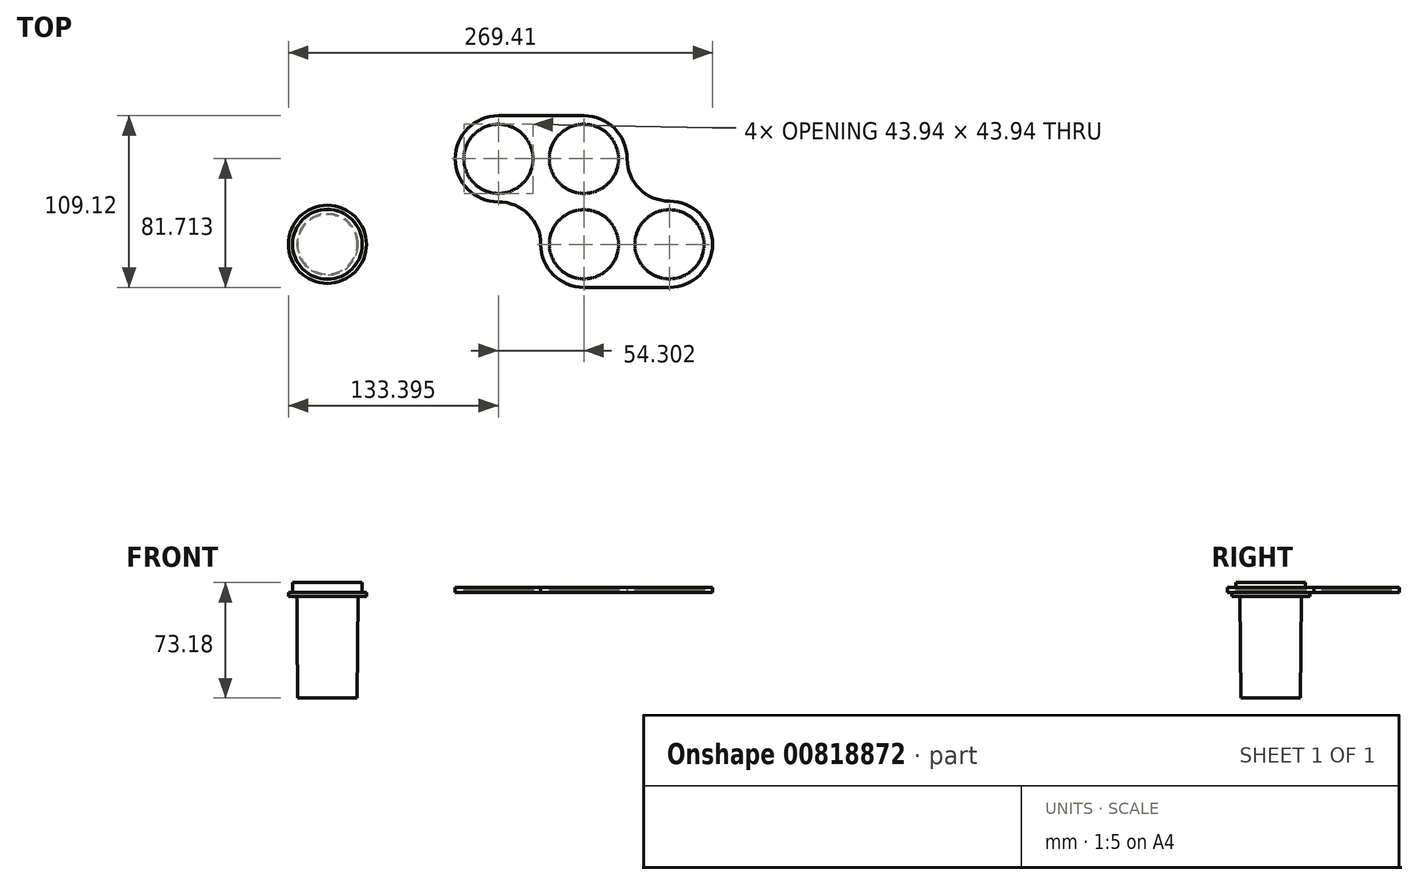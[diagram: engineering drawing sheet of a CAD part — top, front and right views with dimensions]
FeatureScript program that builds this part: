
annotation { "Feature Type Name" : "Feature", "Feature Type Description" : "" }
export const myFeature = defineFeature(function(context is Context, id is Id, definition is map)
    precondition{}
    {
        {
            assignVariable(context, id + "F0", {"name" : "hbottle", "anyValue" : 77 * mm});
        }
        {
            assignVariable(context, id + "F1", {"name" : "thick", "anyValue" : 3.17 * mm});
        }
        {
            var Q0;
            Q0=qCreatedBy(makeId("Top.planeOp"),FACE);
            var sketch = newSketch(context, id + "F2", { "sketchPlane" : qUnion([Q0])});
            skCircle(sketch, "E0", {"center": v(0, 0) * mm, "radius": 21.97 * mm, "construction": true});
            skCircle(sketch, "E1.0.1.0", {"center": v(0, 54.3) * mm, "radius": 21.97 * mm, "construction": true});
            skCircle(sketch, "E1.0.2.0", {"center": v(0, 108.6) * mm, "radius": 21.97 * mm, "construction": true});
            skCircle(sketch, "E1.0.3.0", {"center": v(0, 162.9) * mm, "radius": 21.97 * mm, "construction": true});
            skCircle(sketch, "E1.0.4.0", {"center": v(0, 217.2) * mm, "radius": 21.97 * mm, "construction": true});
            skCircle(sketch, "E1.0.5.0", {"center": v(0, 271.51) * mm, "radius": 21.97 * mm, "construction": true});
            skCircle(sketch, "E1.0.6.0", {"center": v(0, 325.81) * mm, "radius": 21.97 * mm, "construction": true});
            skCircle(sketch, "E1.0.7.0", {"center": v(0, 380.12) * mm, "radius": 21.97 * mm, "construction": true});
            skCircle(sketch, "E1.0.8.0", {"center": v(0, 434.42) * mm, "radius": 21.97 * mm, "construction": true});
            skCircle(sketch, "E1.0.9.0", {"center": v(0, 488.72) * mm, "radius": 21.97 * mm, "construction": true});
            skCircle(sketch, "E1.1.0.0", {"center": v(54.3, 0) * mm, "radius": 21.97 * mm, "construction": true});
            skCircle(sketch, "E1.1.1.0", {"center": v(54.3, 54.3) * mm, "radius": 21.97 * mm, "construction": true});
            skCircle(sketch, "E1.1.2.0", {"center": v(54.3, 108.6) * mm, "radius": 21.97 * mm, "construction": true});
            skCircle(sketch, "E1.1.3.0", {"center": v(54.3, 162.9) * mm, "radius": 21.97 * mm, "construction": true});
            skCircle(sketch, "E1.1.4.0", {"center": v(54.3, 217.2) * mm, "radius": 21.97 * mm, "construction": true});
            skCircle(sketch, "E1.1.5.0", {"center": v(54.3, 271.51) * mm, "radius": 21.97 * mm, "construction": true});
            skCircle(sketch, "E1.1.6.0", {"center": v(54.3, 325.81) * mm, "radius": 21.97 * mm, "construction": true});
            skCircle(sketch, "E1.1.7.0", {"center": v(54.3, 380.12) * mm, "radius": 21.97 * mm, "construction": true});
            skCircle(sketch, "E1.1.8.0", {"center": v(54.3, 434.42) * mm, "radius": 21.97 * mm, "construction": true});
            skCircle(sketch, "E1.1.9.0", {"center": v(54.3, 488.72) * mm, "radius": 21.97 * mm, "construction": true});
            skCircle(sketch, "E1.2.0.0", {"center": v(108.6, 0) * mm, "radius": 21.97 * mm, "construction": true});
            skCircle(sketch, "E1.2.1.0", {"center": v(108.6, 54.3) * mm, "radius": 21.97 * mm, "construction": true});
            skCircle(sketch, "E1.2.2.0", {"center": v(108.6, 108.6) * mm, "radius": 21.97 * mm, "construction": true});
            skCircle(sketch, "E1.2.3.0", {"center": v(108.6, 162.9) * mm, "radius": 21.97 * mm, "construction": true});
            skCircle(sketch, "E1.2.4.0", {"center": v(108.6, 217.2) * mm, "radius": 21.97 * mm, "construction": true});
            skCircle(sketch, "E1.2.5.0", {"center": v(108.6, 271.51) * mm, "radius": 21.97 * mm, "construction": true});
            skCircle(sketch, "E1.2.6.0", {"center": v(108.6, 325.81) * mm, "radius": 21.97 * mm, "construction": true});
            skCircle(sketch, "E1.2.7.0", {"center": v(108.6, 380.12) * mm, "radius": 21.97 * mm, "construction": true});
            skCircle(sketch, "E1.2.8.0", {"center": v(108.6, 434.42) * mm, "radius": 21.97 * mm, "construction": true});
            skCircle(sketch, "E1.2.9.0", {"center": v(108.6, 488.72) * mm, "radius": 21.97 * mm, "construction": true});
            skCircle(sketch, "E1.3.0.0", {"center": v(162.9, 0) * mm, "radius": 21.97 * mm, "construction": true});
            skCircle(sketch, "E1.3.1.0", {"center": v(162.9, 54.3) * mm, "radius": 21.97 * mm, "construction": true});
            skCircle(sketch, "E1.3.2.0", {"center": v(162.9, 108.6) * mm, "radius": 21.97 * mm, "construction": true});
            skCircle(sketch, "E1.3.3.0", {"center": v(162.9, 162.9) * mm, "radius": 21.97 * mm, "construction": true});
            skCircle(sketch, "E1.3.4.0", {"center": v(162.9, 217.2) * mm, "radius": 21.97 * mm, "construction": true});
            skCircle(sketch, "E1.3.5.0", {"center": v(162.9, 271.51) * mm, "radius": 21.97 * mm, "construction": true});
            skCircle(sketch, "E1.3.6.0", {"center": v(162.9, 325.81) * mm, "radius": 21.97 * mm, "construction": true});
            skCircle(sketch, "E1.3.7.0", {"center": v(162.9, 380.12) * mm, "radius": 21.97 * mm, "construction": true});
            skCircle(sketch, "E1.3.8.0", {"center": v(162.9, 434.42) * mm, "radius": 21.97 * mm, "construction": true});
            skCircle(sketch, "E1.3.9.0", {"center": v(162.9, 488.72) * mm, "radius": 21.97 * mm, "construction": true});
            skCircle(sketch, "E1.4.0.0", {"center": v(217.2, 0) * mm, "radius": 21.97 * mm, "construction": true});
            skCircle(sketch, "E1.4.1.0", {"center": v(217.2, 54.3) * mm, "radius": 21.97 * mm, "construction": true});
            skCircle(sketch, "E1.4.2.0", {"center": v(217.2, 108.6) * mm, "radius": 21.97 * mm, "construction": true});
            skCircle(sketch, "E1.4.3.0", {"center": v(217.2, 162.9) * mm, "radius": 21.97 * mm, "construction": true});
            skCircle(sketch, "E1.4.4.0", {"center": v(217.2, 217.2) * mm, "radius": 21.97 * mm, "construction": true});
            skCircle(sketch, "E1.4.5.0", {"center": v(217.2, 271.51) * mm, "radius": 21.97 * mm, "construction": true});
            skCircle(sketch, "E1.4.6.0", {"center": v(217.2, 325.81) * mm, "radius": 21.97 * mm, "construction": true});
            skCircle(sketch, "E1.4.7.0", {"center": v(217.2, 380.12) * mm, "radius": 21.97 * mm, "construction": true});
            skCircle(sketch, "E1.4.8.0", {"center": v(217.2, 434.42) * mm, "radius": 21.97 * mm, "construction": true});
            skCircle(sketch, "E1.4.9.0", {"center": v(217.2, 488.72) * mm, "radius": 21.97 * mm, "construction": true});
            skCircle(sketch, "E1.5.0.0", {"center": v(271.51, 0) * mm, "radius": 21.97 * mm, "construction": true});
            skCircle(sketch, "E1.5.1.0", {"center": v(271.51, 54.3) * mm, "radius": 21.97 * mm, "construction": true});
            skCircle(sketch, "E1.5.2.0", {"center": v(271.51, 108.6) * mm, "radius": 21.97 * mm, "construction": true});
            skCircle(sketch, "E1.5.3.0", {"center": v(271.51, 162.9) * mm, "radius": 21.97 * mm, "construction": true});
            skCircle(sketch, "E1.5.4.0", {"center": v(271.51, 217.2) * mm, "radius": 21.97 * mm, "construction": true});
            skCircle(sketch, "E1.5.5.0", {"center": v(271.51, 271.51) * mm, "radius": 21.97 * mm, "construction": true});
            skCircle(sketch, "E1.5.6.0", {"center": v(271.51, 325.81) * mm, "radius": 21.97 * mm, "construction": true});
            skCircle(sketch, "E1.5.7.0", {"center": v(271.51, 380.12) * mm, "radius": 21.97 * mm, "construction": true});
            skCircle(sketch, "E1.5.8.0", {"center": v(271.51, 434.42) * mm, "radius": 21.97 * mm, "construction": true});
            skCircle(sketch, "E1.5.9.0", {"center": v(271.51, 488.72) * mm, "radius": 21.97 * mm, "construction": true});
            skCircle(sketch, "E1.6.0.0", {"center": v(325.81, 0) * mm, "radius": 21.97 * mm, "construction": true});
            skCircle(sketch, "E1.6.1.0", {"center": v(325.81, 54.3) * mm, "radius": 21.97 * mm, "construction": true});
            skCircle(sketch, "E1.6.2.0", {"center": v(325.81, 108.6) * mm, "radius": 21.97 * mm, "construction": true});
            skCircle(sketch, "E1.6.3.0", {"center": v(325.81, 162.9) * mm, "radius": 21.97 * mm, "construction": true});
            skCircle(sketch, "E1.6.4.0", {"center": v(325.81, 217.2) * mm, "radius": 21.97 * mm, "construction": true});
            skCircle(sketch, "E1.6.5.0", {"center": v(325.81, 271.51) * mm, "radius": 21.97 * mm, "construction": true});
            skCircle(sketch, "E1.6.6.0", {"center": v(325.81, 325.81) * mm, "radius": 21.97 * mm, "construction": true});
            skCircle(sketch, "E1.6.7.0", {"center": v(325.81, 380.12) * mm, "radius": 21.97 * mm, "construction": true});
            skCircle(sketch, "E1.6.8.0", {"center": v(325.81, 434.42) * mm, "radius": 21.97 * mm, "construction": true});
            skCircle(sketch, "E1.6.9.0", {"center": v(325.81, 488.72) * mm, "radius": 21.97 * mm, "construction": true});
            skCircle(sketch, "E1.7.0.0", {"center": v(380.12, 0) * mm, "radius": 21.97 * mm, "construction": true});
            skCircle(sketch, "E1.7.1.0", {"center": v(380.12, 54.3) * mm, "radius": 21.97 * mm, "construction": true});
            skCircle(sketch, "E1.7.2.0", {"center": v(380.12, 108.6) * mm, "radius": 21.97 * mm, "construction": true});
            skCircle(sketch, "E1.7.3.0", {"center": v(380.12, 162.9) * mm, "radius": 21.97 * mm, "construction": true});
            skCircle(sketch, "E1.7.4.0", {"center": v(380.12, 217.2) * mm, "radius": 21.97 * mm, "construction": true});
            skCircle(sketch, "E1.7.5.0", {"center": v(380.12, 271.51) * mm, "radius": 21.97 * mm, "construction": true});
            skCircle(sketch, "E1.7.6.0", {"center": v(380.12, 325.81) * mm, "radius": 21.97 * mm, "construction": true});
            skCircle(sketch, "E1.7.7.0", {"center": v(380.12, 380.12) * mm, "radius": 21.97 * mm, "construction": true});
            skCircle(sketch, "E1.7.8.0", {"center": v(380.12, 434.42) * mm, "radius": 21.97 * mm, "construction": true});
            skCircle(sketch, "E1.7.9.0", {"center": v(380.12, 488.72) * mm, "radius": 21.97 * mm, "construction": true});
            skCircle(sketch, "E1.8.0.0", {"center": v(434.42, 0) * mm, "radius": 21.97 * mm, "construction": true});
            skCircle(sketch, "E1.8.1.0", {"center": v(434.42, 54.3) * mm, "radius": 21.97 * mm, "construction": true});
            skCircle(sketch, "E1.8.2.0", {"center": v(434.42, 108.6) * mm, "radius": 21.97 * mm, "construction": true});
            skCircle(sketch, "E1.8.3.0", {"center": v(434.42, 162.9) * mm, "radius": 21.97 * mm, "construction": true});
            skCircle(sketch, "E1.8.4.0", {"center": v(434.42, 217.2) * mm, "radius": 21.97 * mm, "construction": true});
            skCircle(sketch, "E1.8.5.0", {"center": v(434.42, 271.51) * mm, "radius": 21.97 * mm, "construction": true});
            skCircle(sketch, "E1.8.6.0", {"center": v(434.42, 325.81) * mm, "radius": 21.97 * mm, "construction": true});
            skCircle(sketch, "E1.8.7.0", {"center": v(434.42, 380.12) * mm, "radius": 21.97 * mm, "construction": true});
            skCircle(sketch, "E1.8.8.0", {"center": v(434.42, 434.42) * mm, "radius": 21.97 * mm, "construction": true});
            skCircle(sketch, "E1.8.9.0", {"center": v(434.42, 488.72) * mm, "radius": 21.97 * mm, "construction": true});
            skCircle(sketch, "E1.9.0.0", {"center": v(488.72, 0) * mm, "radius": 21.97 * mm, "construction": true});
            skCircle(sketch, "E1.9.1.0", {"center": v(488.72, 54.3) * mm, "radius": 21.97 * mm, "construction": true});
            skCircle(sketch, "E1.9.2.0", {"center": v(488.72, 108.6) * mm, "radius": 21.97 * mm, "construction": true});
            skCircle(sketch, "E1.9.3.0", {"center": v(488.72, 162.9) * mm, "radius": 21.97 * mm, "construction": true});
            skCircle(sketch, "E1.9.4.0", {"center": v(488.72, 217.2) * mm, "radius": 21.97 * mm, "construction": true});
            skCircle(sketch, "E1.9.5.0", {"center": v(488.72, 271.51) * mm, "radius": 21.97 * mm, "construction": true});
            skCircle(sketch, "E1.9.6.0", {"center": v(488.72, 325.81) * mm, "radius": 21.97 * mm, "construction": true});
            skCircle(sketch, "E1.9.7.0", {"center": v(488.72, 380.12) * mm, "radius": 21.97 * mm, "construction": true});
            skCircle(sketch, "E1.9.8.0", {"center": v(488.72, 434.42) * mm, "radius": 21.97 * mm, "construction": true});
            skCircle(sketch, "E1.9.9.0", {"center": v(488.72, 488.72) * mm, "radius": 21.97 * mm, "construction": true});
            skLineSegment(sketch, "E1.direction1", {"start": v(0, 0) * mm, "end": v(54.3, 0) * mm, "construction": true});
            skLineSegment(sketch, "E1.direction2", {"start": v(0, 0) * mm, "end": v(0, 54.3) * mm, "construction": true});
            skSolve(sketch);
        }
        {
            var Q0;
            Q0=qCreatedBy(makeId("Top.planeOp"),FACE);
            var sketch = newSketch(context, id + "F3", { "sketchPlane" : qUnion([Q0])});
            skCircle(sketch, "E2.0", {"center": v(0, 0) * mm, "radius": 21.97 * mm});
            skCircle(sketch, "E3.0", {"center": v(0, 54.3) * mm, "radius": 21.97 * mm});
            skCircle(sketch, "E4.0", {"center": v(54.3, 0) * mm, "radius": 21.97 * mm});
            skArc(sketch, "E5", {"start": v(0, -27.15) * mm, "mid": v(-19.2, -19.2) * mm, "end": v(-27.15, 0) * mm});
            skArc(sketch, "E6", {"start": v(-27.15, 54.3) * mm, "mid": v(0, 81.45) * mm, "end": v(27.15, 54.3) * mm});
            skArc(sketch, "E7", {"start": v(54.3, 27.15) * mm, "mid": v(81.45, 0) * mm, "end": v(54.3, -27.15) * mm});
            skLineSegment(sketch, "E8", {"start": v(-27.15, 0) * mm, "end": v(-27.15, 54.3) * mm});
            skLineSegment(sketch, "E9", {"start": v(0, -27.15) * mm, "end": v(54.3, -27.15) * mm});
            skArc(sketch, "E10", {"start": v(54.3, 27.15) * mm, "mid": v(35.1, 35.1) * mm, "end": v(27.15, 54.3) * mm});
            skCircle(sketch, "E11.0", {"center": v(108.6, 54.3) * mm, "radius": 21.97 * mm});
            skCircle(sketch, "E12.0", {"center": v(162.9, 0) * mm, "radius": 21.97 * mm});
            skCircle(sketch, "E13.0", {"center": v(54.3, 162.9) * mm, "radius": 21.97 * mm});
            skCircle(sketch, "E14.0", {"center": v(162.9, 54.3) * mm, "radius": 21.97 * mm});
            skCircle(sketch, "E15.0", {"center": v(217.2, 0) * mm, "radius": 21.97 * mm});
            skCircle(sketch, "E16.0", {"center": v(0, 162.9) * mm, "radius": 21.97 * mm});
            skCircle(sketch, "E17.0", {"center": v(108.6, 162.9) * mm, "radius": 21.97 * mm});
            skCircle(sketch, "E18.0", {"center": v(54.3, 217.2) * mm, "radius": 21.97 * mm});
            skCircle(sketch, "E19.0", {"center": v(217.2, 217.2) * mm, "radius": 21.97 * mm});
            skCircle(sketch, "E20.0", {"center": v(217.2, 162.9) * mm, "radius": 21.97 * mm});
            skCircle(sketch, "E21.0", {"center": v(217.2, 108.6) * mm, "radius": 21.97 * mm});
            skArc(sketch, "E22", {"start": v(0, 135.76) * mm, "mid": v(-27.15, 162.9) * mm, "end": v(0, 190.06) * mm});
            skArc(sketch, "E23", {"start": v(27.15, 217.2) * mm, "mid": v(54.3, 244.36) * mm, "end": v(81.45, 217.2) * mm});
            skArc(sketch, "E24", {"start": v(108.6, 190.06) * mm, "mid": v(135.76, 162.9) * mm, "end": v(108.6, 135.76) * mm});
            skArc(sketch, "E25", {"start": v(108.6, 27.15) * mm, "mid": v(81.45, 54.3) * mm, "end": v(108.6, 81.45) * mm});
            skArc(sketch, "E26", {"start": v(162.9, -27.15) * mm, "mid": v(143.7, -19.2) * mm, "end": v(135.76, 0) * mm});
            skArc(sketch, "E27", {"start": v(162.9, 81.45) * mm, "mid": v(182.1, 73.5) * mm, "end": v(190.06, 54.3) * mm});
            skArc(sketch, "E28", {"start": v(217.2, 27.15) * mm, "mid": v(244.36, 0) * mm, "end": v(217.2, -27.15) * mm});
            skArc(sketch, "E29", {"start": v(190.06, 108.6) * mm, "mid": v(217.2, 81.45) * mm, "end": v(244.36, 108.6) * mm});
            skArc(sketch, "E30", {"start": v(190.06, 217.2) * mm, "mid": v(217.2, 244.36) * mm, "end": v(244.36, 217.2) * mm});
            skArc(sketch, "E31", {"start": v(108.6, 190.06) * mm, "mid": v(89.4, 198.01) * mm, "end": v(81.45, 217.2) * mm});
            skArc(sketch, "E32", {"start": v(27.15, 217.2) * mm, "mid": v(19.2, 198.01) * mm, "end": v(0, 190.06) * mm});
            skArc(sketch, "E33", {"start": v(190.06, 54.3) * mm, "mid": v(198.01, 35.1) * mm, "end": v(217.2, 27.15) * mm});
            skArc(sketch, "E34", {"start": v(135.76, 0) * mm, "mid": v(127.8, 19.2) * mm, "end": v(108.6, 27.15) * mm});
            skLineSegment(sketch, "E35", {"start": v(0, 135.76) * mm, "end": v(108.6, 135.76) * mm});
            skLineSegment(sketch, "E36", {"start": v(108.6, 81.45) * mm, "end": v(162.9, 81.45) * mm});
            skLineSegment(sketch, "E37", {"start": v(162.9, -27.15) * mm, "end": v(217.2, -27.15) * mm});
            skLineSegment(sketch, "E38", {"start": v(244.36, 217.2) * mm, "end": v(244.36, 108.6) * mm});
            skLineSegment(sketch, "E39", {"start": v(190.06, 217.2) * mm, "end": v(190.06, 108.6) * mm});
            skCircle(sketch, "E40.0", {"center": v(162.9, 271.51) * mm, "radius": 21.97 * mm});
            skCircle(sketch, "E41.0", {"center": v(162.9, 325.81) * mm, "radius": 21.97 * mm});
            skCircle(sketch, "E42.0", {"center": v(108.6, 325.81) * mm, "radius": 21.97 * mm});
            skCircle(sketch, "E43.0", {"center": v(108.6, 380.12) * mm, "radius": 21.97 * mm});
            skCircle(sketch, "E44.0", {"center": v(54.3, 380.12) * mm, "radius": 21.97 * mm});
            skArc(sketch, "E45", {"start": v(54.3, 352.97) * mm, "mid": v(27.15, 380.12) * mm, "end": v(54.3, 407.27) * mm});
            skArc(sketch, "E46", {"start": v(81.45, 325.81) * mm, "mid": v(89.4, 306.62) * mm, "end": v(108.6, 298.66) * mm});
            skArc(sketch, "E47", {"start": v(108.6, 407.27) * mm, "mid": v(127.8, 399.32) * mm, "end": v(135.76, 380.12) * mm});
            skArc(sketch, "E48", {"start": v(162.9, 352.97) * mm, "mid": v(182.1, 345.01) * mm, "end": v(190.06, 325.81) * mm});
            skArc(sketch, "E49", {"start": v(135.76, 271.51) * mm, "mid": v(162.9, 244.36) * mm, "end": v(190.06, 271.51) * mm});
            skArc(sketch, "E50", {"start": v(81.45, 325.81) * mm, "mid": v(73.5, 345.01) * mm, "end": v(54.3, 352.97) * mm});
            skArc(sketch, "E51", {"start": v(135.76, 271.51) * mm, "mid": v(127.8, 290.71) * mm, "end": v(108.6, 298.66) * mm});
            skArc(sketch, "E52", {"start": v(162.9, 352.97) * mm, "mid": v(143.7, 360.92) * mm, "end": v(135.76, 380.12) * mm});
            skLineSegment(sketch, "E53", {"start": v(54.3, 407.27) * mm, "end": v(108.6, 407.27) * mm});
            skLineSegment(sketch, "E54", {"start": v(190.06, 271.51) * mm, "end": v(190.06, 325.81) * mm});
            skSolve(sketch);
        }
        {
            var Q0;
            Q0=qCreatedBy(makeId("Top.planeOp"),FACE);
            var sketch = newSketch(context, id + "F4", { "sketchPlane" : qUnion([Q0])});
            skArc(sketch, "E55.0", {"start": v(0, -27.4) * mm, "mid": v(-19.38, -19.38) * mm, "end": v(-27.4, 0) * mm});
            skArc(sketch, "E55.1", {"start": v(54.3, 27.4) * mm, "mid": v(81.7, 0) * mm, "end": v(54.3, -27.4) * mm});
            skArc(sketch, "E55.2", {"start": v(54.3, 27.4) * mm, "mid": v(35.28, 35.28) * mm, "end": v(27.4, 54.3) * mm});
            skLineSegment(sketch, "E55.3", {"start": v(0, -27.4) * mm, "end": v(54.3, -27.4) * mm});
            skArc(sketch, "E55.4", {"start": v(-27.4, 54.3) * mm, "mid": v(0, 81.7) * mm, "end": v(27.4, 54.3) * mm});
            skLineSegment(sketch, "E55.5", {"start": v(-27.4, 0) * mm, "end": v(-27.4, 54.3) * mm});
            skPoint(sketch, "E56.centerSnap0", {"position": v(81.7, 0) * mm});
            skArc(sketch, "E57.0", {"start": v(108.6, 190.31) * mm, "mid": v(136.01, 162.9) * mm, "end": v(108.6, 135.5) * mm});
            skArc(sketch, "E57.1", {"start": v(26.9, 217.2) * mm, "mid": v(54.3, 244.62) * mm, "end": v(81.7, 217.2) * mm});
            skArc(sketch, "E57.2", {"start": v(26.9, 217.2) * mm, "mid": v(19.02, 198.2) * mm, "end": v(0, 190.31) * mm});
            skArc(sketch, "E57.3", {"start": v(108.6, 190.31) * mm, "mid": v(89.59, 198.2) * mm, "end": v(81.7, 217.2) * mm});
            skArc(sketch, "E57.4", {"start": v(0, 135.5) * mm, "mid": v(-27.4, 162.9) * mm, "end": v(0, 190.31) * mm});
            skLineSegment(sketch, "E57.5", {"start": v(0, 135.5) * mm, "end": v(108.6, 135.5) * mm});
            skLineSegment(sketch, "E58.0", {"start": v(189.8, 217.2) * mm, "end": v(189.8, 108.6) * mm});
            skArc(sketch, "E58.1", {"start": v(189.8, 217.2) * mm, "mid": v(217.2, 244.62) * mm, "end": v(244.62, 217.2) * mm});
            skLineSegment(sketch, "E58.2", {"start": v(244.62, 217.2) * mm, "end": v(244.62, 108.6) * mm});
            skArc(sketch, "E58.3", {"start": v(189.8, 108.6) * mm, "mid": v(217.2, 81.2) * mm, "end": v(244.62, 108.6) * mm});
            skArc(sketch, "E59.0", {"start": v(108.6, 26.9) * mm, "mid": v(81.2, 54.3) * mm, "end": v(108.6, 81.7) * mm});
            skArc(sketch, "E59.1", {"start": v(135.5, 0) * mm, "mid": v(127.62, 19.02) * mm, "end": v(108.6, 26.9) * mm});
            skLineSegment(sketch, "E59.2", {"start": v(108.6, 81.7) * mm, "end": v(162.9, 81.7) * mm});
            skArc(sketch, "E59.3", {"start": v(162.9, -27.4) * mm, "mid": v(143.53, -19.38) * mm, "end": v(135.5, 0) * mm});
            skArc(sketch, "E59.4", {"start": v(162.9, 81.7) * mm, "mid": v(182.29, 73.68) * mm, "end": v(190.31, 54.3) * mm});
            skArc(sketch, "E59.5", {"start": v(190.31, 54.3) * mm, "mid": v(198.2, 35.28) * mm, "end": v(217.2, 27.4) * mm});
            skArc(sketch, "E59.6", {"start": v(217.2, 27.4) * mm, "mid": v(244.62, 0) * mm, "end": v(217.2, -27.4) * mm});
            skLineSegment(sketch, "E59.7", {"start": v(162.9, -27.4) * mm, "end": v(217.2, -27.4) * mm});
            skArc(sketch, "E60.0", {"start": v(54.3, 352.71) * mm, "mid": v(26.9, 380.12) * mm, "end": v(54.3, 407.52) * mm});
            skArc(sketch, "E60.1", {"start": v(81.2, 325.81) * mm, "mid": v(73.32, 344.83) * mm, "end": v(54.3, 352.71) * mm});
            skLineSegment(sketch, "E60.2", {"start": v(54.3, 407.52) * mm, "end": v(108.6, 407.52) * mm});
            skArc(sketch, "E60.3", {"start": v(81.2, 325.81) * mm, "mid": v(89.23, 306.44) * mm, "end": v(108.6, 298.4) * mm});
            skArc(sketch, "E60.4", {"start": v(135.5, 271.51) * mm, "mid": v(127.62, 290.53) * mm, "end": v(108.6, 298.4) * mm});
            skArc(sketch, "E60.5", {"start": v(135.5, 271.51) * mm, "mid": v(162.9, 244.1) * mm, "end": v(190.31, 271.51) * mm});
            skArc(sketch, "E60.6", {"start": v(108.6, 407.52) * mm, "mid": v(127.98, 399.5) * mm, "end": v(136.01, 380.12) * mm});
            skArc(sketch, "E60.7", {"start": v(162.9, 353.22) * mm, "mid": v(143.89, 361.1) * mm, "end": v(136.01, 380.12) * mm});
            skArc(sketch, "E60.8", {"start": v(162.9, 353.22) * mm, "mid": v(182.29, 345.2) * mm, "end": v(190.31, 325.81) * mm});
            skLineSegment(sketch, "E60.9", {"start": v(190.31, 271.51) * mm, "end": v(190.31, 325.81) * mm});
            skSolve(sketch);
        }
        {
            var Q0;
            Q0=qCreatedBy(makeId("Top.planeOp"),FACE);
            var sketch = newSketch(context, id + "F5", { "sketchPlane" : qUnion([Q0])});
            skCircle(sketch, "E61", {"center": v(0, 0) * mm, "radius": 22.1 * mm});
            skCircle(sketch, "E62", {"center": v(0, 0) * mm, "radius": 24.8 * mm});
            skSolve(sketch);
        }
        {
            var Q0;
            Q0=makeQuery(id+"F5.imprint","IMPRINT",FACE,{"disambiguationData":[TD([[makeQuery(id+"F5.imprint","IMPRINT",EDGE,{"derivedFrom":sQuery(id+"F5.wireOp",EDGE,"E61")}),1.0]])]});
            extrude(context, id + "F6", {"entities" : qUnion([Q0]), "depth" : 6.35 * mm, "offsetDistance" : 25.4 * mm, "hasSecondDirection" : true, "secondDirectionOppositeDirection" : true, "secondDirectionDepth" : 2.54 * mm});
        }
        {
            var Q0;
            Q0=makeQuery(id+"F5.imprint","IMPRINT",FACE,{"disambiguationData":[TD([[makeQuery(id+"F5.imprint","IMPRINT",EDGE,{"derivedFrom":sQuery(id+"F5.wireOp",EDGE,"E61")}),-1.0]])]});
            extrude(context, id + "F7", {"entities" : qUnion([Q0]), "operationType" : NewBodyOperationType.ADD, "oppositeDirection" : true, "depth" : 2.54 * mm, "offsetDistance" : 25.4 * mm});
        }
        {
            var Q0;
            {var subQ0=sQuery(id+"F5.wireOp",EDGE,"E61");Q0=makeQuery(id+"F7.boolean.opBoolean","MERGE",FACE,{"derivedFrom":[makeQuery(id+"F6.opExtrude","CAP_FACE",FACE,{"disambiguationData":[OSD([subQ0])],"isStart":true}),makeQuery(id+"F7.opExtrude","CAP_FACE",FACE,{"disambiguationData":[OSD([subQ0,sQuery(id+"F5.wireOp",EDGE,"E62")])],"isStart":false})]});}
            var sketch = newSketch(context, id + "F8", { "sketchPlane" : qUnion([Q0])});
            skCircle(sketch, "E63", {"center": v(0, 0) * mm, "radius": 22.62 * mm});
            skSolve(sketch);
        }
        {
            var Q0;
            Q0=makeQuery(id+"F8.imprint","IMPRINT",FACE,{"disambiguationData":[TD([[makeQuery(id+"F8.imprint","IMPRINT",EDGE,{"derivedFrom":sQuery(id+"F8.wireOp",EDGE,"E63")}),1.0]])]});
            extrude(context, id + "F9", {"entities" : qUnion([Q0]), "depth" : 1 / 406.4 * mm, "offsetDistance" : 25.4 * mm});
        }
        {
            var Q0;
            Q0=makeQuery(id+"F9.opExtrude","CAP_FACE",FACE,{"disambiguationData":[OSD([sQuery(id+"F8.wireOp",EDGE,"E63")])],"isStart":false});
            var sketch = newSketch(context, id + "F10", { "sketchPlane" : qUnion([Q0])});
            skCircle(sketch, "E64", {"center": v(0, 0) * mm, "radius": 19.45 * mm});
            skSolve(sketch);
        }
        {
            var Q0;
            {var subQ0=sQuery(id+"F5.wireOp",EDGE,"E61");Q0=makeQuery(id+"F7.boolean.opBoolean","MERGE",FACE,{"derivedFrom":[makeQuery(id+"F6.opExtrude","CAP_FACE",FACE,{"disambiguationData":[OSD([subQ0])],"isStart":true}),makeQuery(id+"F7.opExtrude","CAP_FACE",FACE,{"disambiguationData":[OSD([subQ0,sQuery(id+"F5.wireOp",EDGE,"E62")])],"isStart":false})]});}
            cPlane(context, id + "F11", {"entities" : qUnion([Q0]), "cplaneType" : CPlaneType.OFFSET, "offset" : getVariable(context, 'hbottle') - 12.7 * mm, "width" : 152.4 * mm, "height" : 152.4 * mm});
        }
        {
            var Q0;
            Q0=qCreatedBy(id+"F11.planeOp",FACE);
            var sketch = newSketch(context, id + "F12", { "sketchPlane" : qUnion([Q0])});
            skCircle(sketch, "E65", {"center": v(0, 0) * mm, "radius": 18.95 * mm});
            skSolve(sketch);
        }
        {
            var Q1;
            Q1 = qSketchRegion(id + "F10", true);
            var Q2;
            Q2 = qSketchRegion(id + "F12", true);
            loft(context, id + "F13", {"operationType" : NewBodyOperationType.ADD, "sheetProfilesArray" : [{ "sheetProfileEntities" : qUnion([Q1]) }, { "sheetProfileEntities" : qUnion([Q2]) }]});
        }
        {
            var Q0;
            Q0=qCreatedBy(makeId("Top.planeOp"),FACE);
            var sketch = newSketch(context, id + "F14", { "sketchPlane" : qUnion([Q0])});
            skLineSegment(sketch, "E66", {"start": v(3.5, 0) * mm, "end": v(54.3, 0) * mm, "construction": true});
            skLineSegment(sketch, "E67", {"start": v(54.3, 0) * mm, "end": v(69.84, -15.54) * mm, "construction": true});
            skLineSegment(sketch, "E68", {"start": v(54.3, 0) * mm, "end": v(70.16, -15.2) * mm, "construction": true});
            skLineSegment(sketch, "E69", {"start": v(54.3, 0) * mm, "end": v(70.48, -14.87) * mm, "construction": true});
            skLineSegment(sketch, "E70", {"start": v(54.3, 0) * mm, "end": v(70.78, -14.53) * mm, "construction": true});
            skLineSegment(sketch, "E71", {"start": v(69.84, -15.54) * mm, "end": v(70.16, -15.2) * mm});
            skLineSegment(sketch, "E72", {"start": v(70.16, -15.2) * mm, "end": v(70.03, -14.77) * mm});
            skLineSegment(sketch, "E73", {"start": v(70.03, -14.77) * mm, "end": v(70.48, -14.87) * mm});
            skLineSegment(sketch, "E74", {"start": v(70.48, -14.87) * mm, "end": v(70.78, -14.53) * mm});
            skLineSegment(sketch, "E75", {"start": v(54.3, 0) * mm, "end": v(54.3, -21.97) * mm, "construction": true});
            skLineSegment(sketch, "E76.1.0", {"start": v(70.78, -14.53) * mm, "end": v(71.08, -14.18) * mm});
            skLineSegment(sketch, "E76.1.1", {"start": v(70.92, -13.75) * mm, "end": v(71.38, -13.83) * mm});
            skLineSegment(sketch, "E76.1.2", {"start": v(71.38, -13.83) * mm, "end": v(71.66, -13.47) * mm});
            skLineSegment(sketch, "E76.1.3", {"start": v(71.08, -14.18) * mm, "end": v(70.92, -13.75) * mm});
            skLineSegment(sketch, "E76.2.0", {"start": v(71.66, -13.47) * mm, "end": v(71.94, -13.1) * mm});
            skLineSegment(sketch, "E76.2.1", {"start": v(71.75, -12.68) * mm, "end": v(72.21, -12.73) * mm});
            skLineSegment(sketch, "E76.2.2", {"start": v(72.21, -12.73) * mm, "end": v(72.47, -12.35) * mm});
            skLineSegment(sketch, "E76.2.3", {"start": v(71.94, -13.1) * mm, "end": v(71.75, -12.68) * mm});
            skLineSegment(sketch, "E76.3.0", {"start": v(72.47, -12.35) * mm, "end": v(72.73, -11.97) * mm});
            skLineSegment(sketch, "E76.3.1", {"start": v(72.52, -11.56) * mm, "end": v(72.98, -11.58) * mm});
            skLineSegment(sketch, "E76.3.2", {"start": v(72.98, -11.58) * mm, "end": v(73.21, -11.18) * mm});
            skLineSegment(sketch, "E76.3.3", {"start": v(72.73, -11.97) * mm, "end": v(72.52, -11.56) * mm});
            skLineSegment(sketch, "E76.4.0", {"start": v(73.21, -11.18) * mm, "end": v(73.44, -10.79) * mm});
            skLineSegment(sketch, "E76.4.1", {"start": v(73.2, -10.4) * mm, "end": v(73.67, -10.38) * mm});
            skLineSegment(sketch, "E76.4.2", {"start": v(73.67, -10.38) * mm, "end": v(73.88, -9.97) * mm});
            skLineSegment(sketch, "E76.4.3", {"start": v(73.44, -10.79) * mm, "end": v(73.2, -10.4) * mm});
            skLineSegment(sketch, "E76.5.0", {"start": v(73.88, -9.97) * mm, "end": v(74.08, -9.56) * mm});
            skLineSegment(sketch, "E76.5.1", {"start": v(73.82, -9.18) * mm, "end": v(74.28, -9.15) * mm});
            skLineSegment(sketch, "E76.5.2", {"start": v(74.28, -9.15) * mm, "end": v(74.47, -8.73) * mm});
            skLineSegment(sketch, "E76.5.3", {"start": v(74.08, -9.56) * mm, "end": v(73.82, -9.18) * mm});
            skLineSegment(sketch, "E76.6.0", {"start": v(74.47, -8.73) * mm, "end": v(74.64, -8.3) * mm});
            skLineSegment(sketch, "E76.6.1", {"start": v(74.36, -7.94) * mm, "end": v(74.81, -7.87) * mm});
            skLineSegment(sketch, "E76.6.2", {"start": v(74.81, -7.87) * mm, "end": v(74.97, -7.44) * mm});
            skLineSegment(sketch, "E76.6.3", {"start": v(74.64, -8.3) * mm, "end": v(74.36, -7.94) * mm});
            skLineSegment(sketch, "E76.7.0", {"start": v(74.97, -7.44) * mm, "end": v(75.13, -7) * mm});
            skLineSegment(sketch, "E76.7.1", {"start": v(74.82, -6.67) * mm, "end": v(75.27, -6.57) * mm});
            skLineSegment(sketch, "E76.7.2", {"start": v(75.27, -6.57) * mm, "end": v(75.4, -6.13) * mm});
            skLineSegment(sketch, "E76.7.3", {"start": v(75.13, -7) * mm, "end": v(74.82, -6.67) * mm});
            skLineSegment(sketch, "E76.8.0", {"start": v(75.4, -6.13) * mm, "end": v(75.52, -5.69) * mm});
            skLineSegment(sketch, "E76.8.1", {"start": v(75.2, -5.36) * mm, "end": v(75.64, -5.24) * mm});
            skLineSegment(sketch, "E76.8.2", {"start": v(75.64, -5.24) * mm, "end": v(75.74, -4.8) * mm});
            skLineSegment(sketch, "E76.8.3", {"start": v(75.52, -5.69) * mm, "end": v(75.2, -5.36) * mm});
            skLineSegment(sketch, "E76.9.0", {"start": v(75.74, -4.8) * mm, "end": v(75.84, -4.34) * mm});
            skLineSegment(sketch, "E76.9.1", {"start": v(75.5, -4.04) * mm, "end": v(75.93, -3.9) * mm});
            skLineSegment(sketch, "E76.9.2", {"start": v(75.93, -3.9) * mm, "end": v(76, -3.44) * mm});
            skLineSegment(sketch, "E76.9.3", {"start": v(75.84, -4.34) * mm, "end": v(75.5, -4.04) * mm});
            skLineSegment(sketch, "E76.10.0", {"start": v(76, -3.44) * mm, "end": v(76.07, -2.98) * mm});
            skLineSegment(sketch, "E76.10.1", {"start": v(75.7, -2.7) * mm, "end": v(76.13, -2.53) * mm});
            skLineSegment(sketch, "E76.10.2", {"start": v(76.13, -2.53) * mm, "end": v(76.18, -2.07) * mm});
            skLineSegment(sketch, "E76.10.3", {"start": v(76.07, -2.98) * mm, "end": v(75.7, -2.7) * mm});
            skLineSegment(sketch, "E76.11.0", {"start": v(76.18, -2.07) * mm, "end": v(76.21, -1.6) * mm});
            skLineSegment(sketch, "E76.11.1", {"start": v(75.83, -1.35) * mm, "end": v(76.24, -1.15) * mm});
            skLineSegment(sketch, "E76.11.2", {"start": v(76.24, -1.15) * mm, "end": v(76.26, -0.7) * mm});
            skLineSegment(sketch, "E76.11.3", {"start": v(76.21, -1.6) * mm, "end": v(75.83, -1.35) * mm});
            skLineSegment(sketch, "E76.12.0", {"start": v(76.26, -0.7) * mm, "end": v(76.27, -0.23) * mm});
            skLineSegment(sketch, "E76.12.1", {"start": v(75.87, 0) * mm, "end": v(76.27, 0.23) * mm});
            skLineSegment(sketch, "E76.12.2", {"start": v(76.27, 0.23) * mm, "end": v(76.26, 0.7) * mm});
            skLineSegment(sketch, "E76.12.3", {"start": v(76.27, -0.23) * mm, "end": v(75.87, 0) * mm});
            skLineSegment(sketch, "E76.13.0", {"start": v(76.26, 0.7) * mm, "end": v(76.24, 1.15) * mm});
            skLineSegment(sketch, "E76.13.1", {"start": v(75.83, 1.35) * mm, "end": v(76.21, 1.6) * mm});
            skLineSegment(sketch, "E76.13.2", {"start": v(76.21, 1.6) * mm, "end": v(76.18, 2.07) * mm});
            skLineSegment(sketch, "E76.13.3", {"start": v(76.24, 1.15) * mm, "end": v(75.83, 1.35) * mm});
            skLineSegment(sketch, "E76.14.0", {"start": v(76.18, 2.07) * mm, "end": v(76.13, 2.53) * mm});
            skLineSegment(sketch, "E76.14.1", {"start": v(75.7, 2.7) * mm, "end": v(76.07, 2.98) * mm});
            skLineSegment(sketch, "E76.14.2", {"start": v(76.07, 2.98) * mm, "end": v(76, 3.44) * mm});
            skLineSegment(sketch, "E76.14.3", {"start": v(76.13, 2.53) * mm, "end": v(75.7, 2.7) * mm});
            skLineSegment(sketch, "E76.15.0", {"start": v(76, 3.44) * mm, "end": v(75.93, 3.9) * mm});
            skLineSegment(sketch, "E76.15.1", {"start": v(75.5, 4.04) * mm, "end": v(75.84, 4.34) * mm});
            skLineSegment(sketch, "E76.15.2", {"start": v(75.84, 4.34) * mm, "end": v(75.74, 4.8) * mm});
            skLineSegment(sketch, "E76.15.3", {"start": v(75.93, 3.9) * mm, "end": v(75.5, 4.04) * mm});
            skLineSegment(sketch, "E76.16.0", {"start": v(75.74, 4.8) * mm, "end": v(75.64, 5.24) * mm});
            skLineSegment(sketch, "E76.16.1", {"start": v(75.2, 5.36) * mm, "end": v(75.52, 5.69) * mm});
            skLineSegment(sketch, "E76.16.2", {"start": v(75.52, 5.69) * mm, "end": v(75.4, 6.13) * mm});
            skLineSegment(sketch, "E76.16.3", {"start": v(75.64, 5.24) * mm, "end": v(75.2, 5.36) * mm});
            skLineSegment(sketch, "E76.24.0", {"start": v(70.78, 14.53) * mm, "end": v(70.48, 14.87) * mm});
            skLineSegment(sketch, "E76.24.1", {"start": v(70.03, 14.77) * mm, "end": v(70.16, 15.2) * mm});
            skLineSegment(sketch, "E76.24.2", {"start": v(70.16, 15.2) * mm, "end": v(69.84, 15.54) * mm});
            skLineSegment(sketch, "E76.24.3", {"start": v(70.48, 14.87) * mm, "end": v(70.03, 14.77) * mm});
            skLineSegment(sketch, "E76.25.0", {"start": v(69.84, 15.54) * mm, "end": v(69.5, 15.86) * mm});
            skLineSegment(sketch, "E76.25.1", {"start": v(69.07, 15.72) * mm, "end": v(69.17, 16.17) * mm});
            skLineSegment(sketch, "E76.25.2", {"start": v(69.17, 16.17) * mm, "end": v(68.83, 16.48) * mm});
            skLineSegment(sketch, "E76.25.3", {"start": v(69.5, 15.86) * mm, "end": v(69.07, 15.72) * mm});
            skLineSegment(sketch, "E76.26.0", {"start": v(68.83, 16.48) * mm, "end": v(68.48, 16.78) * mm});
            skLineSegment(sketch, "E76.26.1", {"start": v(68.05, 16.62) * mm, "end": v(68.13, 17.07) * mm});
            skLineSegment(sketch, "E76.26.2", {"start": v(68.13, 17.07) * mm, "end": v(67.77, 17.36) * mm});
            skLineSegment(sketch, "E76.26.3", {"start": v(68.48, 16.78) * mm, "end": v(68.05, 16.62) * mm});
            skLineSegment(sketch, "E76.27.0", {"start": v(67.77, 17.36) * mm, "end": v(67.4, 17.64) * mm});
            skLineSegment(sketch, "E76.27.1", {"start": v(66.98, 17.45) * mm, "end": v(67.03, 17.9) * mm});
            skLineSegment(sketch, "E76.27.2", {"start": v(67.03, 17.9) * mm, "end": v(66.65, 18.17) * mm});
            skLineSegment(sketch, "E76.27.3", {"start": v(67.4, 17.64) * mm, "end": v(66.98, 17.45) * mm});
            skLineSegment(sketch, "E76.28.0", {"start": v(66.65, 18.17) * mm, "end": v(66.27, 18.43) * mm});
            skLineSegment(sketch, "E76.28.1", {"start": v(65.86, 18.21) * mm, "end": v(65.88, 18.67) * mm});
            skLineSegment(sketch, "E76.28.2", {"start": v(65.88, 18.67) * mm, "end": v(65.49, 18.91) * mm});
            skLineSegment(sketch, "E76.28.3", {"start": v(66.27, 18.43) * mm, "end": v(65.86, 18.21) * mm});
            skLineSegment(sketch, "E76.29.0", {"start": v(65.49, 18.91) * mm, "end": v(65.09, 19.14) * mm});
            skLineSegment(sketch, "E76.29.1", {"start": v(64.7, 18.9) * mm, "end": v(64.68, 19.36) * mm});
            skLineSegment(sketch, "E76.29.2", {"start": v(64.68, 19.36) * mm, "end": v(64.28, 19.58) * mm});
            skLineSegment(sketch, "E76.29.3", {"start": v(65.09, 19.14) * mm, "end": v(64.7, 18.9) * mm});
            skLineSegment(sketch, "E76.30.0", {"start": v(64.28, 19.58) * mm, "end": v(63.86, 19.78) * mm});
            skLineSegment(sketch, "E76.30.1", {"start": v(63.49, 19.52) * mm, "end": v(63.45, 19.98) * mm});
            skLineSegment(sketch, "E76.30.2", {"start": v(63.45, 19.98) * mm, "end": v(63.03, 20.16) * mm});
            skLineSegment(sketch, "E76.30.3", {"start": v(63.86, 19.78) * mm, "end": v(63.49, 19.52) * mm});
            skLineSegment(sketch, "E76.31.0", {"start": v(63.03, 20.16) * mm, "end": v(62.6, 20.34) * mm});
            skLineSegment(sketch, "E76.31.1", {"start": v(62.24, 20.06) * mm, "end": v(62.18, 20.51) * mm});
            skLineSegment(sketch, "E76.31.2", {"start": v(62.18, 20.51) * mm, "end": v(61.74, 20.67) * mm});
            skLineSegment(sketch, "E76.31.3", {"start": v(62.6, 20.34) * mm, "end": v(62.24, 20.06) * mm});
            skLineSegment(sketch, "E76.32.0", {"start": v(61.74, 20.67) * mm, "end": v(61.31, 20.82) * mm});
            skLineSegment(sketch, "E76.32.1", {"start": v(60.97, 20.52) * mm, "end": v(60.87, 20.97) * mm});
            skLineSegment(sketch, "E76.32.2", {"start": v(60.87, 20.97) * mm, "end": v(60.43, 21.1) * mm});
            skLineSegment(sketch, "E76.32.3", {"start": v(61.31, 20.82) * mm, "end": v(60.97, 20.52) * mm});
            skLineSegment(sketch, "E76.33.0", {"start": v(60.43, 21.1) * mm, "end": v(59.99, 21.22) * mm});
            skLineSegment(sketch, "E76.33.1", {"start": v(59.67, 20.9) * mm, "end": v(59.54, 21.34) * mm});
            skLineSegment(sketch, "E76.33.2", {"start": v(59.54, 21.34) * mm, "end": v(59.1, 21.44) * mm});
            skLineSegment(sketch, "E76.33.3", {"start": v(59.99, 21.22) * mm, "end": v(59.67, 20.9) * mm});
            skLineSegment(sketch, "E76.34.0", {"start": v(59.1, 21.44) * mm, "end": v(58.65, 21.54) * mm});
            skLineSegment(sketch, "E76.34.1", {"start": v(58.34, 21.19) * mm, "end": v(58.2, 21.62) * mm});
            skLineSegment(sketch, "E76.34.2", {"start": v(58.2, 21.62) * mm, "end": v(57.74, 21.7) * mm});
            skLineSegment(sketch, "E76.34.3", {"start": v(58.65, 21.54) * mm, "end": v(58.34, 21.19) * mm});
            skLineSegment(sketch, "E76.35.0", {"start": v(57.74, 21.7) * mm, "end": v(57.28, 21.77) * mm});
            skLineSegment(sketch, "E76.35.1", {"start": v(57, 21.4) * mm, "end": v(56.83, 21.83) * mm});
            skLineSegment(sketch, "E76.35.2", {"start": v(56.83, 21.83) * mm, "end": v(56.37, 21.87) * mm});
            skLineSegment(sketch, "E76.35.3", {"start": v(57.28, 21.77) * mm, "end": v(57, 21.4) * mm});
            skLineSegment(sketch, "E76.36.0", {"start": v(56.37, 21.87) * mm, "end": v(55.91, 21.91) * mm});
            skLineSegment(sketch, "E76.36.1", {"start": v(55.66, 21.53) * mm, "end": v(55.45, 21.94) * mm});
            skLineSegment(sketch, "E76.36.2", {"start": v(55.45, 21.94) * mm, "end": v(55, 21.96) * mm});
            skLineSegment(sketch, "E76.36.3", {"start": v(55.91, 21.91) * mm, "end": v(55.66, 21.53) * mm});
            skLineSegment(sketch, "E76.37.0", {"start": v(55, 21.96) * mm, "end": v(54.53, 21.97) * mm});
            skLineSegment(sketch, "E76.37.1", {"start": v(54.3, 21.57) * mm, "end": v(54.07, 21.97) * mm});
            skLineSegment(sketch, "E76.37.2", {"start": v(54.07, 21.97) * mm, "end": v(53.61, 21.96) * mm});
            skLineSegment(sketch, "E76.37.3", {"start": v(54.53, 21.97) * mm, "end": v(54.3, 21.57) * mm});
            skLineSegment(sketch, "E76.38.0", {"start": v(53.61, 21.96) * mm, "end": v(53.15, 21.94) * mm});
            skLineSegment(sketch, "E76.38.1", {"start": v(52.95, 21.53) * mm, "end": v(52.7, 21.91) * mm});
            skLineSegment(sketch, "E76.38.2", {"start": v(52.7, 21.91) * mm, "end": v(52.23, 21.87) * mm});
            skLineSegment(sketch, "E76.38.3", {"start": v(53.15, 21.94) * mm, "end": v(52.95, 21.53) * mm});
            skLineSegment(sketch, "E76.39.0", {"start": v(52.23, 21.87) * mm, "end": v(51.78, 21.83) * mm});
            skLineSegment(sketch, "E76.39.1", {"start": v(51.6, 21.4) * mm, "end": v(51.32, 21.77) * mm});
            skLineSegment(sketch, "E76.39.2", {"start": v(51.32, 21.77) * mm, "end": v(50.87, 21.7) * mm});
            skLineSegment(sketch, "E76.39.3", {"start": v(51.78, 21.83) * mm, "end": v(51.6, 21.4) * mm});
            skLineSegment(sketch, "E76.40.0", {"start": v(50.87, 21.7) * mm, "end": v(50.41, 21.62) * mm});
            skLineSegment(sketch, "E76.40.1", {"start": v(50.26, 21.19) * mm, "end": v(49.96, 21.54) * mm});
            skLineSegment(sketch, "E76.40.2", {"start": v(49.96, 21.54) * mm, "end": v(49.5, 21.44) * mm});
            skLineSegment(sketch, "E76.40.3", {"start": v(50.41, 21.62) * mm, "end": v(50.26, 21.19) * mm});
            skLineSegment(sketch, "E76.50.0", {"start": v(38.77, 15.54) * mm, "end": v(38.44, 15.2) * mm});
            skLineSegment(sketch, "E76.50.1", {"start": v(38.58, 14.77) * mm, "end": v(38.13, 14.87) * mm});
            skLineSegment(sketch, "E76.50.2", {"start": v(38.13, 14.87) * mm, "end": v(37.82, 14.53) * mm});
            skLineSegment(sketch, "E76.50.3", {"start": v(38.44, 15.2) * mm, "end": v(38.58, 14.77) * mm});
            skLineSegment(sketch, "E76.51.0", {"start": v(37.82, 14.53) * mm, "end": v(37.52, 14.18) * mm});
            skLineSegment(sketch, "E76.51.1", {"start": v(37.68, 13.75) * mm, "end": v(37.23, 13.83) * mm});
            skLineSegment(sketch, "E76.51.2", {"start": v(37.23, 13.83) * mm, "end": v(36.94, 13.47) * mm});
            skLineSegment(sketch, "E76.51.3", {"start": v(37.52, 14.18) * mm, "end": v(37.68, 13.75) * mm});
            skLineSegment(sketch, "E76.52.0", {"start": v(36.94, 13.47) * mm, "end": v(36.66, 13.1) * mm});
            skLineSegment(sketch, "E76.52.1", {"start": v(36.85, 12.68) * mm, "end": v(36.4, 12.73) * mm});
            skLineSegment(sketch, "E76.52.2", {"start": v(36.4, 12.73) * mm, "end": v(36.13, 12.35) * mm});
            skLineSegment(sketch, "E76.52.3", {"start": v(36.66, 13.1) * mm, "end": v(36.85, 12.68) * mm});
            skLineSegment(sketch, "E76.53.0", {"start": v(36.13, 12.35) * mm, "end": v(35.88, 11.97) * mm});
            skLineSegment(sketch, "E76.53.1", {"start": v(36.09, 11.56) * mm, "end": v(35.63, 11.58) * mm});
            skLineSegment(sketch, "E76.53.2", {"start": v(35.63, 11.58) * mm, "end": v(35.4, 11.18) * mm});
            skLineSegment(sketch, "E76.53.3", {"start": v(35.88, 11.97) * mm, "end": v(36.09, 11.56) * mm});
            skLineSegment(sketch, "E76.54.0", {"start": v(35.4, 11.18) * mm, "end": v(35.16, 10.79) * mm});
            skLineSegment(sketch, "E76.54.1", {"start": v(35.4, 10.4) * mm, "end": v(34.94, 10.38) * mm});
            skLineSegment(sketch, "E76.54.2", {"start": v(34.94, 10.38) * mm, "end": v(34.73, 9.97) * mm});
            skLineSegment(sketch, "E76.54.3", {"start": v(35.16, 10.79) * mm, "end": v(35.4, 10.4) * mm});
            skLineSegment(sketch, "E76.55.0", {"start": v(34.73, 9.97) * mm, "end": v(34.52, 9.56) * mm});
            skLineSegment(sketch, "E76.55.1", {"start": v(34.78, 9.18) * mm, "end": v(34.33, 9.15) * mm});
            skLineSegment(sketch, "E76.55.2", {"start": v(34.33, 9.15) * mm, "end": v(34.14, 8.73) * mm});
            skLineSegment(sketch, "E76.55.3", {"start": v(34.52, 9.56) * mm, "end": v(34.78, 9.18) * mm});
            skLineSegment(sketch, "E76.56.0", {"start": v(34.14, 8.73) * mm, "end": v(33.96, 8.3) * mm});
            skLineSegment(sketch, "E76.56.1", {"start": v(34.25, 7.94) * mm, "end": v(33.8, 7.87) * mm});
            skLineSegment(sketch, "E76.56.2", {"start": v(33.8, 7.87) * mm, "end": v(33.63, 7.44) * mm});
            skLineSegment(sketch, "E76.56.3", {"start": v(33.96, 8.3) * mm, "end": v(34.25, 7.94) * mm});
            skLineSegment(sketch, "E76.57.0", {"start": v(33.63, 7.44) * mm, "end": v(33.48, 7) * mm});
            skLineSegment(sketch, "E76.57.1", {"start": v(33.79, 6.67) * mm, "end": v(33.34, 6.57) * mm});
            skLineSegment(sketch, "E76.57.2", {"start": v(33.34, 6.57) * mm, "end": v(33.2, 6.13) * mm});
            skLineSegment(sketch, "E76.57.3", {"start": v(33.48, 7) * mm, "end": v(33.79, 6.67) * mm});
            skLineSegment(sketch, "E76.58.0", {"start": v(33.2, 6.13) * mm, "end": v(33.08, 5.69) * mm});
            skLineSegment(sketch, "E76.58.1", {"start": v(33.4, 5.36) * mm, "end": v(32.97, 5.24) * mm});
            skLineSegment(sketch, "E76.58.2", {"start": v(32.97, 5.24) * mm, "end": v(32.86, 4.8) * mm});
            skLineSegment(sketch, "E76.58.3", {"start": v(33.08, 5.69) * mm, "end": v(33.4, 5.36) * mm});
            skLineSegment(sketch, "E76.59.0", {"start": v(32.86, 4.8) * mm, "end": v(32.76, 4.34) * mm});
            skLineSegment(sketch, "E76.59.1", {"start": v(33.11, 4.04) * mm, "end": v(32.68, 3.9) * mm});
            skLineSegment(sketch, "E76.59.2", {"start": v(32.68, 3.9) * mm, "end": v(32.6, 3.44) * mm});
            skLineSegment(sketch, "E76.59.3", {"start": v(32.76, 4.34) * mm, "end": v(33.11, 4.04) * mm});
            skLineSegment(sketch, "E76.60.0", {"start": v(32.6, 3.44) * mm, "end": v(32.53, 2.98) * mm});
            skLineSegment(sketch, "E76.60.1", {"start": v(32.9, 2.7) * mm, "end": v(32.48, 2.53) * mm});
            skLineSegment(sketch, "E76.60.2", {"start": v(32.48, 2.53) * mm, "end": v(32.43, 2.07) * mm});
            skLineSegment(sketch, "E76.60.3", {"start": v(32.53, 2.98) * mm, "end": v(32.9, 2.7) * mm});
            skLineSegment(sketch, "E76.61.0", {"start": v(32.43, 2.07) * mm, "end": v(32.4, 1.6) * mm});
            skLineSegment(sketch, "E76.61.1", {"start": v(32.77, 1.35) * mm, "end": v(32.36, 1.15) * mm});
            skLineSegment(sketch, "E76.61.2", {"start": v(32.36, 1.15) * mm, "end": v(32.34, 0.7) * mm});
            skLineSegment(sketch, "E76.61.3", {"start": v(32.4, 1.6) * mm, "end": v(32.77, 1.35) * mm});
            skLineSegment(sketch, "E76.62.0", {"start": v(32.34, 0.7) * mm, "end": v(32.33, 0.23) * mm});
            skLineSegment(sketch, "E76.62.1", {"start": v(32.73, 0) * mm, "end": v(32.33, -0.23) * mm});
            skLineSegment(sketch, "E76.62.2", {"start": v(32.33, -0.23) * mm, "end": v(32.34, -0.7) * mm});
            skLineSegment(sketch, "E76.62.3", {"start": v(32.33, 0.23) * mm, "end": v(32.73, 0) * mm});
            skLineSegment(sketch, "E76.63.0", {"start": v(32.34, -0.7) * mm, "end": v(32.36, -1.15) * mm});
            skLineSegment(sketch, "E76.63.1", {"start": v(32.77, -1.35) * mm, "end": v(32.4, -1.6) * mm});
            skLineSegment(sketch, "E76.63.2", {"start": v(32.4, -1.6) * mm, "end": v(32.43, -2.07) * mm});
            skLineSegment(sketch, "E76.63.3", {"start": v(32.36, -1.15) * mm, "end": v(32.77, -1.35) * mm});
            skLineSegment(sketch, "E76.64.0", {"start": v(32.43, -2.07) * mm, "end": v(32.48, -2.53) * mm});
            skLineSegment(sketch, "E76.64.1", {"start": v(32.9, -2.7) * mm, "end": v(32.53, -2.98) * mm});
            skLineSegment(sketch, "E76.64.2", {"start": v(32.53, -2.98) * mm, "end": v(32.6, -3.44) * mm});
            skLineSegment(sketch, "E76.64.3", {"start": v(32.48, -2.53) * mm, "end": v(32.9, -2.7) * mm});
            skLineSegment(sketch, "E76.65.0", {"start": v(32.6, -3.44) * mm, "end": v(32.68, -3.9) * mm});
            skLineSegment(sketch, "E76.65.1", {"start": v(33.11, -4.04) * mm, "end": v(32.76, -4.34) * mm});
            skLineSegment(sketch, "E76.65.2", {"start": v(32.76, -4.34) * mm, "end": v(32.86, -4.8) * mm});
            skLineSegment(sketch, "E76.65.3", {"start": v(32.68, -3.9) * mm, "end": v(33.11, -4.04) * mm});
            skLineSegment(sketch, "E76.66.0", {"start": v(32.86, -4.8) * mm, "end": v(32.97, -5.24) * mm});
            skLineSegment(sketch, "E76.66.1", {"start": v(33.4, -5.36) * mm, "end": v(33.08, -5.69) * mm});
            skLineSegment(sketch, "E76.66.2", {"start": v(33.08, -5.69) * mm, "end": v(33.2, -6.13) * mm});
            skLineSegment(sketch, "E76.66.3", {"start": v(32.97, -5.24) * mm, "end": v(33.4, -5.36) * mm});
            skLineSegment(sketch, "E76.74.0", {"start": v(37.82, -14.53) * mm, "end": v(38.13, -14.87) * mm});
            skLineSegment(sketch, "E76.74.1", {"start": v(38.58, -14.77) * mm, "end": v(38.44, -15.2) * mm});
            skLineSegment(sketch, "E76.74.2", {"start": v(38.44, -15.2) * mm, "end": v(38.77, -15.54) * mm});
            skLineSegment(sketch, "E76.74.3", {"start": v(38.13, -14.87) * mm, "end": v(38.58, -14.77) * mm});
            skLineSegment(sketch, "E76.75.0", {"start": v(38.77, -15.54) * mm, "end": v(39.1, -15.86) * mm});
            skLineSegment(sketch, "E76.75.1", {"start": v(39.54, -15.72) * mm, "end": v(39.43, -16.17) * mm});
            skLineSegment(sketch, "E76.75.2", {"start": v(39.43, -16.17) * mm, "end": v(39.77, -16.48) * mm});
            skLineSegment(sketch, "E76.75.3", {"start": v(39.1, -15.86) * mm, "end": v(39.54, -15.72) * mm});
            skLineSegment(sketch, "E76.76.0", {"start": v(39.77, -16.48) * mm, "end": v(40.12, -16.78) * mm});
            skLineSegment(sketch, "E76.76.1", {"start": v(40.55, -16.62) * mm, "end": v(40.48, -17.07) * mm});
            skLineSegment(sketch, "E76.76.2", {"start": v(40.48, -17.07) * mm, "end": v(40.84, -17.36) * mm});
            skLineSegment(sketch, "E76.76.3", {"start": v(40.12, -16.78) * mm, "end": v(40.55, -16.62) * mm});
            skLineSegment(sketch, "E76.77.0", {"start": v(40.84, -17.36) * mm, "end": v(41.2, -17.64) * mm});
            skLineSegment(sketch, "E76.77.1", {"start": v(41.62, -17.45) * mm, "end": v(41.58, -17.9) * mm});
            skLineSegment(sketch, "E76.77.2", {"start": v(41.58, -17.9) * mm, "end": v(41.95, -18.17) * mm});
            skLineSegment(sketch, "E76.77.3", {"start": v(41.2, -17.64) * mm, "end": v(41.62, -17.45) * mm});
            skLineSegment(sketch, "E76.78.0", {"start": v(41.95, -18.17) * mm, "end": v(42.34, -18.43) * mm});
            skLineSegment(sketch, "E76.78.1", {"start": v(42.74, -18.21) * mm, "end": v(42.72, -18.67) * mm});
            skLineSegment(sketch, "E76.78.2", {"start": v(42.72, -18.67) * mm, "end": v(43.12, -18.91) * mm});
            skLineSegment(sketch, "E76.78.3", {"start": v(42.34, -18.43) * mm, "end": v(42.74, -18.21) * mm});
            skLineSegment(sketch, "E76.79.0", {"start": v(43.12, -18.91) * mm, "end": v(43.52, -19.14) * mm});
            skLineSegment(sketch, "E76.79.1", {"start": v(43.91, -18.9) * mm, "end": v(43.92, -19.36) * mm});
            skLineSegment(sketch, "E76.79.2", {"start": v(43.92, -19.36) * mm, "end": v(44.33, -19.58) * mm});
            skLineSegment(sketch, "E76.79.3", {"start": v(43.52, -19.14) * mm, "end": v(43.91, -18.9) * mm});
            skLineSegment(sketch, "E76.80.0", {"start": v(44.33, -19.58) * mm, "end": v(44.74, -19.78) * mm});
            skLineSegment(sketch, "E76.80.1", {"start": v(45.12, -19.52) * mm, "end": v(45.16, -19.98) * mm});
            skLineSegment(sketch, "E76.80.2", {"start": v(45.16, -19.98) * mm, "end": v(45.58, -20.16) * mm});
            skLineSegment(sketch, "E76.80.3", {"start": v(44.74, -19.78) * mm, "end": v(45.12, -19.52) * mm});
            skLineSegment(sketch, "E76.81.0", {"start": v(45.58, -20.16) * mm, "end": v(46, -20.34) * mm});
            skLineSegment(sketch, "E76.81.1", {"start": v(46.36, -20.06) * mm, "end": v(46.43, -20.51) * mm});
            skLineSegment(sketch, "E76.81.2", {"start": v(46.43, -20.51) * mm, "end": v(46.86, -20.67) * mm});
            skLineSegment(sketch, "E76.81.3", {"start": v(46, -20.34) * mm, "end": v(46.36, -20.06) * mm});
            skLineSegment(sketch, "E76.82.0", {"start": v(46.86, -20.67) * mm, "end": v(47.3, -20.82) * mm});
            skLineSegment(sketch, "E76.82.1", {"start": v(47.64, -20.52) * mm, "end": v(47.73, -20.97) * mm});
            skLineSegment(sketch, "E76.82.2", {"start": v(47.73, -20.97) * mm, "end": v(48.17, -21.1) * mm});
            skLineSegment(sketch, "E76.82.3", {"start": v(47.3, -20.82) * mm, "end": v(47.64, -20.52) * mm});
            skLineSegment(sketch, "E76.83.0", {"start": v(48.17, -21.1) * mm, "end": v(48.62, -21.22) * mm});
            skLineSegment(sketch, "E76.83.1", {"start": v(48.94, -20.9) * mm, "end": v(49.06, -21.34) * mm});
            skLineSegment(sketch, "E76.83.2", {"start": v(49.06, -21.34) * mm, "end": v(49.5, -21.44) * mm});
            skLineSegment(sketch, "E76.83.3", {"start": v(48.62, -21.22) * mm, "end": v(48.94, -20.9) * mm});
            skLineSegment(sketch, "E76.84.0", {"start": v(49.5, -21.44) * mm, "end": v(49.96, -21.54) * mm});
            skLineSegment(sketch, "E76.84.1", {"start": v(50.26, -21.19) * mm, "end": v(50.41, -21.62) * mm});
            skLineSegment(sketch, "E76.84.2", {"start": v(50.41, -21.62) * mm, "end": v(50.87, -21.7) * mm});
            skLineSegment(sketch, "E76.84.3", {"start": v(49.96, -21.54) * mm, "end": v(50.26, -21.19) * mm});
            skLineSegment(sketch, "E76.85.0", {"start": v(50.87, -21.7) * mm, "end": v(51.32, -21.77) * mm});
            skLineSegment(sketch, "E76.85.1", {"start": v(51.6, -21.4) * mm, "end": v(51.78, -21.83) * mm});
            skLineSegment(sketch, "E76.85.2", {"start": v(51.78, -21.83) * mm, "end": v(52.23, -21.87) * mm});
            skLineSegment(sketch, "E76.85.3", {"start": v(51.32, -21.77) * mm, "end": v(51.6, -21.4) * mm});
            skLineSegment(sketch, "E76.86.0", {"start": v(52.23, -21.87) * mm, "end": v(52.7, -21.91) * mm});
            skLineSegment(sketch, "E76.86.1", {"start": v(52.95, -21.53) * mm, "end": v(53.15, -21.94) * mm});
            skLineSegment(sketch, "E76.86.2", {"start": v(53.15, -21.94) * mm, "end": v(53.61, -21.96) * mm});
            skLineSegment(sketch, "E76.86.3", {"start": v(52.7, -21.91) * mm, "end": v(52.95, -21.53) * mm});
            skLineSegment(sketch, "E76.87.0", {"start": v(53.61, -21.96) * mm, "end": v(54.07, -21.97) * mm});
            skLineSegment(sketch, "E76.87.1", {"start": v(54.3, -21.57) * mm, "end": v(54.53, -21.97) * mm});
            skLineSegment(sketch, "E76.87.2", {"start": v(54.53, -21.97) * mm, "end": v(55, -21.96) * mm});
            skLineSegment(sketch, "E76.87.3", {"start": v(54.07, -21.97) * mm, "end": v(54.3, -21.57) * mm});
            skLineSegment(sketch, "E76.88.0", {"start": v(55, -21.96) * mm, "end": v(55.45, -21.94) * mm});
            skLineSegment(sketch, "E76.88.1", {"start": v(55.66, -21.53) * mm, "end": v(55.91, -21.91) * mm});
            skLineSegment(sketch, "E76.88.2", {"start": v(55.91, -21.91) * mm, "end": v(56.37, -21.87) * mm});
            skLineSegment(sketch, "E76.88.3", {"start": v(55.45, -21.94) * mm, "end": v(55.66, -21.53) * mm});
            skLineSegment(sketch, "E76.89.0", {"start": v(56.37, -21.87) * mm, "end": v(56.83, -21.83) * mm});
            skLineSegment(sketch, "E76.89.1", {"start": v(57, -21.4) * mm, "end": v(57.28, -21.77) * mm});
            skLineSegment(sketch, "E76.89.2", {"start": v(57.28, -21.77) * mm, "end": v(57.74, -21.7) * mm});
            skLineSegment(sketch, "E76.89.3", {"start": v(56.83, -21.83) * mm, "end": v(57, -21.4) * mm});
            skLineSegment(sketch, "E76.90.0", {"start": v(57.74, -21.7) * mm, "end": v(58.2, -21.62) * mm});
            skLineSegment(sketch, "E76.90.1", {"start": v(58.34, -21.19) * mm, "end": v(58.65, -21.54) * mm});
            skLineSegment(sketch, "E76.90.2", {"start": v(58.65, -21.54) * mm, "end": v(59.1, -21.44) * mm});
            skLineSegment(sketch, "E76.90.3", {"start": v(58.2, -21.62) * mm, "end": v(58.34, -21.19) * mm});
            skPoint(sketch, "E76.center", {"position": v(54.3, 0) * mm});
            skLineSegment(sketch, "E76.anchor2", {"start": v(54.3, 0) * mm, "end": v(57.74, -21.7) * mm, "construction": true});
            skArc(sketch, "E77", {"start": v(38.77, 15.54) * mm, "mid": v(33.02, 5.46) * mm, "end": v(33.2, -6.13) * mm, "construction": true});
            skArc(sketch, "E78", {"start": v(49.5, 21.44) * mm, "mid": v(43.72, 19.25) * mm, "end": v(38.77, 15.54) * mm});
            skArc(sketch, "E79", {"start": v(75.4, 6.13) * mm, "mid": v(73.56, 10.58) * mm, "end": v(70.78, 14.53) * mm});
            skArc(sketch, "E80", {"start": v(59.1, -21.44) * mm, "mid": v(64.89, -19.25) * mm, "end": v(69.84, -15.54) * mm});
            skArc(sketch, "E81", {"start": v(33.2, -6.13) * mm, "mid": v(35.05, -10.58) * mm, "end": v(37.82, -14.53) * mm});
            skLineSegment(sketch, "E82", {"start": v(-50.8, 54.3) * mm, "end": v(0, 54.3) * mm, "construction": true});
            skLineSegment(sketch, "E83", {"start": v(0, 54.3) * mm, "end": v(15.54, 38.77) * mm, "construction": true});
            skLineSegment(sketch, "E84", {"start": v(0, 54.3) * mm, "end": v(15.86, 39.1) * mm, "construction": true});
            skLineSegment(sketch, "E85", {"start": v(0, 54.3) * mm, "end": v(16.17, 39.43) * mm, "construction": true});
            skLineSegment(sketch, "E86", {"start": v(0, 54.3) * mm, "end": v(16.48, 39.77) * mm, "construction": true});
            skLineSegment(sketch, "E87", {"start": v(15.54, 38.77) * mm, "end": v(15.86, 39.1) * mm});
            skLineSegment(sketch, "E88", {"start": v(15.86, 39.1) * mm, "end": v(15.72, 39.54) * mm});
            skLineSegment(sketch, "E89", {"start": v(15.72, 39.54) * mm, "end": v(16.17, 39.43) * mm});
            skLineSegment(sketch, "E90", {"start": v(16.17, 39.43) * mm, "end": v(16.48, 39.77) * mm});
            skLineSegment(sketch, "E91", {"start": v(0, 54.3) * mm, "end": v(0, 32.33) * mm, "construction": true});
            skLineSegment(sketch, "E92.1.0", {"start": v(16.48, 39.77) * mm, "end": v(16.78, 40.12) * mm});
            skLineSegment(sketch, "E92.1.1", {"start": v(16.62, 40.55) * mm, "end": v(17.07, 40.48) * mm});
            skLineSegment(sketch, "E92.1.2", {"start": v(17.07, 40.48) * mm, "end": v(17.36, 40.84) * mm});
            skLineSegment(sketch, "E92.1.3", {"start": v(16.78, 40.12) * mm, "end": v(16.62, 40.55) * mm});
            skLineSegment(sketch, "E92.2.0", {"start": v(17.36, 40.84) * mm, "end": v(17.64, 41.2) * mm});
            skLineSegment(sketch, "E92.2.1", {"start": v(17.45, 41.62) * mm, "end": v(17.9, 41.58) * mm});
            skLineSegment(sketch, "E92.2.2", {"start": v(17.9, 41.58) * mm, "end": v(18.17, 41.95) * mm});
            skLineSegment(sketch, "E92.2.3", {"start": v(17.64, 41.2) * mm, "end": v(17.45, 41.62) * mm});
            skLineSegment(sketch, "E92.3.0", {"start": v(18.17, 41.95) * mm, "end": v(18.43, 42.34) * mm});
            skLineSegment(sketch, "E92.3.1", {"start": v(18.21, 42.74) * mm, "end": v(18.67, 42.72) * mm});
            skLineSegment(sketch, "E92.3.2", {"start": v(18.67, 42.72) * mm, "end": v(18.91, 43.12) * mm});
            skLineSegment(sketch, "E92.3.3", {"start": v(18.43, 42.34) * mm, "end": v(18.21, 42.74) * mm});
            skLineSegment(sketch, "E92.4.0", {"start": v(18.91, 43.12) * mm, "end": v(19.14, 43.52) * mm});
            skLineSegment(sketch, "E92.4.1", {"start": v(18.9, 43.91) * mm, "end": v(19.36, 43.92) * mm});
            skLineSegment(sketch, "E92.4.2", {"start": v(19.36, 43.92) * mm, "end": v(19.58, 44.33) * mm});
            skLineSegment(sketch, "E92.4.3", {"start": v(19.14, 43.52) * mm, "end": v(18.9, 43.91) * mm});
            skLineSegment(sketch, "E92.5.0", {"start": v(19.58, 44.33) * mm, "end": v(19.78, 44.74) * mm});
            skLineSegment(sketch, "E92.5.1", {"start": v(19.52, 45.12) * mm, "end": v(19.98, 45.16) * mm});
            skLineSegment(sketch, "E92.5.2", {"start": v(19.98, 45.16) * mm, "end": v(20.16, 45.58) * mm});
            skLineSegment(sketch, "E92.5.3", {"start": v(19.78, 44.74) * mm, "end": v(19.52, 45.12) * mm});
            skLineSegment(sketch, "E92.6.0", {"start": v(20.16, 45.58) * mm, "end": v(20.34, 46) * mm});
            skLineSegment(sketch, "E92.6.1", {"start": v(20.06, 46.36) * mm, "end": v(20.51, 46.43) * mm});
            skLineSegment(sketch, "E92.6.2", {"start": v(20.51, 46.43) * mm, "end": v(20.67, 46.86) * mm});
            skLineSegment(sketch, "E92.6.3", {"start": v(20.34, 46) * mm, "end": v(20.06, 46.36) * mm});
            skLineSegment(sketch, "E92.7.0", {"start": v(20.67, 46.86) * mm, "end": v(20.82, 47.3) * mm});
            skLineSegment(sketch, "E92.7.1", {"start": v(20.52, 47.64) * mm, "end": v(20.97, 47.73) * mm});
            skLineSegment(sketch, "E92.7.2", {"start": v(20.97, 47.73) * mm, "end": v(21.1, 48.17) * mm});
            skLineSegment(sketch, "E92.7.3", {"start": v(20.82, 47.3) * mm, "end": v(20.52, 47.64) * mm});
            skLineSegment(sketch, "E92.8.0", {"start": v(21.1, 48.17) * mm, "end": v(21.22, 48.62) * mm});
            skLineSegment(sketch, "E92.8.1", {"start": v(20.9, 48.94) * mm, "end": v(21.34, 49.06) * mm});
            skLineSegment(sketch, "E92.8.2", {"start": v(21.34, 49.06) * mm, "end": v(21.44, 49.5) * mm});
            skLineSegment(sketch, "E92.8.3", {"start": v(21.22, 48.62) * mm, "end": v(20.9, 48.94) * mm});
            skLineSegment(sketch, "E92.9.0", {"start": v(21.44, 49.5) * mm, "end": v(21.54, 49.96) * mm});
            skLineSegment(sketch, "E92.9.1", {"start": v(21.19, 50.26) * mm, "end": v(21.62, 50.41) * mm});
            skLineSegment(sketch, "E92.9.2", {"start": v(21.62, 50.41) * mm, "end": v(21.7, 50.87) * mm});
            skLineSegment(sketch, "E92.9.3", {"start": v(21.54, 49.96) * mm, "end": v(21.19, 50.26) * mm});
            skLineSegment(sketch, "E92.10.0", {"start": v(21.7, 50.87) * mm, "end": v(21.77, 51.32) * mm});
            skLineSegment(sketch, "E92.10.1", {"start": v(21.4, 51.6) * mm, "end": v(21.83, 51.78) * mm});
            skLineSegment(sketch, "E92.10.2", {"start": v(21.83, 51.78) * mm, "end": v(21.87, 52.23) * mm});
            skLineSegment(sketch, "E92.10.3", {"start": v(21.77, 51.32) * mm, "end": v(21.4, 51.6) * mm});
            skLineSegment(sketch, "E92.11.0", {"start": v(21.87, 52.23) * mm, "end": v(21.91, 52.7) * mm});
            skLineSegment(sketch, "E92.11.1", {"start": v(21.53, 52.95) * mm, "end": v(21.94, 53.15) * mm});
            skLineSegment(sketch, "E92.11.2", {"start": v(21.94, 53.15) * mm, "end": v(21.96, 53.61) * mm});
            skLineSegment(sketch, "E92.11.3", {"start": v(21.91, 52.7) * mm, "end": v(21.53, 52.95) * mm});
            skLineSegment(sketch, "E92.12.0", {"start": v(21.96, 53.61) * mm, "end": v(21.97, 54.07) * mm});
            skLineSegment(sketch, "E92.12.1", {"start": v(21.57, 54.3) * mm, "end": v(21.97, 54.53) * mm});
            skLineSegment(sketch, "E92.12.2", {"start": v(21.97, 54.53) * mm, "end": v(21.96, 55) * mm});
            skLineSegment(sketch, "E92.12.3", {"start": v(21.97, 54.07) * mm, "end": v(21.57, 54.3) * mm});
            skLineSegment(sketch, "E92.13.0", {"start": v(21.96, 55) * mm, "end": v(21.94, 55.45) * mm});
            skLineSegment(sketch, "E92.13.1", {"start": v(21.53, 55.66) * mm, "end": v(21.91, 55.91) * mm});
            skLineSegment(sketch, "E92.13.2", {"start": v(21.91, 55.91) * mm, "end": v(21.87, 56.37) * mm});
            skLineSegment(sketch, "E92.13.3", {"start": v(21.94, 55.45) * mm, "end": v(21.53, 55.66) * mm});
            skLineSegment(sketch, "E92.14.0", {"start": v(21.87, 56.37) * mm, "end": v(21.83, 56.83) * mm});
            skLineSegment(sketch, "E92.14.1", {"start": v(21.4, 57) * mm, "end": v(21.77, 57.28) * mm});
            skLineSegment(sketch, "E92.14.2", {"start": v(21.77, 57.28) * mm, "end": v(21.7, 57.74) * mm});
            skLineSegment(sketch, "E92.14.3", {"start": v(21.83, 56.83) * mm, "end": v(21.4, 57) * mm});
            skLineSegment(sketch, "E92.15.0", {"start": v(21.7, 57.74) * mm, "end": v(21.62, 58.2) * mm});
            skLineSegment(sketch, "E92.15.1", {"start": v(21.19, 58.34) * mm, "end": v(21.54, 58.65) * mm});
            skLineSegment(sketch, "E92.15.2", {"start": v(21.54, 58.65) * mm, "end": v(21.44, 59.1) * mm});
            skLineSegment(sketch, "E92.15.3", {"start": v(21.62, 58.2) * mm, "end": v(21.19, 58.34) * mm});
            skLineSegment(sketch, "E92.16.0", {"start": v(21.44, 59.1) * mm, "end": v(21.34, 59.54) * mm});
            skLineSegment(sketch, "E92.16.1", {"start": v(20.9, 59.67) * mm, "end": v(21.22, 59.99) * mm});
            skLineSegment(sketch, "E92.16.2", {"start": v(21.22, 59.99) * mm, "end": v(21.1, 60.43) * mm});
            skLineSegment(sketch, "E92.16.3", {"start": v(21.34, 59.54) * mm, "end": v(20.9, 59.67) * mm});
            skLineSegment(sketch, "E92.24.0", {"start": v(16.48, 68.83) * mm, "end": v(16.17, 69.17) * mm});
            skLineSegment(sketch, "E92.24.1", {"start": v(15.72, 69.07) * mm, "end": v(15.86, 69.5) * mm});
            skLineSegment(sketch, "E92.24.2", {"start": v(15.86, 69.5) * mm, "end": v(15.54, 69.84) * mm});
            skLineSegment(sketch, "E92.24.3", {"start": v(16.17, 69.17) * mm, "end": v(15.72, 69.07) * mm});
            skLineSegment(sketch, "E92.25.0", {"start": v(15.54, 69.84) * mm, "end": v(15.2, 70.16) * mm});
            skLineSegment(sketch, "E92.25.1", {"start": v(14.77, 70.03) * mm, "end": v(14.87, 70.48) * mm});
            skLineSegment(sketch, "E92.25.2", {"start": v(14.87, 70.48) * mm, "end": v(14.53, 70.78) * mm});
            skLineSegment(sketch, "E92.25.3", {"start": v(15.2, 70.16) * mm, "end": v(14.77, 70.03) * mm});
            skLineSegment(sketch, "E92.26.0", {"start": v(14.53, 70.78) * mm, "end": v(14.18, 71.08) * mm});
            skLineSegment(sketch, "E92.26.1", {"start": v(13.75, 70.92) * mm, "end": v(13.83, 71.38) * mm});
            skLineSegment(sketch, "E92.26.2", {"start": v(13.83, 71.38) * mm, "end": v(13.47, 71.66) * mm});
            skLineSegment(sketch, "E92.26.3", {"start": v(14.18, 71.08) * mm, "end": v(13.75, 70.92) * mm});
            skLineSegment(sketch, "E92.27.0", {"start": v(13.47, 71.66) * mm, "end": v(13.1, 71.94) * mm});
            skLineSegment(sketch, "E92.27.1", {"start": v(12.68, 71.75) * mm, "end": v(12.73, 72.21) * mm});
            skLineSegment(sketch, "E92.27.2", {"start": v(12.73, 72.21) * mm, "end": v(12.35, 72.47) * mm});
            skLineSegment(sketch, "E92.27.3", {"start": v(13.1, 71.94) * mm, "end": v(12.68, 71.75) * mm});
            skLineSegment(sketch, "E92.28.0", {"start": v(12.35, 72.47) * mm, "end": v(11.97, 72.73) * mm});
            skLineSegment(sketch, "E92.28.1", {"start": v(11.56, 72.52) * mm, "end": v(11.58, 72.98) * mm});
            skLineSegment(sketch, "E92.28.2", {"start": v(11.58, 72.98) * mm, "end": v(11.18, 73.21) * mm});
            skLineSegment(sketch, "E92.28.3", {"start": v(11.97, 72.73) * mm, "end": v(11.56, 72.52) * mm});
            skLineSegment(sketch, "E92.29.0", {"start": v(11.18, 73.21) * mm, "end": v(10.79, 73.44) * mm});
            skLineSegment(sketch, "E92.29.1", {"start": v(10.4, 73.2) * mm, "end": v(10.38, 73.67) * mm});
            skLineSegment(sketch, "E92.29.2", {"start": v(10.38, 73.67) * mm, "end": v(9.97, 73.88) * mm});
            skLineSegment(sketch, "E92.29.3", {"start": v(10.79, 73.44) * mm, "end": v(10.4, 73.2) * mm});
            skLineSegment(sketch, "E92.30.0", {"start": v(9.97, 73.88) * mm, "end": v(9.56, 74.08) * mm});
            skLineSegment(sketch, "E92.30.1", {"start": v(9.18, 73.82) * mm, "end": v(9.15, 74.28) * mm});
            skLineSegment(sketch, "E92.30.2", {"start": v(9.15, 74.28) * mm, "end": v(8.73, 74.47) * mm});
            skLineSegment(sketch, "E92.30.3", {"start": v(9.56, 74.08) * mm, "end": v(9.18, 73.82) * mm});
            skLineSegment(sketch, "E92.31.0", {"start": v(8.73, 74.47) * mm, "end": v(8.3, 74.64) * mm});
            skLineSegment(sketch, "E92.31.1", {"start": v(7.94, 74.36) * mm, "end": v(7.87, 74.81) * mm});
            skLineSegment(sketch, "E92.31.2", {"start": v(7.87, 74.81) * mm, "end": v(7.44, 74.97) * mm});
            skLineSegment(sketch, "E92.31.3", {"start": v(8.3, 74.64) * mm, "end": v(7.94, 74.36) * mm});
            skLineSegment(sketch, "E92.32.0", {"start": v(7.44, 74.97) * mm, "end": v(7, 75.13) * mm});
            skLineSegment(sketch, "E92.32.1", {"start": v(6.67, 74.82) * mm, "end": v(6.57, 75.27) * mm});
            skLineSegment(sketch, "E92.32.2", {"start": v(6.57, 75.27) * mm, "end": v(6.13, 75.4) * mm});
            skLineSegment(sketch, "E92.32.3", {"start": v(7, 75.13) * mm, "end": v(6.67, 74.82) * mm});
            skLineSegment(sketch, "E92.33.0", {"start": v(6.13, 75.4) * mm, "end": v(5.69, 75.52) * mm});
            skLineSegment(sketch, "E92.33.1", {"start": v(5.36, 75.2) * mm, "end": v(5.24, 75.64) * mm});
            skLineSegment(sketch, "E92.33.2", {"start": v(5.24, 75.64) * mm, "end": v(4.8, 75.74) * mm});
            skLineSegment(sketch, "E92.33.3", {"start": v(5.69, 75.52) * mm, "end": v(5.36, 75.2) * mm});
            skLineSegment(sketch, "E92.34.0", {"start": v(4.8, 75.74) * mm, "end": v(4.34, 75.84) * mm});
            skLineSegment(sketch, "E92.34.1", {"start": v(4.04, 75.5) * mm, "end": v(3.9, 75.93) * mm});
            skLineSegment(sketch, "E92.34.2", {"start": v(3.9, 75.93) * mm, "end": v(3.44, 76) * mm});
            skLineSegment(sketch, "E92.34.3", {"start": v(4.34, 75.84) * mm, "end": v(4.04, 75.5) * mm});
            skLineSegment(sketch, "E92.35.0", {"start": v(3.44, 76) * mm, "end": v(2.98, 76.07) * mm});
            skLineSegment(sketch, "E92.35.1", {"start": v(2.7, 75.7) * mm, "end": v(2.53, 76.13) * mm});
            skLineSegment(sketch, "E92.35.2", {"start": v(2.53, 76.13) * mm, "end": v(2.07, 76.18) * mm});
            skLineSegment(sketch, "E92.35.3", {"start": v(2.98, 76.07) * mm, "end": v(2.7, 75.7) * mm});
            skLineSegment(sketch, "E92.36.0", {"start": v(2.07, 76.18) * mm, "end": v(1.6, 76.21) * mm});
            skLineSegment(sketch, "E92.36.1", {"start": v(1.35, 75.83) * mm, "end": v(1.15, 76.24) * mm});
            skLineSegment(sketch, "E92.36.2", {"start": v(1.15, 76.24) * mm, "end": v(0.7, 76.26) * mm});
            skLineSegment(sketch, "E92.36.3", {"start": v(1.6, 76.21) * mm, "end": v(1.35, 75.83) * mm});
            skLineSegment(sketch, "E92.37.0", {"start": v(0.7, 76.26) * mm, "end": v(0.23, 76.27) * mm});
            skLineSegment(sketch, "E92.37.1", {"start": v(0, 75.87) * mm, "end": v(-0.23, 76.27) * mm});
            skLineSegment(sketch, "E92.37.2", {"start": v(-0.23, 76.27) * mm, "end": v(-0.7, 76.26) * mm});
            skLineSegment(sketch, "E92.37.3", {"start": v(0.23, 76.27) * mm, "end": v(0, 75.87) * mm});
            skLineSegment(sketch, "E92.38.0", {"start": v(-0.7, 76.26) * mm, "end": v(-1.15, 76.24) * mm});
            skLineSegment(sketch, "E92.38.1", {"start": v(-1.35, 75.83) * mm, "end": v(-1.6, 76.21) * mm});
            skLineSegment(sketch, "E92.38.2", {"start": v(-1.6, 76.21) * mm, "end": v(-2.07, 76.18) * mm});
            skLineSegment(sketch, "E92.38.3", {"start": v(-1.15, 76.24) * mm, "end": v(-1.35, 75.83) * mm});
            skLineSegment(sketch, "E92.39.0", {"start": v(-2.07, 76.18) * mm, "end": v(-2.53, 76.13) * mm});
            skLineSegment(sketch, "E92.39.1", {"start": v(-2.7, 75.7) * mm, "end": v(-2.98, 76.07) * mm});
            skLineSegment(sketch, "E92.39.2", {"start": v(-2.98, 76.07) * mm, "end": v(-3.44, 76) * mm});
            skLineSegment(sketch, "E92.39.3", {"start": v(-2.53, 76.13) * mm, "end": v(-2.7, 75.7) * mm});
            skLineSegment(sketch, "E92.40.0", {"start": v(-3.44, 76) * mm, "end": v(-3.9, 75.93) * mm});
            skLineSegment(sketch, "E92.40.1", {"start": v(-4.04, 75.5) * mm, "end": v(-4.34, 75.84) * mm});
            skLineSegment(sketch, "E92.40.2", {"start": v(-4.34, 75.84) * mm, "end": v(-4.8, 75.74) * mm});
            skLineSegment(sketch, "E92.40.3", {"start": v(-3.9, 75.93) * mm, "end": v(-4.04, 75.5) * mm});
            skLineSegment(sketch, "E92.50.0", {"start": v(-15.54, 69.84) * mm, "end": v(-15.86, 69.5) * mm});
            skLineSegment(sketch, "E92.50.1", {"start": v(-15.72, 69.07) * mm, "end": v(-16.17, 69.17) * mm});
            skLineSegment(sketch, "E92.50.2", {"start": v(-16.17, 69.17) * mm, "end": v(-16.48, 68.83) * mm});
            skLineSegment(sketch, "E92.50.3", {"start": v(-15.86, 69.5) * mm, "end": v(-15.72, 69.07) * mm});
            skLineSegment(sketch, "E92.51.0", {"start": v(-16.48, 68.83) * mm, "end": v(-16.78, 68.48) * mm});
            skLineSegment(sketch, "E92.51.1", {"start": v(-16.62, 68.05) * mm, "end": v(-17.07, 68.13) * mm});
            skLineSegment(sketch, "E92.51.2", {"start": v(-17.07, 68.13) * mm, "end": v(-17.36, 67.77) * mm});
            skLineSegment(sketch, "E92.51.3", {"start": v(-16.78, 68.48) * mm, "end": v(-16.62, 68.05) * mm});
            skLineSegment(sketch, "E92.52.0", {"start": v(-17.36, 67.77) * mm, "end": v(-17.64, 67.4) * mm});
            skLineSegment(sketch, "E92.52.1", {"start": v(-17.45, 66.98) * mm, "end": v(-17.9, 67.03) * mm});
            skLineSegment(sketch, "E92.52.2", {"start": v(-17.9, 67.03) * mm, "end": v(-18.17, 66.65) * mm});
            skLineSegment(sketch, "E92.52.3", {"start": v(-17.64, 67.4) * mm, "end": v(-17.45, 66.98) * mm});
            skLineSegment(sketch, "E92.53.0", {"start": v(-18.17, 66.65) * mm, "end": v(-18.43, 66.27) * mm});
            skLineSegment(sketch, "E92.53.1", {"start": v(-18.21, 65.86) * mm, "end": v(-18.67, 65.88) * mm});
            skLineSegment(sketch, "E92.53.2", {"start": v(-18.67, 65.88) * mm, "end": v(-18.91, 65.49) * mm});
            skLineSegment(sketch, "E92.53.3", {"start": v(-18.43, 66.27) * mm, "end": v(-18.21, 65.86) * mm});
            skLineSegment(sketch, "E92.54.0", {"start": v(-18.91, 65.49) * mm, "end": v(-19.14, 65.09) * mm});
            skLineSegment(sketch, "E92.54.1", {"start": v(-18.9, 64.7) * mm, "end": v(-19.36, 64.68) * mm});
            skLineSegment(sketch, "E92.54.2", {"start": v(-19.36, 64.68) * mm, "end": v(-19.58, 64.28) * mm});
            skLineSegment(sketch, "E92.54.3", {"start": v(-19.14, 65.09) * mm, "end": v(-18.9, 64.7) * mm});
            skLineSegment(sketch, "E92.55.0", {"start": v(-19.58, 64.28) * mm, "end": v(-19.78, 63.86) * mm});
            skLineSegment(sketch, "E92.55.1", {"start": v(-19.52, 63.49) * mm, "end": v(-19.98, 63.45) * mm});
            skLineSegment(sketch, "E92.55.2", {"start": v(-19.98, 63.45) * mm, "end": v(-20.16, 63.03) * mm});
            skLineSegment(sketch, "E92.55.3", {"start": v(-19.78, 63.86) * mm, "end": v(-19.52, 63.49) * mm});
            skLineSegment(sketch, "E92.56.0", {"start": v(-20.16, 63.03) * mm, "end": v(-20.34, 62.6) * mm});
            skLineSegment(sketch, "E92.56.1", {"start": v(-20.06, 62.24) * mm, "end": v(-20.51, 62.18) * mm});
            skLineSegment(sketch, "E92.56.2", {"start": v(-20.51, 62.18) * mm, "end": v(-20.67, 61.74) * mm});
            skLineSegment(sketch, "E92.56.3", {"start": v(-20.34, 62.6) * mm, "end": v(-20.06, 62.24) * mm});
            skLineSegment(sketch, "E92.57.0", {"start": v(-20.67, 61.74) * mm, "end": v(-20.82, 61.31) * mm});
            skLineSegment(sketch, "E92.57.1", {"start": v(-20.52, 60.97) * mm, "end": v(-20.97, 60.87) * mm});
            skLineSegment(sketch, "E92.57.2", {"start": v(-20.97, 60.87) * mm, "end": v(-21.1, 60.43) * mm});
            skLineSegment(sketch, "E92.57.3", {"start": v(-20.82, 61.31) * mm, "end": v(-20.52, 60.97) * mm});
            skLineSegment(sketch, "E92.58.0", {"start": v(-21.1, 60.43) * mm, "end": v(-21.22, 59.99) * mm});
            skLineSegment(sketch, "E92.58.1", {"start": v(-20.9, 59.67) * mm, "end": v(-21.34, 59.54) * mm});
            skLineSegment(sketch, "E92.58.2", {"start": v(-21.34, 59.54) * mm, "end": v(-21.44, 59.1) * mm});
            skLineSegment(sketch, "E92.58.3", {"start": v(-21.22, 59.99) * mm, "end": v(-20.9, 59.67) * mm});
            skLineSegment(sketch, "E92.59.0", {"start": v(-21.44, 59.1) * mm, "end": v(-21.54, 58.65) * mm});
            skLineSegment(sketch, "E92.59.1", {"start": v(-21.19, 58.34) * mm, "end": v(-21.62, 58.2) * mm});
            skLineSegment(sketch, "E92.59.2", {"start": v(-21.62, 58.2) * mm, "end": v(-21.7, 57.74) * mm});
            skLineSegment(sketch, "E92.59.3", {"start": v(-21.54, 58.65) * mm, "end": v(-21.19, 58.34) * mm});
            skLineSegment(sketch, "E92.60.0", {"start": v(-21.7, 57.74) * mm, "end": v(-21.77, 57.28) * mm});
            skLineSegment(sketch, "E92.60.1", {"start": v(-21.4, 57) * mm, "end": v(-21.83, 56.83) * mm});
            skLineSegment(sketch, "E92.60.2", {"start": v(-21.83, 56.83) * mm, "end": v(-21.87, 56.37) * mm});
            skLineSegment(sketch, "E92.60.3", {"start": v(-21.77, 57.28) * mm, "end": v(-21.4, 57) * mm});
            skLineSegment(sketch, "E92.61.0", {"start": v(-21.87, 56.37) * mm, "end": v(-21.91, 55.91) * mm});
            skLineSegment(sketch, "E92.61.1", {"start": v(-21.53, 55.66) * mm, "end": v(-21.94, 55.45) * mm});
            skLineSegment(sketch, "E92.61.2", {"start": v(-21.94, 55.45) * mm, "end": v(-21.96, 55) * mm});
            skLineSegment(sketch, "E92.61.3", {"start": v(-21.91, 55.91) * mm, "end": v(-21.53, 55.66) * mm});
            skLineSegment(sketch, "E92.62.0", {"start": v(-21.96, 55) * mm, "end": v(-21.97, 54.53) * mm});
            skLineSegment(sketch, "E92.62.1", {"start": v(-21.57, 54.3) * mm, "end": v(-21.97, 54.07) * mm});
            skLineSegment(sketch, "E92.62.2", {"start": v(-21.97, 54.07) * mm, "end": v(-21.96, 53.61) * mm});
            skLineSegment(sketch, "E92.62.3", {"start": v(-21.97, 54.53) * mm, "end": v(-21.57, 54.3) * mm});
            skLineSegment(sketch, "E92.63.0", {"start": v(-21.96, 53.61) * mm, "end": v(-21.94, 53.15) * mm});
            skLineSegment(sketch, "E92.63.1", {"start": v(-21.53, 52.95) * mm, "end": v(-21.91, 52.7) * mm});
            skLineSegment(sketch, "E92.63.2", {"start": v(-21.91, 52.7) * mm, "end": v(-21.87, 52.23) * mm});
            skLineSegment(sketch, "E92.63.3", {"start": v(-21.94, 53.15) * mm, "end": v(-21.53, 52.95) * mm});
            skLineSegment(sketch, "E92.64.0", {"start": v(-21.87, 52.23) * mm, "end": v(-21.83, 51.78) * mm});
            skLineSegment(sketch, "E92.64.1", {"start": v(-21.4, 51.6) * mm, "end": v(-21.77, 51.32) * mm});
            skLineSegment(sketch, "E92.64.2", {"start": v(-21.77, 51.32) * mm, "end": v(-21.7, 50.87) * mm});
            skLineSegment(sketch, "E92.64.3", {"start": v(-21.83, 51.78) * mm, "end": v(-21.4, 51.6) * mm});
            skLineSegment(sketch, "E92.65.0", {"start": v(-21.7, 50.87) * mm, "end": v(-21.62, 50.41) * mm});
            skLineSegment(sketch, "E92.65.1", {"start": v(-21.19, 50.26) * mm, "end": v(-21.54, 49.96) * mm});
            skLineSegment(sketch, "E92.65.2", {"start": v(-21.54, 49.96) * mm, "end": v(-21.44, 49.5) * mm});
            skLineSegment(sketch, "E92.65.3", {"start": v(-21.62, 50.41) * mm, "end": v(-21.19, 50.26) * mm});
            skLineSegment(sketch, "E92.66.0", {"start": v(-21.44, 49.5) * mm, "end": v(-21.34, 49.06) * mm});
            skLineSegment(sketch, "E92.66.1", {"start": v(-20.9, 48.94) * mm, "end": v(-21.22, 48.62) * mm});
            skLineSegment(sketch, "E92.66.2", {"start": v(-21.22, 48.62) * mm, "end": v(-21.1, 48.17) * mm});
            skLineSegment(sketch, "E92.66.3", {"start": v(-21.34, 49.06) * mm, "end": v(-20.9, 48.94) * mm});
            skLineSegment(sketch, "E92.74.0", {"start": v(-16.48, 39.77) * mm, "end": v(-16.17, 39.43) * mm});
            skLineSegment(sketch, "E92.74.1", {"start": v(-15.72, 39.54) * mm, "end": v(-15.86, 39.1) * mm});
            skLineSegment(sketch, "E92.74.2", {"start": v(-15.86, 39.1) * mm, "end": v(-15.54, 38.77) * mm});
            skLineSegment(sketch, "E92.74.3", {"start": v(-16.17, 39.43) * mm, "end": v(-15.72, 39.54) * mm});
            skLineSegment(sketch, "E92.75.0", {"start": v(-15.54, 38.77) * mm, "end": v(-15.2, 38.44) * mm});
            skLineSegment(sketch, "E92.75.1", {"start": v(-14.77, 38.58) * mm, "end": v(-14.87, 38.13) * mm});
            skLineSegment(sketch, "E92.75.2", {"start": v(-14.87, 38.13) * mm, "end": v(-14.53, 37.82) * mm});
            skLineSegment(sketch, "E92.75.3", {"start": v(-15.2, 38.44) * mm, "end": v(-14.77, 38.58) * mm});
            skLineSegment(sketch, "E92.76.0", {"start": v(-14.53, 37.82) * mm, "end": v(-14.18, 37.52) * mm});
            skLineSegment(sketch, "E92.76.1", {"start": v(-13.75, 37.68) * mm, "end": v(-13.83, 37.23) * mm});
            skLineSegment(sketch, "E92.76.2", {"start": v(-13.83, 37.23) * mm, "end": v(-13.47, 36.94) * mm});
            skLineSegment(sketch, "E92.76.3", {"start": v(-14.18, 37.52) * mm, "end": v(-13.75, 37.68) * mm});
            skLineSegment(sketch, "E92.77.0", {"start": v(-13.47, 36.94) * mm, "end": v(-13.1, 36.66) * mm});
            skLineSegment(sketch, "E92.77.1", {"start": v(-12.68, 36.85) * mm, "end": v(-12.73, 36.4) * mm});
            skLineSegment(sketch, "E92.77.2", {"start": v(-12.73, 36.4) * mm, "end": v(-12.35, 36.13) * mm});
            skLineSegment(sketch, "E92.77.3", {"start": v(-13.1, 36.66) * mm, "end": v(-12.68, 36.85) * mm});
            skLineSegment(sketch, "E92.78.0", {"start": v(-12.35, 36.13) * mm, "end": v(-11.97, 35.88) * mm});
            skLineSegment(sketch, "E92.78.1", {"start": v(-11.56, 36.09) * mm, "end": v(-11.58, 35.63) * mm});
            skLineSegment(sketch, "E92.78.2", {"start": v(-11.58, 35.63) * mm, "end": v(-11.18, 35.4) * mm});
            skLineSegment(sketch, "E92.78.3", {"start": v(-11.97, 35.88) * mm, "end": v(-11.56, 36.09) * mm});
            skLineSegment(sketch, "E92.79.0", {"start": v(-11.18, 35.4) * mm, "end": v(-10.79, 35.16) * mm});
            skLineSegment(sketch, "E92.79.1", {"start": v(-10.4, 35.4) * mm, "end": v(-10.38, 34.94) * mm});
            skLineSegment(sketch, "E92.79.2", {"start": v(-10.38, 34.94) * mm, "end": v(-9.97, 34.73) * mm});
            skLineSegment(sketch, "E92.79.3", {"start": v(-10.79, 35.16) * mm, "end": v(-10.4, 35.4) * mm});
            skLineSegment(sketch, "E92.80.0", {"start": v(-9.97, 34.73) * mm, "end": v(-9.56, 34.52) * mm});
            skLineSegment(sketch, "E92.80.1", {"start": v(-9.18, 34.78) * mm, "end": v(-9.15, 34.33) * mm});
            skLineSegment(sketch, "E92.80.2", {"start": v(-9.15, 34.33) * mm, "end": v(-8.73, 34.14) * mm});
            skLineSegment(sketch, "E92.80.3", {"start": v(-9.56, 34.52) * mm, "end": v(-9.18, 34.78) * mm});
            skLineSegment(sketch, "E92.81.0", {"start": v(-8.73, 34.14) * mm, "end": v(-8.3, 33.96) * mm});
            skLineSegment(sketch, "E92.81.1", {"start": v(-7.94, 34.25) * mm, "end": v(-7.87, 33.8) * mm});
            skLineSegment(sketch, "E92.81.2", {"start": v(-7.87, 33.8) * mm, "end": v(-7.44, 33.63) * mm});
            skLineSegment(sketch, "E92.81.3", {"start": v(-8.3, 33.96) * mm, "end": v(-7.94, 34.25) * mm});
            skLineSegment(sketch, "E92.82.0", {"start": v(-7.44, 33.63) * mm, "end": v(-7, 33.48) * mm});
            skLineSegment(sketch, "E92.82.1", {"start": v(-6.67, 33.79) * mm, "end": v(-6.57, 33.34) * mm});
            skLineSegment(sketch, "E92.82.2", {"start": v(-6.57, 33.34) * mm, "end": v(-6.13, 33.2) * mm});
            skLineSegment(sketch, "E92.82.3", {"start": v(-7, 33.48) * mm, "end": v(-6.67, 33.79) * mm});
            skLineSegment(sketch, "E92.83.0", {"start": v(-6.13, 33.2) * mm, "end": v(-5.69, 33.08) * mm});
            skLineSegment(sketch, "E92.83.1", {"start": v(-5.36, 33.4) * mm, "end": v(-5.24, 32.97) * mm});
            skLineSegment(sketch, "E92.83.2", {"start": v(-5.24, 32.97) * mm, "end": v(-4.8, 32.86) * mm});
            skLineSegment(sketch, "E92.83.3", {"start": v(-5.69, 33.08) * mm, "end": v(-5.36, 33.4) * mm});
            skLineSegment(sketch, "E92.84.0", {"start": v(-4.8, 32.86) * mm, "end": v(-4.34, 32.76) * mm});
            skLineSegment(sketch, "E92.84.1", {"start": v(-4.04, 33.11) * mm, "end": v(-3.9, 32.68) * mm});
            skLineSegment(sketch, "E92.84.2", {"start": v(-3.9, 32.68) * mm, "end": v(-3.44, 32.6) * mm});
            skLineSegment(sketch, "E92.84.3", {"start": v(-4.34, 32.76) * mm, "end": v(-4.04, 33.11) * mm});
            skLineSegment(sketch, "E92.85.0", {"start": v(-3.44, 32.6) * mm, "end": v(-2.98, 32.53) * mm});
            skLineSegment(sketch, "E92.85.1", {"start": v(-2.7, 32.9) * mm, "end": v(-2.53, 32.48) * mm});
            skLineSegment(sketch, "E92.85.2", {"start": v(-2.53, 32.48) * mm, "end": v(-2.07, 32.43) * mm});
            skLineSegment(sketch, "E92.85.3", {"start": v(-2.98, 32.53) * mm, "end": v(-2.7, 32.9) * mm});
            skLineSegment(sketch, "E92.86.0", {"start": v(-2.07, 32.43) * mm, "end": v(-1.6, 32.4) * mm});
            skLineSegment(sketch, "E92.86.1", {"start": v(-1.35, 32.77) * mm, "end": v(-1.15, 32.36) * mm});
            skLineSegment(sketch, "E92.86.2", {"start": v(-1.15, 32.36) * mm, "end": v(-0.7, 32.34) * mm});
            skLineSegment(sketch, "E92.86.3", {"start": v(-1.6, 32.4) * mm, "end": v(-1.35, 32.77) * mm});
            skLineSegment(sketch, "E92.87.0", {"start": v(-0.7, 32.34) * mm, "end": v(-0.23, 32.33) * mm});
            skLineSegment(sketch, "E92.87.1", {"start": v(0, 32.73) * mm, "end": v(0.23, 32.33) * mm});
            skLineSegment(sketch, "E92.87.2", {"start": v(0.23, 32.33) * mm, "end": v(0.7, 32.34) * mm});
            skLineSegment(sketch, "E92.87.3", {"start": v(-0.23, 32.33) * mm, "end": v(0, 32.73) * mm});
            skLineSegment(sketch, "E92.88.0", {"start": v(0.7, 32.34) * mm, "end": v(1.15, 32.36) * mm});
            skLineSegment(sketch, "E92.88.1", {"start": v(1.35, 32.77) * mm, "end": v(1.6, 32.4) * mm});
            skLineSegment(sketch, "E92.88.2", {"start": v(1.6, 32.4) * mm, "end": v(2.07, 32.43) * mm});
            skLineSegment(sketch, "E92.88.3", {"start": v(1.15, 32.36) * mm, "end": v(1.35, 32.77) * mm});
            skLineSegment(sketch, "E92.89.0", {"start": v(2.07, 32.43) * mm, "end": v(2.53, 32.48) * mm});
            skLineSegment(sketch, "E92.89.1", {"start": v(2.7, 32.9) * mm, "end": v(2.98, 32.53) * mm});
            skLineSegment(sketch, "E92.89.2", {"start": v(2.98, 32.53) * mm, "end": v(3.44, 32.6) * mm});
            skLineSegment(sketch, "E92.89.3", {"start": v(2.53, 32.48) * mm, "end": v(2.7, 32.9) * mm});
            skLineSegment(sketch, "E92.90.0", {"start": v(3.44, 32.6) * mm, "end": v(3.9, 32.68) * mm});
            skLineSegment(sketch, "E92.90.1", {"start": v(4.04, 33.11) * mm, "end": v(4.34, 32.76) * mm});
            skLineSegment(sketch, "E92.90.2", {"start": v(4.34, 32.76) * mm, "end": v(4.8, 32.86) * mm});
            skLineSegment(sketch, "E92.90.3", {"start": v(3.9, 32.68) * mm, "end": v(4.04, 33.11) * mm});
            skPoint(sketch, "E92.center", {"position": v(0, 54.3) * mm});
            skLineSegment(sketch, "E92.anchor2", {"start": v(0, 54.3) * mm, "end": v(3.44, 32.6) * mm, "construction": true});
            skArc(sketch, "E93", {"start": v(-15.54, 69.84) * mm, "mid": v(-21.28, 59.77) * mm, "end": v(-21.1, 48.17) * mm, "construction": true});
            skArc(sketch, "E94", {"start": v(-4.8, 75.74) * mm, "mid": v(-10.58, 73.56) * mm, "end": v(-15.54, 69.84) * mm});
            skArc(sketch, "E95", {"start": v(21.1, 60.43) * mm, "mid": v(19.25, 64.89) * mm, "end": v(16.48, 68.83) * mm});
            skArc(sketch, "E96", {"start": v(4.8, 32.86) * mm, "mid": v(10.58, 35.05) * mm, "end": v(15.54, 38.77) * mm});
            skArc(sketch, "E97", {"start": v(-21.1, 48.17) * mm, "mid": v(-19.25, 43.72) * mm, "end": v(-16.48, 39.77) * mm});
            skLineSegment(sketch, "E98", {"start": v(57.8, 54.3) * mm, "end": v(108.6, 54.3) * mm, "construction": true});
            skLineSegment(sketch, "E99", {"start": v(108.6, 54.3) * mm, "end": v(130.05, 49.5) * mm, "construction": true});
            skLineSegment(sketch, "E100", {"start": v(108.6, 54.3) * mm, "end": v(130.14, 49.96) * mm, "construction": true});
            skLineSegment(sketch, "E101", {"start": v(108.6, 54.3) * mm, "end": v(130.23, 50.41) * mm, "construction": true});
            skLineSegment(sketch, "E102", {"start": v(108.6, 54.3) * mm, "end": v(130.3, 50.87) * mm, "construction": true});
            skLineSegment(sketch, "E103", {"start": v(130.05, 49.5) * mm, "end": v(130.14, 49.96) * mm});
            skLineSegment(sketch, "E104", {"start": v(130.14, 49.96) * mm, "end": v(129.8, 50.26) * mm});
            skLineSegment(sketch, "E105", {"start": v(129.8, 50.26) * mm, "end": v(130.23, 50.41) * mm});
            skLineSegment(sketch, "E106", {"start": v(130.23, 50.41) * mm, "end": v(130.3, 50.87) * mm});
            skLineSegment(sketch, "E107", {"start": v(108.6, 54.3) * mm, "end": v(108.6, 32.33) * mm, "construction": true});
            skLineSegment(sketch, "E108.1.0", {"start": v(130.3, 50.87) * mm, "end": v(130.37, 51.32) * mm});
            skLineSegment(sketch, "E108.1.1", {"start": v(130, 51.6) * mm, "end": v(130.43, 51.78) * mm});
            skLineSegment(sketch, "E108.1.2", {"start": v(130.43, 51.78) * mm, "end": v(130.48, 52.23) * mm});
            skLineSegment(sketch, "E108.1.3", {"start": v(130.37, 51.32) * mm, "end": v(130, 51.6) * mm});
            skLineSegment(sketch, "E108.2.0", {"start": v(130.48, 52.23) * mm, "end": v(130.52, 52.7) * mm});
            skLineSegment(sketch, "E108.2.1", {"start": v(130.13, 52.95) * mm, "end": v(130.55, 53.15) * mm});
            skLineSegment(sketch, "E108.2.2", {"start": v(130.55, 53.15) * mm, "end": v(130.57, 53.61) * mm});
            skLineSegment(sketch, "E108.2.3", {"start": v(130.52, 52.7) * mm, "end": v(130.13, 52.95) * mm});
            skLineSegment(sketch, "E108.3.0", {"start": v(130.57, 53.61) * mm, "end": v(130.57, 54.07) * mm});
            skLineSegment(sketch, "E108.3.1", {"start": v(130.18, 54.3) * mm, "end": v(130.57, 54.53) * mm});
            skLineSegment(sketch, "E108.3.2", {"start": v(130.57, 54.53) * mm, "end": v(130.57, 55) * mm});
            skLineSegment(sketch, "E108.3.3", {"start": v(130.57, 54.07) * mm, "end": v(130.18, 54.3) * mm});
            skLineSegment(sketch, "E108.4.0", {"start": v(130.57, 55) * mm, "end": v(130.55, 55.45) * mm});
            skLineSegment(sketch, "E108.4.1", {"start": v(130.13, 55.66) * mm, "end": v(130.52, 55.91) * mm});
            skLineSegment(sketch, "E108.4.2", {"start": v(130.52, 55.91) * mm, "end": v(130.48, 56.37) * mm});
            skLineSegment(sketch, "E108.4.3", {"start": v(130.55, 55.45) * mm, "end": v(130.13, 55.66) * mm});
            skLineSegment(sketch, "E108.5.0", {"start": v(130.48, 56.37) * mm, "end": v(130.43, 56.83) * mm});
            skLineSegment(sketch, "E108.5.1", {"start": v(130, 57) * mm, "end": v(130.37, 57.28) * mm});
            skLineSegment(sketch, "E108.5.2", {"start": v(130.37, 57.28) * mm, "end": v(130.3, 57.74) * mm});
            skLineSegment(sketch, "E108.5.3", {"start": v(130.43, 56.83) * mm, "end": v(130, 57) * mm});
            skLineSegment(sketch, "E108.6.0", {"start": v(130.3, 57.74) * mm, "end": v(130.23, 58.2) * mm});
            skLineSegment(sketch, "E108.6.1", {"start": v(129.8, 58.34) * mm, "end": v(130.14, 58.65) * mm});
            skLineSegment(sketch, "E108.6.2", {"start": v(130.14, 58.65) * mm, "end": v(130.05, 59.1) * mm});
            skLineSegment(sketch, "E108.6.3", {"start": v(130.23, 58.2) * mm, "end": v(129.8, 58.34) * mm});
            skLineSegment(sketch, "E108.7.0", {"start": v(130.05, 59.1) * mm, "end": v(129.94, 59.54) * mm});
            skLineSegment(sketch, "E108.7.1", {"start": v(129.5, 59.67) * mm, "end": v(129.83, 59.99) * mm});
            skLineSegment(sketch, "E108.7.2", {"start": v(129.83, 59.99) * mm, "end": v(129.7, 60.43) * mm});
            skLineSegment(sketch, "E108.7.3", {"start": v(129.94, 59.54) * mm, "end": v(129.5, 59.67) * mm});
            skLineSegment(sketch, "E108.8.0", {"start": v(129.7, 60.43) * mm, "end": v(129.57, 60.87) * mm});
            skLineSegment(sketch, "E108.8.1", {"start": v(129.12, 60.97) * mm, "end": v(129.43, 61.31) * mm});
            skLineSegment(sketch, "E108.8.2", {"start": v(129.43, 61.31) * mm, "end": v(129.28, 61.74) * mm});
            skLineSegment(sketch, "E108.8.3", {"start": v(129.57, 60.87) * mm, "end": v(129.12, 60.97) * mm});
            skLineSegment(sketch, "E108.9.0", {"start": v(129.28, 61.74) * mm, "end": v(129.12, 62.18) * mm});
            skLineSegment(sketch, "E108.9.1", {"start": v(128.66, 62.24) * mm, "end": v(128.95, 62.6) * mm});
            skLineSegment(sketch, "E108.9.2", {"start": v(128.95, 62.6) * mm, "end": v(128.77, 63.03) * mm});
            skLineSegment(sketch, "E108.9.3", {"start": v(129.12, 62.18) * mm, "end": v(128.66, 62.24) * mm});
            skLineSegment(sketch, "E108.10.0", {"start": v(128.77, 63.03) * mm, "end": v(128.58, 63.45) * mm});
            skLineSegment(sketch, "E108.10.1", {"start": v(128.12, 63.49) * mm, "end": v(128.39, 63.86) * mm});
            skLineSegment(sketch, "E108.10.2", {"start": v(128.39, 63.86) * mm, "end": v(128.18, 64.28) * mm});
            skLineSegment(sketch, "E108.10.3", {"start": v(128.58, 63.45) * mm, "end": v(128.12, 63.49) * mm});
            skLineSegment(sketch, "E108.11.0", {"start": v(128.18, 64.28) * mm, "end": v(127.97, 64.68) * mm});
            skLineSegment(sketch, "E108.11.1", {"start": v(127.5, 64.7) * mm, "end": v(127.75, 65.09) * mm});
            skLineSegment(sketch, "E108.11.2", {"start": v(127.75, 65.09) * mm, "end": v(127.52, 65.49) * mm});
            skLineSegment(sketch, "E108.11.3", {"start": v(127.97, 64.68) * mm, "end": v(127.5, 64.7) * mm});
            skLineSegment(sketch, "E108.12.0", {"start": v(127.52, 65.49) * mm, "end": v(127.28, 65.88) * mm});
            skLineSegment(sketch, "E108.12.1", {"start": v(126.82, 65.86) * mm, "end": v(127.03, 66.27) * mm});
            skLineSegment(sketch, "E108.12.2", {"start": v(127.03, 66.27) * mm, "end": v(126.78, 66.65) * mm});
            skLineSegment(sketch, "E108.12.3", {"start": v(127.28, 65.88) * mm, "end": v(126.82, 65.86) * mm});
            skLineSegment(sketch, "E108.13.0", {"start": v(126.78, 66.65) * mm, "end": v(126.51, 67.03) * mm});
            skLineSegment(sketch, "E108.13.1", {"start": v(126.06, 66.98) * mm, "end": v(126.24, 67.4) * mm});
            skLineSegment(sketch, "E108.13.2", {"start": v(126.24, 67.4) * mm, "end": v(125.97, 67.77) * mm});
            skLineSegment(sketch, "E108.13.3", {"start": v(126.51, 67.03) * mm, "end": v(126.06, 66.98) * mm});
            skLineSegment(sketch, "E108.14.0", {"start": v(125.97, 67.77) * mm, "end": v(125.68, 68.13) * mm});
            skLineSegment(sketch, "E108.14.1", {"start": v(125.23, 68.05) * mm, "end": v(125.39, 68.48) * mm});
            skLineSegment(sketch, "E108.14.2", {"start": v(125.39, 68.48) * mm, "end": v(125.09, 68.83) * mm});
            skLineSegment(sketch, "E108.14.3", {"start": v(125.68, 68.13) * mm, "end": v(125.23, 68.05) * mm});
            skLineSegment(sketch, "E108.15.0", {"start": v(125.09, 68.83) * mm, "end": v(124.78, 69.17) * mm});
            skLineSegment(sketch, "E108.15.1", {"start": v(124.33, 69.07) * mm, "end": v(124.46, 69.5) * mm});
            skLineSegment(sketch, "E108.15.2", {"start": v(124.46, 69.5) * mm, "end": v(124.14, 69.84) * mm});
            skLineSegment(sketch, "E108.15.3", {"start": v(124.78, 69.17) * mm, "end": v(124.33, 69.07) * mm});
            skLineSegment(sketch, "E108.16.0", {"start": v(124.14, 69.84) * mm, "end": v(123.81, 70.16) * mm});
            skLineSegment(sketch, "E108.16.1", {"start": v(123.37, 70.03) * mm, "end": v(123.48, 70.48) * mm});
            skLineSegment(sketch, "E108.16.2", {"start": v(123.48, 70.48) * mm, "end": v(123.13, 70.78) * mm});
            skLineSegment(sketch, "E108.16.3", {"start": v(123.81, 70.16) * mm, "end": v(123.37, 70.03) * mm});
            skLineSegment(sketch, "E108.24.0", {"start": v(114.73, 75.4) * mm, "end": v(114.3, 75.52) * mm});
            skLineSegment(sketch, "E108.24.1", {"start": v(113.97, 75.2) * mm, "end": v(113.85, 75.64) * mm});
            skLineSegment(sketch, "E108.24.2", {"start": v(113.85, 75.64) * mm, "end": v(113.4, 75.74) * mm});
            skLineSegment(sketch, "E108.24.3", {"start": v(114.3, 75.52) * mm, "end": v(113.97, 75.2) * mm});
            skLineSegment(sketch, "E108.25.0", {"start": v(113.4, 75.74) * mm, "end": v(112.95, 75.84) * mm});
            skLineSegment(sketch, "E108.25.1", {"start": v(112.65, 75.5) * mm, "end": v(112.5, 75.93) * mm});
            skLineSegment(sketch, "E108.25.2", {"start": v(112.5, 75.93) * mm, "end": v(112.04, 76) * mm});
            skLineSegment(sketch, "E108.25.3", {"start": v(112.95, 75.84) * mm, "end": v(112.65, 75.5) * mm});
            skLineSegment(sketch, "E108.26.0", {"start": v(112.04, 76) * mm, "end": v(111.59, 76.07) * mm});
            skLineSegment(sketch, "E108.26.1", {"start": v(111.3, 75.7) * mm, "end": v(111.13, 76.13) * mm});
            skLineSegment(sketch, "E108.26.2", {"start": v(111.13, 76.13) * mm, "end": v(110.67, 76.18) * mm});
            skLineSegment(sketch, "E108.26.3", {"start": v(111.59, 76.07) * mm, "end": v(111.3, 75.7) * mm});
            skLineSegment(sketch, "E108.27.0", {"start": v(110.67, 76.18) * mm, "end": v(110.21, 76.21) * mm});
            skLineSegment(sketch, "E108.27.1", {"start": v(109.96, 75.83) * mm, "end": v(109.75, 76.24) * mm});
            skLineSegment(sketch, "E108.27.2", {"start": v(109.75, 76.24) * mm, "end": v(109.3, 76.26) * mm});
            skLineSegment(sketch, "E108.27.3", {"start": v(110.21, 76.21) * mm, "end": v(109.96, 75.83) * mm});
            skLineSegment(sketch, "E108.28.0", {"start": v(109.3, 76.26) * mm, "end": v(108.84, 76.27) * mm});
            skLineSegment(sketch, "E108.28.1", {"start": v(108.6, 75.87) * mm, "end": v(108.37, 76.27) * mm});
            skLineSegment(sketch, "E108.28.2", {"start": v(108.37, 76.27) * mm, "end": v(107.91, 76.26) * mm});
            skLineSegment(sketch, "E108.28.3", {"start": v(108.84, 76.27) * mm, "end": v(108.6, 75.87) * mm});
            skLineSegment(sketch, "E108.29.0", {"start": v(107.91, 76.26) * mm, "end": v(107.46, 76.24) * mm});
            skLineSegment(sketch, "E108.29.1", {"start": v(107.25, 75.83) * mm, "end": v(107, 76.21) * mm});
            skLineSegment(sketch, "E108.29.2", {"start": v(107, 76.21) * mm, "end": v(106.54, 76.18) * mm});
            skLineSegment(sketch, "E108.29.3", {"start": v(107.46, 76.24) * mm, "end": v(107.25, 75.83) * mm});
            skLineSegment(sketch, "E108.30.0", {"start": v(106.54, 76.18) * mm, "end": v(106.08, 76.13) * mm});
            skLineSegment(sketch, "E108.30.1", {"start": v(105.9, 75.7) * mm, "end": v(105.62, 76.07) * mm});
            skLineSegment(sketch, "E108.30.2", {"start": v(105.62, 76.07) * mm, "end": v(105.17, 76) * mm});
            skLineSegment(sketch, "E108.30.3", {"start": v(106.08, 76.13) * mm, "end": v(105.9, 75.7) * mm});
            skLineSegment(sketch, "E108.31.0", {"start": v(105.17, 76) * mm, "end": v(104.71, 75.93) * mm});
            skLineSegment(sketch, "E108.31.1", {"start": v(104.56, 75.5) * mm, "end": v(104.26, 75.84) * mm});
            skLineSegment(sketch, "E108.31.2", {"start": v(104.26, 75.84) * mm, "end": v(103.81, 75.74) * mm});
            skLineSegment(sketch, "E108.31.3", {"start": v(104.71, 75.93) * mm, "end": v(104.56, 75.5) * mm});
            skLineSegment(sketch, "E108.32.0", {"start": v(103.81, 75.74) * mm, "end": v(103.36, 75.64) * mm});
            skLineSegment(sketch, "E108.32.1", {"start": v(103.24, 75.2) * mm, "end": v(102.92, 75.52) * mm});
            skLineSegment(sketch, "E108.32.2", {"start": v(102.92, 75.52) * mm, "end": v(102.48, 75.4) * mm});
            skLineSegment(sketch, "E108.32.3", {"start": v(103.36, 75.64) * mm, "end": v(103.24, 75.2) * mm});
            skLineSegment(sketch, "E108.33.0", {"start": v(102.48, 75.4) * mm, "end": v(102.03, 75.27) * mm});
            skLineSegment(sketch, "E108.33.1", {"start": v(101.94, 74.82) * mm, "end": v(101.6, 75.13) * mm});
            skLineSegment(sketch, "E108.33.2", {"start": v(101.6, 75.13) * mm, "end": v(101.16, 74.97) * mm});
            skLineSegment(sketch, "E108.33.3", {"start": v(102.03, 75.27) * mm, "end": v(101.94, 74.82) * mm});
            skLineSegment(sketch, "E108.34.0", {"start": v(101.16, 74.97) * mm, "end": v(100.73, 74.81) * mm});
            skLineSegment(sketch, "E108.34.1", {"start": v(100.66, 74.36) * mm, "end": v(100.3, 74.64) * mm});
            skLineSegment(sketch, "E108.34.2", {"start": v(100.3, 74.64) * mm, "end": v(99.88, 74.47) * mm});
            skLineSegment(sketch, "E108.34.3", {"start": v(100.73, 74.81) * mm, "end": v(100.66, 74.36) * mm});
            skLineSegment(sketch, "E108.35.0", {"start": v(99.88, 74.47) * mm, "end": v(99.46, 74.28) * mm});
            skLineSegment(sketch, "E108.35.1", {"start": v(99.42, 73.82) * mm, "end": v(99.04, 74.08) * mm});
            skLineSegment(sketch, "E108.35.2", {"start": v(99.04, 74.08) * mm, "end": v(98.63, 73.88) * mm});
            skLineSegment(sketch, "E108.35.3", {"start": v(99.46, 74.28) * mm, "end": v(99.42, 73.82) * mm});
            skLineSegment(sketch, "E108.36.0", {"start": v(98.63, 73.88) * mm, "end": v(98.22, 73.67) * mm});
            skLineSegment(sketch, "E108.36.1", {"start": v(98.21, 73.2) * mm, "end": v(97.82, 73.44) * mm});
            skLineSegment(sketch, "E108.36.2", {"start": v(97.82, 73.44) * mm, "end": v(97.42, 73.21) * mm});
            skLineSegment(sketch, "E108.36.3", {"start": v(98.22, 73.67) * mm, "end": v(98.21, 73.2) * mm});
            skLineSegment(sketch, "E108.37.0", {"start": v(97.42, 73.21) * mm, "end": v(97.03, 72.98) * mm});
            skLineSegment(sketch, "E108.37.1", {"start": v(97.05, 72.52) * mm, "end": v(96.64, 72.73) * mm});
            skLineSegment(sketch, "E108.37.2", {"start": v(96.64, 72.73) * mm, "end": v(96.26, 72.47) * mm});
            skLineSegment(sketch, "E108.37.3", {"start": v(97.03, 72.98) * mm, "end": v(97.05, 72.52) * mm});
            skLineSegment(sketch, "E108.38.0", {"start": v(96.26, 72.47) * mm, "end": v(95.88, 72.21) * mm});
            skLineSegment(sketch, "E108.38.1", {"start": v(95.93, 71.75) * mm, "end": v(95.5, 71.94) * mm});
            skLineSegment(sketch, "E108.38.2", {"start": v(95.5, 71.94) * mm, "end": v(95.14, 71.66) * mm});
            skLineSegment(sketch, "E108.38.3", {"start": v(95.88, 72.21) * mm, "end": v(95.93, 71.75) * mm});
            skLineSegment(sketch, "E108.39.0", {"start": v(95.14, 71.66) * mm, "end": v(94.78, 71.38) * mm});
            skLineSegment(sketch, "E108.39.1", {"start": v(94.85, 70.92) * mm, "end": v(94.42, 71.08) * mm});
            skLineSegment(sketch, "E108.39.2", {"start": v(94.42, 71.08) * mm, "end": v(94.08, 70.78) * mm});
            skLineSegment(sketch, "E108.39.3", {"start": v(94.78, 71.38) * mm, "end": v(94.85, 70.92) * mm});
            skLineSegment(sketch, "E108.40.0", {"start": v(94.08, 70.78) * mm, "end": v(93.73, 70.48) * mm});
            skLineSegment(sketch, "E108.40.1", {"start": v(93.84, 70.03) * mm, "end": v(93.4, 70.16) * mm});
            skLineSegment(sketch, "E108.40.2", {"start": v(93.4, 70.16) * mm, "end": v(93.07, 69.84) * mm});
            skLineSegment(sketch, "E108.40.3", {"start": v(93.73, 70.48) * mm, "end": v(93.84, 70.03) * mm});
            skLineSegment(sketch, "E108.50.0", {"start": v(87.16, 59.1) * mm, "end": v(87.07, 58.65) * mm});
            skLineSegment(sketch, "E108.50.1", {"start": v(87.42, 58.34) * mm, "end": v(86.98, 58.2) * mm});
            skLineSegment(sketch, "E108.50.2", {"start": v(86.98, 58.2) * mm, "end": v(86.9, 57.74) * mm});
            skLineSegment(sketch, "E108.50.3", {"start": v(87.07, 58.65) * mm, "end": v(87.42, 58.34) * mm});
            skLineSegment(sketch, "E108.51.0", {"start": v(86.9, 57.74) * mm, "end": v(86.84, 57.28) * mm});
            skLineSegment(sketch, "E108.51.1", {"start": v(87.2, 57) * mm, "end": v(86.78, 56.83) * mm});
            skLineSegment(sketch, "E108.51.2", {"start": v(86.78, 56.83) * mm, "end": v(86.73, 56.37) * mm});
            skLineSegment(sketch, "E108.51.3", {"start": v(86.84, 57.28) * mm, "end": v(87.2, 57) * mm});
            skLineSegment(sketch, "E108.52.0", {"start": v(86.73, 56.37) * mm, "end": v(86.7, 55.91) * mm});
            skLineSegment(sketch, "E108.52.1", {"start": v(87.08, 55.66) * mm, "end": v(86.66, 55.45) * mm});
            skLineSegment(sketch, "E108.52.2", {"start": v(86.66, 55.45) * mm, "end": v(86.64, 55) * mm});
            skLineSegment(sketch, "E108.52.3", {"start": v(86.7, 55.91) * mm, "end": v(87.08, 55.66) * mm});
            skLineSegment(sketch, "E108.53.0", {"start": v(86.64, 55) * mm, "end": v(86.64, 54.53) * mm});
            skLineSegment(sketch, "E108.53.1", {"start": v(87.03, 54.3) * mm, "end": v(86.64, 54.07) * mm});
            skLineSegment(sketch, "E108.53.2", {"start": v(86.64, 54.07) * mm, "end": v(86.64, 53.61) * mm});
            skLineSegment(sketch, "E108.53.3", {"start": v(86.64, 54.53) * mm, "end": v(87.03, 54.3) * mm});
            skLineSegment(sketch, "E108.54.0", {"start": v(86.64, 53.61) * mm, "end": v(86.66, 53.15) * mm});
            skLineSegment(sketch, "E108.54.1", {"start": v(87.08, 52.95) * mm, "end": v(86.7, 52.7) * mm});
            skLineSegment(sketch, "E108.54.2", {"start": v(86.7, 52.7) * mm, "end": v(86.73, 52.23) * mm});
            skLineSegment(sketch, "E108.54.3", {"start": v(86.66, 53.15) * mm, "end": v(87.08, 52.95) * mm});
            skLineSegment(sketch, "E108.55.0", {"start": v(86.73, 52.23) * mm, "end": v(86.78, 51.78) * mm});
            skLineSegment(sketch, "E108.55.1", {"start": v(87.2, 51.6) * mm, "end": v(86.84, 51.32) * mm});
            skLineSegment(sketch, "E108.55.2", {"start": v(86.84, 51.32) * mm, "end": v(86.9, 50.87) * mm});
            skLineSegment(sketch, "E108.55.3", {"start": v(86.78, 51.78) * mm, "end": v(87.2, 51.6) * mm});
            skLineSegment(sketch, "E108.56.0", {"start": v(86.9, 50.87) * mm, "end": v(86.98, 50.41) * mm});
            skLineSegment(sketch, "E108.56.1", {"start": v(87.42, 50.26) * mm, "end": v(87.07, 49.96) * mm});
            skLineSegment(sketch, "E108.56.2", {"start": v(87.07, 49.96) * mm, "end": v(87.16, 49.5) * mm});
            skLineSegment(sketch, "E108.56.3", {"start": v(86.98, 50.41) * mm, "end": v(87.42, 50.26) * mm});
            skLineSegment(sketch, "E108.57.0", {"start": v(87.16, 49.5) * mm, "end": v(87.27, 49.06) * mm});
            skLineSegment(sketch, "E108.57.1", {"start": v(87.71, 48.94) * mm, "end": v(87.38, 48.62) * mm});
            skLineSegment(sketch, "E108.57.2", {"start": v(87.38, 48.62) * mm, "end": v(87.5, 48.17) * mm});
            skLineSegment(sketch, "E108.57.3", {"start": v(87.27, 49.06) * mm, "end": v(87.71, 48.94) * mm});
            skLineSegment(sketch, "E108.58.0", {"start": v(87.5, 48.17) * mm, "end": v(87.64, 47.73) * mm});
            skLineSegment(sketch, "E108.58.1", {"start": v(88.09, 47.64) * mm, "end": v(87.78, 47.3) * mm});
            skLineSegment(sketch, "E108.58.2", {"start": v(87.78, 47.3) * mm, "end": v(87.93, 46.86) * mm});
            skLineSegment(sketch, "E108.58.3", {"start": v(87.64, 47.73) * mm, "end": v(88.09, 47.64) * mm});
            skLineSegment(sketch, "E108.59.0", {"start": v(87.93, 46.86) * mm, "end": v(88.1, 46.43) * mm});
            skLineSegment(sketch, "E108.59.1", {"start": v(88.55, 46.36) * mm, "end": v(88.26, 46) * mm});
            skLineSegment(sketch, "E108.59.2", {"start": v(88.26, 46) * mm, "end": v(88.44, 45.58) * mm});
            skLineSegment(sketch, "E108.59.3", {"start": v(88.1, 46.43) * mm, "end": v(88.55, 46.36) * mm});
            skLineSegment(sketch, "E108.60.0", {"start": v(88.44, 45.58) * mm, "end": v(88.63, 45.16) * mm});
            skLineSegment(sketch, "E108.60.1", {"start": v(89.09, 45.12) * mm, "end": v(88.82, 44.74) * mm});
            skLineSegment(sketch, "E108.60.2", {"start": v(88.82, 44.74) * mm, "end": v(89.03, 44.33) * mm});
            skLineSegment(sketch, "E108.60.3", {"start": v(88.63, 45.16) * mm, "end": v(89.09, 45.12) * mm});
            skLineSegment(sketch, "E108.61.0", {"start": v(89.03, 44.33) * mm, "end": v(89.24, 43.92) * mm});
            skLineSegment(sketch, "E108.61.1", {"start": v(89.7, 43.91) * mm, "end": v(89.46, 43.52) * mm});
            skLineSegment(sketch, "E108.61.2", {"start": v(89.46, 43.52) * mm, "end": v(89.7, 43.12) * mm});
            skLineSegment(sketch, "E108.61.3", {"start": v(89.24, 43.92) * mm, "end": v(89.7, 43.91) * mm});
            skLineSegment(sketch, "E108.62.0", {"start": v(89.7, 43.12) * mm, "end": v(89.93, 42.72) * mm});
            skLineSegment(sketch, "E108.62.1", {"start": v(90.4, 42.74) * mm, "end": v(90.18, 42.34) * mm});
            skLineSegment(sketch, "E108.62.2", {"start": v(90.18, 42.34) * mm, "end": v(90.43, 41.95) * mm});
            skLineSegment(sketch, "E108.62.3", {"start": v(89.93, 42.72) * mm, "end": v(90.4, 42.74) * mm});
            skLineSegment(sketch, "E108.63.0", {"start": v(90.43, 41.95) * mm, "end": v(90.7, 41.58) * mm});
            skLineSegment(sketch, "E108.63.1", {"start": v(91.15, 41.62) * mm, "end": v(90.97, 41.2) * mm});
            skLineSegment(sketch, "E108.63.2", {"start": v(90.97, 41.2) * mm, "end": v(91.24, 40.84) * mm});
            skLineSegment(sketch, "E108.63.3", {"start": v(90.7, 41.58) * mm, "end": v(91.15, 41.62) * mm});
            skLineSegment(sketch, "E108.64.0", {"start": v(91.24, 40.84) * mm, "end": v(91.53, 40.48) * mm});
            skLineSegment(sketch, "E108.64.1", {"start": v(91.98, 40.55) * mm, "end": v(91.82, 40.12) * mm});
            skLineSegment(sketch, "E108.64.2", {"start": v(91.82, 40.12) * mm, "end": v(92.12, 39.77) * mm});
            skLineSegment(sketch, "E108.64.3", {"start": v(91.53, 40.48) * mm, "end": v(91.98, 40.55) * mm});
            skLineSegment(sketch, "E108.65.0", {"start": v(92.12, 39.77) * mm, "end": v(92.43, 39.43) * mm});
            skLineSegment(sketch, "E108.65.1", {"start": v(92.88, 39.54) * mm, "end": v(92.75, 39.1) * mm});
            skLineSegment(sketch, "E108.65.2", {"start": v(92.75, 39.1) * mm, "end": v(93.07, 38.77) * mm});
            skLineSegment(sketch, "E108.65.3", {"start": v(92.43, 39.43) * mm, "end": v(92.88, 39.54) * mm});
            skLineSegment(sketch, "E108.66.0", {"start": v(93.07, 38.77) * mm, "end": v(93.4, 38.44) * mm});
            skLineSegment(sketch, "E108.66.1", {"start": v(93.84, 38.58) * mm, "end": v(93.73, 38.13) * mm});
            skLineSegment(sketch, "E108.66.2", {"start": v(93.73, 38.13) * mm, "end": v(94.08, 37.82) * mm});
            skLineSegment(sketch, "E108.66.3", {"start": v(93.4, 38.44) * mm, "end": v(93.84, 38.58) * mm});
            skLineSegment(sketch, "E108.74.0", {"start": v(102.48, 33.2) * mm, "end": v(102.92, 33.08) * mm});
            skLineSegment(sketch, "E108.74.1", {"start": v(103.24, 33.4) * mm, "end": v(103.36, 32.97) * mm});
            skLineSegment(sketch, "E108.74.2", {"start": v(103.36, 32.97) * mm, "end": v(103.81, 32.86) * mm});
            skLineSegment(sketch, "E108.74.3", {"start": v(102.92, 33.08) * mm, "end": v(103.24, 33.4) * mm});
            skLineSegment(sketch, "E108.75.0", {"start": v(103.81, 32.86) * mm, "end": v(104.26, 32.76) * mm});
            skLineSegment(sketch, "E108.75.1", {"start": v(104.56, 33.11) * mm, "end": v(104.71, 32.68) * mm});
            skLineSegment(sketch, "E108.75.2", {"start": v(104.71, 32.68) * mm, "end": v(105.17, 32.6) * mm});
            skLineSegment(sketch, "E108.75.3", {"start": v(104.26, 32.76) * mm, "end": v(104.56, 33.11) * mm});
            skLineSegment(sketch, "E108.76.0", {"start": v(105.17, 32.6) * mm, "end": v(105.62, 32.53) * mm});
            skLineSegment(sketch, "E108.76.1", {"start": v(105.9, 32.9) * mm, "end": v(106.08, 32.48) * mm});
            skLineSegment(sketch, "E108.76.2", {"start": v(106.08, 32.48) * mm, "end": v(106.54, 32.43) * mm});
            skLineSegment(sketch, "E108.76.3", {"start": v(105.62, 32.53) * mm, "end": v(105.9, 32.9) * mm});
            skLineSegment(sketch, "E108.77.0", {"start": v(106.54, 32.43) * mm, "end": v(107, 32.4) * mm});
            skLineSegment(sketch, "E108.77.1", {"start": v(107.25, 32.77) * mm, "end": v(107.46, 32.36) * mm});
            skLineSegment(sketch, "E108.77.2", {"start": v(107.46, 32.36) * mm, "end": v(107.91, 32.34) * mm});
            skLineSegment(sketch, "E108.77.3", {"start": v(107, 32.4) * mm, "end": v(107.25, 32.77) * mm});
            skLineSegment(sketch, "E108.78.0", {"start": v(107.91, 32.34) * mm, "end": v(108.37, 32.33) * mm});
            skLineSegment(sketch, "E108.78.1", {"start": v(108.6, 32.73) * mm, "end": v(108.84, 32.33) * mm});
            skLineSegment(sketch, "E108.78.2", {"start": v(108.84, 32.33) * mm, "end": v(109.3, 32.34) * mm});
            skLineSegment(sketch, "E108.78.3", {"start": v(108.37, 32.33) * mm, "end": v(108.6, 32.73) * mm});
            skLineSegment(sketch, "E108.79.0", {"start": v(109.3, 32.34) * mm, "end": v(109.75, 32.36) * mm});
            skLineSegment(sketch, "E108.79.1", {"start": v(109.96, 32.77) * mm, "end": v(110.21, 32.4) * mm});
            skLineSegment(sketch, "E108.79.2", {"start": v(110.21, 32.4) * mm, "end": v(110.67, 32.43) * mm});
            skLineSegment(sketch, "E108.79.3", {"start": v(109.75, 32.36) * mm, "end": v(109.96, 32.77) * mm});
            skLineSegment(sketch, "E108.80.0", {"start": v(110.67, 32.43) * mm, "end": v(111.13, 32.48) * mm});
            skLineSegment(sketch, "E108.80.1", {"start": v(111.3, 32.9) * mm, "end": v(111.59, 32.53) * mm});
            skLineSegment(sketch, "E108.80.2", {"start": v(111.59, 32.53) * mm, "end": v(112.04, 32.6) * mm});
            skLineSegment(sketch, "E108.80.3", {"start": v(111.13, 32.48) * mm, "end": v(111.3, 32.9) * mm});
            skLineSegment(sketch, "E108.81.0", {"start": v(112.04, 32.6) * mm, "end": v(112.5, 32.68) * mm});
            skLineSegment(sketch, "E108.81.1", {"start": v(112.65, 33.11) * mm, "end": v(112.95, 32.76) * mm});
            skLineSegment(sketch, "E108.81.2", {"start": v(112.95, 32.76) * mm, "end": v(113.4, 32.86) * mm});
            skLineSegment(sketch, "E108.81.3", {"start": v(112.5, 32.68) * mm, "end": v(112.65, 33.11) * mm});
            skLineSegment(sketch, "E108.82.0", {"start": v(113.4, 32.86) * mm, "end": v(113.85, 32.97) * mm});
            skLineSegment(sketch, "E108.82.1", {"start": v(113.97, 33.4) * mm, "end": v(114.3, 33.08) * mm});
            skLineSegment(sketch, "E108.82.2", {"start": v(114.3, 33.08) * mm, "end": v(114.73, 33.2) * mm});
            skLineSegment(sketch, "E108.82.3", {"start": v(113.85, 32.97) * mm, "end": v(113.97, 33.4) * mm});
            skLineSegment(sketch, "E108.83.0", {"start": v(114.73, 33.2) * mm, "end": v(115.18, 33.34) * mm});
            skLineSegment(sketch, "E108.83.1", {"start": v(115.27, 33.79) * mm, "end": v(115.61, 33.48) * mm});
            skLineSegment(sketch, "E108.83.2", {"start": v(115.61, 33.48) * mm, "end": v(116.05, 33.63) * mm});
            skLineSegment(sketch, "E108.83.3", {"start": v(115.18, 33.34) * mm, "end": v(115.27, 33.79) * mm});
            skLineSegment(sketch, "E108.84.0", {"start": v(116.05, 33.63) * mm, "end": v(116.48, 33.8) * mm});
            skLineSegment(sketch, "E108.84.1", {"start": v(116.55, 34.25) * mm, "end": v(116.9, 33.96) * mm});
            skLineSegment(sketch, "E108.84.2", {"start": v(116.9, 33.96) * mm, "end": v(117.33, 34.14) * mm});
            skLineSegment(sketch, "E108.84.3", {"start": v(116.48, 33.8) * mm, "end": v(116.55, 34.25) * mm});
            skLineSegment(sketch, "E108.85.0", {"start": v(117.33, 34.14) * mm, "end": v(117.75, 34.33) * mm});
            skLineSegment(sketch, "E108.85.1", {"start": v(117.79, 34.78) * mm, "end": v(118.17, 34.52) * mm});
            skLineSegment(sketch, "E108.85.2", {"start": v(118.17, 34.52) * mm, "end": v(118.58, 34.73) * mm});
            skLineSegment(sketch, "E108.85.3", {"start": v(117.75, 34.33) * mm, "end": v(117.79, 34.78) * mm});
            skLineSegment(sketch, "E108.86.0", {"start": v(118.58, 34.73) * mm, "end": v(118.99, 34.94) * mm});
            skLineSegment(sketch, "E108.86.1", {"start": v(119, 35.4) * mm, "end": v(119.4, 35.16) * mm});
            skLineSegment(sketch, "E108.86.2", {"start": v(119.4, 35.16) * mm, "end": v(119.79, 35.4) * mm});
            skLineSegment(sketch, "E108.86.3", {"start": v(118.99, 34.94) * mm, "end": v(119, 35.4) * mm});
            skLineSegment(sketch, "E108.87.0", {"start": v(119.79, 35.4) * mm, "end": v(120.18, 35.63) * mm});
            skLineSegment(sketch, "E108.87.1", {"start": v(120.16, 36.09) * mm, "end": v(120.57, 35.88) * mm});
            skLineSegment(sketch, "E108.87.2", {"start": v(120.57, 35.88) * mm, "end": v(120.95, 36.13) * mm});
            skLineSegment(sketch, "E108.87.3", {"start": v(120.18, 35.63) * mm, "end": v(120.16, 36.09) * mm});
            skLineSegment(sketch, "E108.88.0", {"start": v(120.95, 36.13) * mm, "end": v(121.33, 36.4) * mm});
            skLineSegment(sketch, "E108.88.1", {"start": v(121.28, 36.85) * mm, "end": v(121.7, 36.66) * mm});
            skLineSegment(sketch, "E108.88.2", {"start": v(121.7, 36.66) * mm, "end": v(122.07, 36.94) * mm});
            skLineSegment(sketch, "E108.88.3", {"start": v(121.33, 36.4) * mm, "end": v(121.28, 36.85) * mm});
            skLineSegment(sketch, "E108.89.0", {"start": v(122.07, 36.94) * mm, "end": v(122.43, 37.23) * mm});
            skLineSegment(sketch, "E108.89.1", {"start": v(122.36, 37.68) * mm, "end": v(122.79, 37.52) * mm});
            skLineSegment(sketch, "E108.89.2", {"start": v(122.79, 37.52) * mm, "end": v(123.13, 37.82) * mm});
            skLineSegment(sketch, "E108.89.3", {"start": v(122.43, 37.23) * mm, "end": v(122.36, 37.68) * mm});
            skLineSegment(sketch, "E108.90.0", {"start": v(123.13, 37.82) * mm, "end": v(123.48, 38.13) * mm});
            skLineSegment(sketch, "E108.90.1", {"start": v(123.37, 38.58) * mm, "end": v(123.81, 38.44) * mm});
            skLineSegment(sketch, "E108.90.2", {"start": v(123.81, 38.44) * mm, "end": v(124.14, 38.77) * mm});
            skLineSegment(sketch, "E108.90.3", {"start": v(123.48, 38.13) * mm, "end": v(123.37, 38.58) * mm});
            skPoint(sketch, "E108.center", {"position": v(108.6, 54.3) * mm});
            skLineSegment(sketch, "E108.anchor2", {"start": v(108.6, 54.3) * mm, "end": v(123.13, 37.82) * mm, "construction": true});
            skArc(sketch, "E109", {"start": v(87.16, 59.1) * mm, "mid": v(87.7, 47.51) * mm, "end": v(94.08, 37.82) * mm, "construction": true});
            skArc(sketch, "E110", {"start": v(93.07, 69.84) * mm, "mid": v(89.35, 64.89) * mm, "end": v(87.16, 59.1) * mm});
            skArc(sketch, "E111", {"start": v(123.13, 70.78) * mm, "mid": v(119.19, 73.56) * mm, "end": v(114.73, 75.4) * mm});
            skArc(sketch, "E112", {"start": v(124.14, 38.77) * mm, "mid": v(127.86, 43.72) * mm, "end": v(130.05, 49.5) * mm});
            skArc(sketch, "E113", {"start": v(94.08, 37.82) * mm, "mid": v(98.02, 35.05) * mm, "end": v(102.48, 33.2) * mm});
            skLineSegment(sketch, "E114", {"start": v(112.1, 0) * mm, "end": v(162.9, 0) * mm, "construction": true});
            skLineSegment(sketch, "E115", {"start": v(162.9, 0) * mm, "end": v(184.35, -4.8) * mm, "construction": true});
            skLineSegment(sketch, "E116", {"start": v(162.9, 0) * mm, "end": v(184.44, -4.34) * mm, "construction": true});
            skLineSegment(sketch, "E117", {"start": v(162.9, 0) * mm, "end": v(184.53, -3.9) * mm, "construction": true});
            skLineSegment(sketch, "E118", {"start": v(162.9, 0) * mm, "end": v(184.6, -3.44) * mm, "construction": true});
            skLineSegment(sketch, "E119", {"start": v(184.35, -4.8) * mm, "end": v(184.44, -4.34) * mm});
            skLineSegment(sketch, "E120", {"start": v(184.44, -4.34) * mm, "end": v(184.1, -4.04) * mm});
            skLineSegment(sketch, "E121", {"start": v(184.1, -4.04) * mm, "end": v(184.53, -3.9) * mm});
            skLineSegment(sketch, "E122", {"start": v(184.53, -3.9) * mm, "end": v(184.6, -3.44) * mm});
            skLineSegment(sketch, "E123", {"start": v(162.9, 0) * mm, "end": v(162.9, -21.97) * mm, "construction": true});
            skLineSegment(sketch, "E124.1.0", {"start": v(184.6, -3.44) * mm, "end": v(184.68, -2.98) * mm});
            skLineSegment(sketch, "E124.1.1", {"start": v(184.3, -2.7) * mm, "end": v(184.73, -2.53) * mm});
            skLineSegment(sketch, "E124.1.2", {"start": v(184.73, -2.53) * mm, "end": v(184.78, -2.07) * mm});
            skLineSegment(sketch, "E124.1.3", {"start": v(184.68, -2.98) * mm, "end": v(184.3, -2.7) * mm});
            skLineSegment(sketch, "E124.2.0", {"start": v(184.78, -2.07) * mm, "end": v(184.82, -1.6) * mm});
            skLineSegment(sketch, "E124.2.1", {"start": v(184.44, -1.35) * mm, "end": v(184.85, -1.15) * mm});
            skLineSegment(sketch, "E124.2.2", {"start": v(184.85, -1.15) * mm, "end": v(184.87, -0.7) * mm});
            skLineSegment(sketch, "E124.2.3", {"start": v(184.82, -1.6) * mm, "end": v(184.44, -1.35) * mm});
            skLineSegment(sketch, "E124.3.0", {"start": v(184.87, -0.7) * mm, "end": v(184.88, -0.23) * mm});
            skLineSegment(sketch, "E124.3.1", {"start": v(184.48, 0) * mm, "end": v(184.88, 0.23) * mm});
            skLineSegment(sketch, "E124.3.2", {"start": v(184.88, 0.23) * mm, "end": v(184.87, 0.7) * mm});
            skLineSegment(sketch, "E124.3.3", {"start": v(184.88, -0.23) * mm, "end": v(184.48, 0) * mm});
            skLineSegment(sketch, "E124.4.0", {"start": v(184.87, 0.7) * mm, "end": v(184.85, 1.15) * mm});
            skLineSegment(sketch, "E124.4.1", {"start": v(184.44, 1.35) * mm, "end": v(184.82, 1.6) * mm});
            skLineSegment(sketch, "E124.4.2", {"start": v(184.82, 1.6) * mm, "end": v(184.78, 2.07) * mm});
            skLineSegment(sketch, "E124.4.3", {"start": v(184.85, 1.15) * mm, "end": v(184.44, 1.35) * mm});
            skLineSegment(sketch, "E124.5.0", {"start": v(184.78, 2.07) * mm, "end": v(184.73, 2.53) * mm});
            skLineSegment(sketch, "E124.5.1", {"start": v(184.3, 2.7) * mm, "end": v(184.68, 2.98) * mm});
            skLineSegment(sketch, "E124.5.2", {"start": v(184.68, 2.98) * mm, "end": v(184.6, 3.44) * mm});
            skLineSegment(sketch, "E124.5.3", {"start": v(184.73, 2.53) * mm, "end": v(184.3, 2.7) * mm});
            skLineSegment(sketch, "E124.6.0", {"start": v(184.6, 3.44) * mm, "end": v(184.53, 3.9) * mm});
            skLineSegment(sketch, "E124.6.1", {"start": v(184.1, 4.04) * mm, "end": v(184.44, 4.34) * mm});
            skLineSegment(sketch, "E124.6.2", {"start": v(184.44, 4.34) * mm, "end": v(184.35, 4.8) * mm});
            skLineSegment(sketch, "E124.6.3", {"start": v(184.53, 3.9) * mm, "end": v(184.1, 4.04) * mm});
            skLineSegment(sketch, "E124.7.0", {"start": v(184.35, 4.8) * mm, "end": v(184.24, 5.24) * mm});
            skLineSegment(sketch, "E124.7.1", {"start": v(183.8, 5.36) * mm, "end": v(184.13, 5.69) * mm});
            skLineSegment(sketch, "E124.7.2", {"start": v(184.13, 5.69) * mm, "end": v(184, 6.13) * mm});
            skLineSegment(sketch, "E124.7.3", {"start": v(184.24, 5.24) * mm, "end": v(183.8, 5.36) * mm});
            skLineSegment(sketch, "E124.8.0", {"start": v(184, 6.13) * mm, "end": v(183.87, 6.57) * mm});
            skLineSegment(sketch, "E124.8.1", {"start": v(183.42, 6.67) * mm, "end": v(183.73, 7) * mm});
            skLineSegment(sketch, "E124.8.2", {"start": v(183.73, 7) * mm, "end": v(183.58, 7.44) * mm});
            skLineSegment(sketch, "E124.8.3", {"start": v(183.87, 6.57) * mm, "end": v(183.42, 6.67) * mm});
            skLineSegment(sketch, "E124.9.0", {"start": v(183.58, 7.44) * mm, "end": v(183.42, 7.87) * mm});
            skLineSegment(sketch, "E124.9.1", {"start": v(182.96, 7.94) * mm, "end": v(183.25, 8.3) * mm});
            skLineSegment(sketch, "E124.9.2", {"start": v(183.25, 8.3) * mm, "end": v(183.07, 8.73) * mm});
            skLineSegment(sketch, "E124.9.3", {"start": v(183.42, 7.87) * mm, "end": v(182.96, 7.94) * mm});
            skLineSegment(sketch, "E124.10.0", {"start": v(183.07, 8.73) * mm, "end": v(182.88, 9.15) * mm});
            skLineSegment(sketch, "E124.10.1", {"start": v(182.43, 9.18) * mm, "end": v(182.69, 9.56) * mm});
            skLineSegment(sketch, "E124.10.2", {"start": v(182.69, 9.56) * mm, "end": v(182.48, 9.97) * mm});
            skLineSegment(sketch, "E124.10.3", {"start": v(182.88, 9.15) * mm, "end": v(182.43, 9.18) * mm});
            skLineSegment(sketch, "E124.11.0", {"start": v(182.48, 9.97) * mm, "end": v(182.27, 10.38) * mm});
            skLineSegment(sketch, "E124.11.1", {"start": v(181.81, 10.4) * mm, "end": v(182.05, 10.79) * mm});
            skLineSegment(sketch, "E124.11.2", {"start": v(182.05, 10.79) * mm, "end": v(181.82, 11.18) * mm});
            skLineSegment(sketch, "E124.11.3", {"start": v(182.27, 10.38) * mm, "end": v(181.81, 10.4) * mm});
            skLineSegment(sketch, "E124.12.0", {"start": v(181.82, 11.18) * mm, "end": v(181.58, 11.58) * mm});
            skLineSegment(sketch, "E124.12.1", {"start": v(181.12, 11.56) * mm, "end": v(181.33, 11.97) * mm});
            skLineSegment(sketch, "E124.12.2", {"start": v(181.33, 11.97) * mm, "end": v(181.08, 12.35) * mm});
            skLineSegment(sketch, "E124.12.3", {"start": v(181.58, 11.58) * mm, "end": v(181.12, 11.56) * mm});
            skLineSegment(sketch, "E124.13.0", {"start": v(181.08, 12.35) * mm, "end": v(180.82, 12.73) * mm});
            skLineSegment(sketch, "E124.13.1", {"start": v(180.36, 12.68) * mm, "end": v(180.55, 13.1) * mm});
            skLineSegment(sketch, "E124.13.2", {"start": v(180.55, 13.1) * mm, "end": v(180.27, 13.47) * mm});
            skLineSegment(sketch, "E124.13.3", {"start": v(180.82, 12.73) * mm, "end": v(180.36, 12.68) * mm});
            skLineSegment(sketch, "E124.14.0", {"start": v(180.27, 13.47) * mm, "end": v(179.98, 13.83) * mm});
            skLineSegment(sketch, "E124.14.1", {"start": v(179.53, 13.75) * mm, "end": v(179.69, 14.18) * mm});
            skLineSegment(sketch, "E124.14.2", {"start": v(179.69, 14.18) * mm, "end": v(179.39, 14.53) * mm});
            skLineSegment(sketch, "E124.14.3", {"start": v(179.98, 13.83) * mm, "end": v(179.53, 13.75) * mm});
            skLineSegment(sketch, "E124.15.0", {"start": v(179.39, 14.53) * mm, "end": v(179.08, 14.87) * mm});
            skLineSegment(sketch, "E124.15.1", {"start": v(178.63, 14.77) * mm, "end": v(178.77, 15.2) * mm});
            skLineSegment(sketch, "E124.15.2", {"start": v(178.77, 15.2) * mm, "end": v(178.44, 15.54) * mm});
            skLineSegment(sketch, "E124.15.3", {"start": v(179.08, 14.87) * mm, "end": v(178.63, 14.77) * mm});
            skLineSegment(sketch, "E124.16.0", {"start": v(178.44, 15.54) * mm, "end": v(178.11, 15.86) * mm});
            skLineSegment(sketch, "E124.16.1", {"start": v(177.67, 15.72) * mm, "end": v(177.78, 16.17) * mm});
            skLineSegment(sketch, "E124.16.2", {"start": v(177.78, 16.17) * mm, "end": v(177.44, 16.48) * mm});
            skLineSegment(sketch, "E124.16.3", {"start": v(178.11, 15.86) * mm, "end": v(177.67, 15.72) * mm});
            skLineSegment(sketch, "E124.24.0", {"start": v(169.04, 21.1) * mm, "end": v(168.6, 21.22) * mm});
            skLineSegment(sketch, "E124.24.1", {"start": v(168.27, 20.9) * mm, "end": v(168.15, 21.34) * mm});
            skLineSegment(sketch, "E124.24.2", {"start": v(168.15, 21.34) * mm, "end": v(167.7, 21.44) * mm});
            skLineSegment(sketch, "E124.24.3", {"start": v(168.6, 21.22) * mm, "end": v(168.27, 20.9) * mm});
            skLineSegment(sketch, "E124.25.0", {"start": v(167.7, 21.44) * mm, "end": v(167.25, 21.54) * mm});
            skLineSegment(sketch, "E124.25.1", {"start": v(166.95, 21.19) * mm, "end": v(166.8, 21.62) * mm});
            skLineSegment(sketch, "E124.25.2", {"start": v(166.8, 21.62) * mm, "end": v(166.34, 21.7) * mm});
            skLineSegment(sketch, "E124.25.3", {"start": v(167.25, 21.54) * mm, "end": v(166.95, 21.19) * mm});
            skLineSegment(sketch, "E124.26.0", {"start": v(166.34, 21.7) * mm, "end": v(165.89, 21.77) * mm});
            skLineSegment(sketch, "E124.26.1", {"start": v(165.61, 21.4) * mm, "end": v(165.43, 21.83) * mm});
            skLineSegment(sketch, "E124.26.2", {"start": v(165.43, 21.83) * mm, "end": v(164.98, 21.87) * mm});
            skLineSegment(sketch, "E124.26.3", {"start": v(165.89, 21.77) * mm, "end": v(165.61, 21.4) * mm});
            skLineSegment(sketch, "E124.27.0", {"start": v(164.98, 21.87) * mm, "end": v(164.52, 21.91) * mm});
            skLineSegment(sketch, "E124.27.1", {"start": v(164.26, 21.53) * mm, "end": v(164.06, 21.94) * mm});
            skLineSegment(sketch, "E124.27.2", {"start": v(164.06, 21.94) * mm, "end": v(163.6, 21.96) * mm});
            skLineSegment(sketch, "E124.27.3", {"start": v(164.52, 21.91) * mm, "end": v(164.26, 21.53) * mm});
            skLineSegment(sketch, "E124.28.0", {"start": v(163.6, 21.96) * mm, "end": v(163.14, 21.97) * mm});
            skLineSegment(sketch, "E124.28.1", {"start": v(162.9, 21.57) * mm, "end": v(162.68, 21.97) * mm});
            skLineSegment(sketch, "E124.28.2", {"start": v(162.68, 21.97) * mm, "end": v(162.22, 21.96) * mm});
            skLineSegment(sketch, "E124.28.3", {"start": v(163.14, 21.97) * mm, "end": v(162.9, 21.57) * mm});
            skLineSegment(sketch, "E124.29.0", {"start": v(162.22, 21.96) * mm, "end": v(161.76, 21.94) * mm});
            skLineSegment(sketch, "E124.29.1", {"start": v(161.55, 21.53) * mm, "end": v(161.3, 21.91) * mm});
            skLineSegment(sketch, "E124.29.2", {"start": v(161.3, 21.91) * mm, "end": v(160.84, 21.87) * mm});
            skLineSegment(sketch, "E124.29.3", {"start": v(161.76, 21.94) * mm, "end": v(161.55, 21.53) * mm});
            skLineSegment(sketch, "E124.30.0", {"start": v(160.84, 21.87) * mm, "end": v(160.38, 21.83) * mm});
            skLineSegment(sketch, "E124.30.1", {"start": v(160.2, 21.4) * mm, "end": v(159.93, 21.77) * mm});
            skLineSegment(sketch, "E124.30.2", {"start": v(159.93, 21.77) * mm, "end": v(159.47, 21.7) * mm});
            skLineSegment(sketch, "E124.30.3", {"start": v(160.38, 21.83) * mm, "end": v(160.2, 21.4) * mm});
            skLineSegment(sketch, "E124.31.0", {"start": v(159.47, 21.7) * mm, "end": v(159.02, 21.62) * mm});
            skLineSegment(sketch, "E124.31.1", {"start": v(158.87, 21.19) * mm, "end": v(158.56, 21.54) * mm});
            skLineSegment(sketch, "E124.31.2", {"start": v(158.56, 21.54) * mm, "end": v(158.11, 21.44) * mm});
            skLineSegment(sketch, "E124.31.3", {"start": v(159.02, 21.62) * mm, "end": v(158.87, 21.19) * mm});
            skLineSegment(sketch, "E124.32.0", {"start": v(158.11, 21.44) * mm, "end": v(157.67, 21.34) * mm});
            skLineSegment(sketch, "E124.32.1", {"start": v(157.54, 20.9) * mm, "end": v(157.22, 21.22) * mm});
            skLineSegment(sketch, "E124.32.2", {"start": v(157.22, 21.22) * mm, "end": v(156.78, 21.1) * mm});
            skLineSegment(sketch, "E124.32.3", {"start": v(157.67, 21.34) * mm, "end": v(157.54, 20.9) * mm});
            skLineSegment(sketch, "E124.33.0", {"start": v(156.78, 21.1) * mm, "end": v(156.34, 20.97) * mm});
            skLineSegment(sketch, "E124.33.1", {"start": v(156.24, 20.52) * mm, "end": v(155.9, 20.82) * mm});
            skLineSegment(sketch, "E124.33.2", {"start": v(155.9, 20.82) * mm, "end": v(155.47, 20.67) * mm});
            skLineSegment(sketch, "E124.33.3", {"start": v(156.34, 20.97) * mm, "end": v(156.24, 20.52) * mm});
            skLineSegment(sketch, "E124.34.0", {"start": v(155.47, 20.67) * mm, "end": v(155.03, 20.51) * mm});
            skLineSegment(sketch, "E124.34.1", {"start": v(154.97, 20.06) * mm, "end": v(154.6, 20.34) * mm});
            skLineSegment(sketch, "E124.34.2", {"start": v(154.6, 20.34) * mm, "end": v(154.18, 20.16) * mm});
            skLineSegment(sketch, "E124.34.3", {"start": v(155.03, 20.51) * mm, "end": v(154.97, 20.06) * mm});
            skLineSegment(sketch, "E124.35.0", {"start": v(154.18, 20.16) * mm, "end": v(153.76, 19.98) * mm});
            skLineSegment(sketch, "E124.35.1", {"start": v(153.72, 19.52) * mm, "end": v(153.34, 19.78) * mm});
            skLineSegment(sketch, "E124.35.2", {"start": v(153.34, 19.78) * mm, "end": v(152.93, 19.58) * mm});
            skLineSegment(sketch, "E124.35.3", {"start": v(153.76, 19.98) * mm, "end": v(153.72, 19.52) * mm});
            skLineSegment(sketch, "E124.36.0", {"start": v(152.93, 19.58) * mm, "end": v(152.53, 19.36) * mm});
            skLineSegment(sketch, "E124.36.1", {"start": v(152.52, 18.9) * mm, "end": v(152.12, 19.14) * mm});
            skLineSegment(sketch, "E124.36.2", {"start": v(152.12, 19.14) * mm, "end": v(151.72, 18.91) * mm});
            skLineSegment(sketch, "E124.36.3", {"start": v(152.53, 19.36) * mm, "end": v(152.52, 18.9) * mm});
            skLineSegment(sketch, "E124.37.0", {"start": v(151.72, 18.91) * mm, "end": v(151.33, 18.67) * mm});
            skLineSegment(sketch, "E124.37.1", {"start": v(151.35, 18.21) * mm, "end": v(150.94, 18.43) * mm});
            skLineSegment(sketch, "E124.37.2", {"start": v(150.94, 18.43) * mm, "end": v(150.56, 18.17) * mm});
            skLineSegment(sketch, "E124.37.3", {"start": v(151.33, 18.67) * mm, "end": v(151.35, 18.21) * mm});
            skLineSegment(sketch, "E124.38.0", {"start": v(150.56, 18.17) * mm, "end": v(150.18, 17.9) * mm});
            skLineSegment(sketch, "E124.38.1", {"start": v(150.23, 17.45) * mm, "end": v(149.8, 17.64) * mm});
            skLineSegment(sketch, "E124.38.2", {"start": v(149.8, 17.64) * mm, "end": v(149.44, 17.36) * mm});
            skLineSegment(sketch, "E124.38.3", {"start": v(150.18, 17.9) * mm, "end": v(150.23, 17.45) * mm});
            skLineSegment(sketch, "E124.39.0", {"start": v(149.44, 17.36) * mm, "end": v(149.08, 17.07) * mm});
            skLineSegment(sketch, "E124.39.1", {"start": v(149.16, 16.62) * mm, "end": v(148.73, 16.78) * mm});
            skLineSegment(sketch, "E124.39.2", {"start": v(148.73, 16.78) * mm, "end": v(148.38, 16.48) * mm});
            skLineSegment(sketch, "E124.39.3", {"start": v(149.08, 17.07) * mm, "end": v(149.16, 16.62) * mm});
            skLineSegment(sketch, "E124.40.0", {"start": v(148.38, 16.48) * mm, "end": v(148.04, 16.17) * mm});
            skLineSegment(sketch, "E124.40.1", {"start": v(148.14, 15.72) * mm, "end": v(147.7, 15.86) * mm});
            skLineSegment(sketch, "E124.40.2", {"start": v(147.7, 15.86) * mm, "end": v(147.37, 15.54) * mm});
            skLineSegment(sketch, "E124.40.3", {"start": v(148.04, 16.17) * mm, "end": v(148.14, 15.72) * mm});
            skLineSegment(sketch, "E124.50.0", {"start": v(141.47, 4.8) * mm, "end": v(141.37, 4.34) * mm});
            skLineSegment(sketch, "E124.50.1", {"start": v(141.72, 4.04) * mm, "end": v(141.28, 3.9) * mm});
            skLineSegment(sketch, "E124.50.2", {"start": v(141.28, 3.9) * mm, "end": v(141.2, 3.44) * mm});
            skLineSegment(sketch, "E124.50.3", {"start": v(141.37, 4.34) * mm, "end": v(141.72, 4.04) * mm});
            skLineSegment(sketch, "E124.51.0", {"start": v(141.2, 3.44) * mm, "end": v(141.14, 2.98) * mm});
            skLineSegment(sketch, "E124.51.1", {"start": v(141.5, 2.7) * mm, "end": v(141.08, 2.53) * mm});
            skLineSegment(sketch, "E124.51.2", {"start": v(141.08, 2.53) * mm, "end": v(141.03, 2.07) * mm});
            skLineSegment(sketch, "E124.51.3", {"start": v(141.14, 2.98) * mm, "end": v(141.5, 2.7) * mm});
            skLineSegment(sketch, "E124.52.0", {"start": v(141.03, 2.07) * mm, "end": v(141, 1.6) * mm});
            skLineSegment(sketch, "E124.52.1", {"start": v(141.38, 1.35) * mm, "end": v(140.97, 1.15) * mm});
            skLineSegment(sketch, "E124.52.2", {"start": v(140.97, 1.15) * mm, "end": v(140.95, 0.7) * mm});
            skLineSegment(sketch, "E124.52.3", {"start": v(141, 1.6) * mm, "end": v(141.38, 1.35) * mm});
            skLineSegment(sketch, "E124.53.0", {"start": v(140.95, 0.7) * mm, "end": v(140.94, 0.23) * mm});
            skLineSegment(sketch, "E124.53.1", {"start": v(141.34, 0) * mm, "end": v(140.94, -0.23) * mm});
            skLineSegment(sketch, "E124.53.2", {"start": v(140.94, -0.23) * mm, "end": v(140.95, -0.7) * mm});
            skLineSegment(sketch, "E124.53.3", {"start": v(140.94, 0.23) * mm, "end": v(141.34, 0) * mm});
            skLineSegment(sketch, "E124.54.0", {"start": v(140.95, -0.7) * mm, "end": v(140.97, -1.15) * mm});
            skLineSegment(sketch, "E124.54.1", {"start": v(141.38, -1.35) * mm, "end": v(141, -1.6) * mm});
            skLineSegment(sketch, "E124.54.2", {"start": v(141, -1.6) * mm, "end": v(141.03, -2.07) * mm});
            skLineSegment(sketch, "E124.54.3", {"start": v(140.97, -1.15) * mm, "end": v(141.38, -1.35) * mm});
            skLineSegment(sketch, "E124.55.0", {"start": v(141.03, -2.07) * mm, "end": v(141.08, -2.53) * mm});
            skLineSegment(sketch, "E124.55.1", {"start": v(141.5, -2.7) * mm, "end": v(141.14, -2.98) * mm});
            skLineSegment(sketch, "E124.55.2", {"start": v(141.14, -2.98) * mm, "end": v(141.2, -3.44) * mm});
            skLineSegment(sketch, "E124.55.3", {"start": v(141.08, -2.53) * mm, "end": v(141.5, -2.7) * mm});
            skLineSegment(sketch, "E124.56.0", {"start": v(141.2, -3.44) * mm, "end": v(141.28, -3.9) * mm});
            skLineSegment(sketch, "E124.56.1", {"start": v(141.72, -4.04) * mm, "end": v(141.37, -4.34) * mm});
            skLineSegment(sketch, "E124.56.2", {"start": v(141.37, -4.34) * mm, "end": v(141.47, -4.8) * mm});
            skLineSegment(sketch, "E124.56.3", {"start": v(141.28, -3.9) * mm, "end": v(141.72, -4.04) * mm});
            skLineSegment(sketch, "E124.57.0", {"start": v(141.47, -4.8) * mm, "end": v(141.57, -5.24) * mm});
            skLineSegment(sketch, "E124.57.1", {"start": v(142.01, -5.36) * mm, "end": v(141.69, -5.69) * mm});
            skLineSegment(sketch, "E124.57.2", {"start": v(141.69, -5.69) * mm, "end": v(141.8, -6.13) * mm});
            skLineSegment(sketch, "E124.57.3", {"start": v(141.57, -5.24) * mm, "end": v(142.01, -5.36) * mm});
            skLineSegment(sketch, "E124.58.0", {"start": v(141.8, -6.13) * mm, "end": v(141.94, -6.57) * mm});
            skLineSegment(sketch, "E124.58.1", {"start": v(142.4, -6.67) * mm, "end": v(142.08, -7) * mm});
            skLineSegment(sketch, "E124.58.2", {"start": v(142.08, -7) * mm, "end": v(142.24, -7.44) * mm});
            skLineSegment(sketch, "E124.58.3", {"start": v(141.94, -6.57) * mm, "end": v(142.4, -6.67) * mm});
            skLineSegment(sketch, "E124.59.0", {"start": v(142.24, -7.44) * mm, "end": v(142.4, -7.87) * mm});
            skLineSegment(sketch, "E124.59.1", {"start": v(142.85, -7.94) * mm, "end": v(142.57, -8.3) * mm});
            skLineSegment(sketch, "E124.59.2", {"start": v(142.57, -8.3) * mm, "end": v(142.74, -8.73) * mm});
            skLineSegment(sketch, "E124.59.3", {"start": v(142.4, -7.87) * mm, "end": v(142.85, -7.94) * mm});
            skLineSegment(sketch, "E124.60.0", {"start": v(142.74, -8.73) * mm, "end": v(142.93, -9.15) * mm});
            skLineSegment(sketch, "E124.60.1", {"start": v(143.39, -9.18) * mm, "end": v(143.13, -9.56) * mm});
            skLineSegment(sketch, "E124.60.2", {"start": v(143.13, -9.56) * mm, "end": v(143.33, -9.97) * mm});
            skLineSegment(sketch, "E124.60.3", {"start": v(142.93, -9.15) * mm, "end": v(143.39, -9.18) * mm});
            skLineSegment(sketch, "E124.61.0", {"start": v(143.33, -9.97) * mm, "end": v(143.54, -10.38) * mm});
            skLineSegment(sketch, "E124.61.1", {"start": v(144, -10.4) * mm, "end": v(143.77, -10.79) * mm});
            skLineSegment(sketch, "E124.61.2", {"start": v(143.77, -10.79) * mm, "end": v(144, -11.18) * mm});
            skLineSegment(sketch, "E124.61.3", {"start": v(143.54, -10.38) * mm, "end": v(144, -10.4) * mm});
            skLineSegment(sketch, "E124.62.0", {"start": v(144, -11.18) * mm, "end": v(144.23, -11.58) * mm});
            skLineSegment(sketch, "E124.62.1", {"start": v(144.7, -11.56) * mm, "end": v(144.48, -11.97) * mm});
            skLineSegment(sketch, "E124.62.2", {"start": v(144.48, -11.97) * mm, "end": v(144.74, -12.35) * mm});
            skLineSegment(sketch, "E124.62.3", {"start": v(144.23, -11.58) * mm, "end": v(144.7, -11.56) * mm});
            skLineSegment(sketch, "E124.63.0", {"start": v(144.74, -12.35) * mm, "end": v(145, -12.73) * mm});
            skLineSegment(sketch, "E124.63.1", {"start": v(145.46, -12.68) * mm, "end": v(145.27, -13.1) * mm});
            skLineSegment(sketch, "E124.63.2", {"start": v(145.27, -13.1) * mm, "end": v(145.55, -13.47) * mm});
            skLineSegment(sketch, "E124.63.3", {"start": v(145, -12.73) * mm, "end": v(145.46, -12.68) * mm});
            skLineSegment(sketch, "E124.64.0", {"start": v(145.55, -13.47) * mm, "end": v(145.83, -13.83) * mm});
            skLineSegment(sketch, "E124.64.1", {"start": v(146.29, -13.75) * mm, "end": v(146.13, -14.18) * mm});
            skLineSegment(sketch, "E124.64.2", {"start": v(146.13, -14.18) * mm, "end": v(146.43, -14.53) * mm});
            skLineSegment(sketch, "E124.64.3", {"start": v(145.83, -13.83) * mm, "end": v(146.29, -13.75) * mm});
            skLineSegment(sketch, "E124.65.0", {"start": v(146.43, -14.53) * mm, "end": v(146.73, -14.87) * mm});
            skLineSegment(sketch, "E124.65.1", {"start": v(147.18, -14.77) * mm, "end": v(147.05, -15.2) * mm});
            skLineSegment(sketch, "E124.65.2", {"start": v(147.05, -15.2) * mm, "end": v(147.37, -15.54) * mm});
            skLineSegment(sketch, "E124.65.3", {"start": v(146.73, -14.87) * mm, "end": v(147.18, -14.77) * mm});
            skLineSegment(sketch, "E124.66.0", {"start": v(147.37, -15.54) * mm, "end": v(147.7, -15.86) * mm});
            skLineSegment(sketch, "E124.66.1", {"start": v(148.14, -15.72) * mm, "end": v(148.04, -16.17) * mm});
            skLineSegment(sketch, "E124.66.2", {"start": v(148.04, -16.17) * mm, "end": v(148.38, -16.48) * mm});
            skLineSegment(sketch, "E124.66.3", {"start": v(147.7, -15.86) * mm, "end": v(148.14, -15.72) * mm});
            skLineSegment(sketch, "E124.74.0", {"start": v(156.78, -21.1) * mm, "end": v(157.22, -21.22) * mm});
            skLineSegment(sketch, "E124.74.1", {"start": v(157.54, -20.9) * mm, "end": v(157.67, -21.34) * mm});
            skLineSegment(sketch, "E124.74.2", {"start": v(157.67, -21.34) * mm, "end": v(158.11, -21.44) * mm});
            skLineSegment(sketch, "E124.74.3", {"start": v(157.22, -21.22) * mm, "end": v(157.54, -20.9) * mm});
            skLineSegment(sketch, "E124.75.0", {"start": v(158.11, -21.44) * mm, "end": v(158.56, -21.54) * mm});
            skLineSegment(sketch, "E124.75.1", {"start": v(158.87, -21.19) * mm, "end": v(159.02, -21.62) * mm});
            skLineSegment(sketch, "E124.75.2", {"start": v(159.02, -21.62) * mm, "end": v(159.47, -21.7) * mm});
            skLineSegment(sketch, "E124.75.3", {"start": v(158.56, -21.54) * mm, "end": v(158.87, -21.19) * mm});
            skLineSegment(sketch, "E124.76.0", {"start": v(159.47, -21.7) * mm, "end": v(159.93, -21.77) * mm});
            skLineSegment(sketch, "E124.76.1", {"start": v(160.2, -21.4) * mm, "end": v(160.38, -21.83) * mm});
            skLineSegment(sketch, "E124.76.2", {"start": v(160.38, -21.83) * mm, "end": v(160.84, -21.87) * mm});
            skLineSegment(sketch, "E124.76.3", {"start": v(159.93, -21.77) * mm, "end": v(160.2, -21.4) * mm});
            skLineSegment(sketch, "E124.77.0", {"start": v(160.84, -21.87) * mm, "end": v(161.3, -21.91) * mm});
            skLineSegment(sketch, "E124.77.1", {"start": v(161.55, -21.53) * mm, "end": v(161.76, -21.94) * mm});
            skLineSegment(sketch, "E124.77.2", {"start": v(161.76, -21.94) * mm, "end": v(162.22, -21.96) * mm});
            skLineSegment(sketch, "E124.77.3", {"start": v(161.3, -21.91) * mm, "end": v(161.55, -21.53) * mm});
            skLineSegment(sketch, "E124.78.0", {"start": v(162.22, -21.96) * mm, "end": v(162.68, -21.97) * mm});
            skLineSegment(sketch, "E124.78.1", {"start": v(162.9, -21.57) * mm, "end": v(163.14, -21.97) * mm});
            skLineSegment(sketch, "E124.78.2", {"start": v(163.14, -21.97) * mm, "end": v(163.6, -21.96) * mm});
            skLineSegment(sketch, "E124.78.3", {"start": v(162.68, -21.97) * mm, "end": v(162.9, -21.57) * mm});
            skLineSegment(sketch, "E124.79.0", {"start": v(163.6, -21.96) * mm, "end": v(164.06, -21.94) * mm});
            skLineSegment(sketch, "E124.79.1", {"start": v(164.26, -21.53) * mm, "end": v(164.52, -21.91) * mm});
            skLineSegment(sketch, "E124.79.2", {"start": v(164.52, -21.91) * mm, "end": v(164.98, -21.87) * mm});
            skLineSegment(sketch, "E124.79.3", {"start": v(164.06, -21.94) * mm, "end": v(164.26, -21.53) * mm});
            skLineSegment(sketch, "E124.80.0", {"start": v(164.98, -21.87) * mm, "end": v(165.43, -21.83) * mm});
            skLineSegment(sketch, "E124.80.1", {"start": v(165.61, -21.4) * mm, "end": v(165.89, -21.77) * mm});
            skLineSegment(sketch, "E124.80.2", {"start": v(165.89, -21.77) * mm, "end": v(166.34, -21.7) * mm});
            skLineSegment(sketch, "E124.80.3", {"start": v(165.43, -21.83) * mm, "end": v(165.61, -21.4) * mm});
            skLineSegment(sketch, "E124.81.0", {"start": v(166.34, -21.7) * mm, "end": v(166.8, -21.62) * mm});
            skLineSegment(sketch, "E124.81.1", {"start": v(166.95, -21.19) * mm, "end": v(167.25, -21.54) * mm});
            skLineSegment(sketch, "E124.81.2", {"start": v(167.25, -21.54) * mm, "end": v(167.7, -21.44) * mm});
            skLineSegment(sketch, "E124.81.3", {"start": v(166.8, -21.62) * mm, "end": v(166.95, -21.19) * mm});
            skLineSegment(sketch, "E124.82.0", {"start": v(167.7, -21.44) * mm, "end": v(168.15, -21.34) * mm});
            skLineSegment(sketch, "E124.82.1", {"start": v(168.27, -20.9) * mm, "end": v(168.6, -21.22) * mm});
            skLineSegment(sketch, "E124.82.2", {"start": v(168.6, -21.22) * mm, "end": v(169.04, -21.1) * mm});
            skLineSegment(sketch, "E124.82.3", {"start": v(168.15, -21.34) * mm, "end": v(168.27, -20.9) * mm});
            skLineSegment(sketch, "E124.83.0", {"start": v(169.04, -21.1) * mm, "end": v(169.48, -20.97) * mm});
            skLineSegment(sketch, "E124.83.1", {"start": v(169.57, -20.52) * mm, "end": v(169.92, -20.82) * mm});
            skLineSegment(sketch, "E124.83.2", {"start": v(169.92, -20.82) * mm, "end": v(170.35, -20.67) * mm});
            skLineSegment(sketch, "E124.83.3", {"start": v(169.48, -20.97) * mm, "end": v(169.57, -20.52) * mm});
            skLineSegment(sketch, "E124.84.0", {"start": v(170.35, -20.67) * mm, "end": v(170.78, -20.51) * mm});
            skLineSegment(sketch, "E124.84.1", {"start": v(170.85, -20.06) * mm, "end": v(171.2, -20.34) * mm});
            skLineSegment(sketch, "E124.84.2", {"start": v(171.2, -20.34) * mm, "end": v(171.63, -20.16) * mm});
            skLineSegment(sketch, "E124.84.3", {"start": v(170.78, -20.51) * mm, "end": v(170.85, -20.06) * mm});
            skLineSegment(sketch, "E124.85.0", {"start": v(171.63, -20.16) * mm, "end": v(172.05, -19.98) * mm});
            skLineSegment(sketch, "E124.85.1", {"start": v(172.1, -19.52) * mm, "end": v(172.47, -19.78) * mm});
            skLineSegment(sketch, "E124.85.2", {"start": v(172.47, -19.78) * mm, "end": v(172.88, -19.58) * mm});
            skLineSegment(sketch, "E124.85.3", {"start": v(172.05, -19.98) * mm, "end": v(172.1, -19.52) * mm});
            skLineSegment(sketch, "E124.86.0", {"start": v(172.88, -19.58) * mm, "end": v(173.29, -19.36) * mm});
            skLineSegment(sketch, "E124.86.1", {"start": v(173.3, -18.9) * mm, "end": v(173.7, -19.14) * mm});
            skLineSegment(sketch, "E124.86.2", {"start": v(173.7, -19.14) * mm, "end": v(174.1, -18.91) * mm});
            skLineSegment(sketch, "E124.86.3", {"start": v(173.29, -19.36) * mm, "end": v(173.3, -18.9) * mm});
            skLineSegment(sketch, "E124.87.0", {"start": v(174.1, -18.91) * mm, "end": v(174.49, -18.67) * mm});
            skLineSegment(sketch, "E124.87.1", {"start": v(174.47, -18.21) * mm, "end": v(174.87, -18.43) * mm});
            skLineSegment(sketch, "E124.87.2", {"start": v(174.87, -18.43) * mm, "end": v(175.26, -18.17) * mm});
            skLineSegment(sketch, "E124.87.3", {"start": v(174.49, -18.67) * mm, "end": v(174.47, -18.21) * mm});
            skLineSegment(sketch, "E124.88.0", {"start": v(175.26, -18.17) * mm, "end": v(175.63, -17.9) * mm});
            skLineSegment(sketch, "E124.88.1", {"start": v(175.59, -17.45) * mm, "end": v(176, -17.64) * mm});
            skLineSegment(sketch, "E124.88.2", {"start": v(176, -17.64) * mm, "end": v(176.37, -17.36) * mm});
            skLineSegment(sketch, "E124.88.3", {"start": v(175.63, -17.9) * mm, "end": v(175.59, -17.45) * mm});
            skLineSegment(sketch, "E124.89.0", {"start": v(176.37, -17.36) * mm, "end": v(176.73, -17.07) * mm});
            skLineSegment(sketch, "E124.89.1", {"start": v(176.66, -16.62) * mm, "end": v(177.09, -16.78) * mm});
            skLineSegment(sketch, "E124.89.2", {"start": v(177.09, -16.78) * mm, "end": v(177.44, -16.48) * mm});
            skLineSegment(sketch, "E124.89.3", {"start": v(176.73, -17.07) * mm, "end": v(176.66, -16.62) * mm});
            skLineSegment(sketch, "E124.90.0", {"start": v(177.44, -16.48) * mm, "end": v(177.78, -16.17) * mm});
            skLineSegment(sketch, "E124.90.1", {"start": v(177.67, -15.72) * mm, "end": v(178.11, -15.86) * mm});
            skLineSegment(sketch, "E124.90.2", {"start": v(178.11, -15.86) * mm, "end": v(178.44, -15.54) * mm});
            skLineSegment(sketch, "E124.90.3", {"start": v(177.78, -16.17) * mm, "end": v(177.67, -15.72) * mm});
            skPoint(sketch, "E124.center", {"position": v(162.9, 0) * mm});
            skLineSegment(sketch, "E124.anchor2", {"start": v(162.9, 0) * mm, "end": v(177.44, -16.48) * mm, "construction": true});
            skArc(sketch, "E125", {"start": v(141.47, 4.8) * mm, "mid": v(142.01, -6.79) * mm, "end": v(148.38, -16.48) * mm, "construction": true});
            skArc(sketch, "E126", {"start": v(147.37, 15.54) * mm, "mid": v(143.65, 10.58) * mm, "end": v(141.47, 4.8) * mm});
            skArc(sketch, "E127", {"start": v(177.44, 16.48) * mm, "mid": v(173.5, 19.25) * mm, "end": v(169.04, 21.1) * mm});
            skArc(sketch, "E128", {"start": v(178.44, -15.54) * mm, "mid": v(182.16, -10.58) * mm, "end": v(184.35, -4.8) * mm});
            skArc(sketch, "E129", {"start": v(148.38, -16.48) * mm, "mid": v(152.32, -19.25) * mm, "end": v(156.78, -21.1) * mm});
            skLineSegment(sketch, "E130", {"start": v(112.1, 54.3) * mm, "end": v(162.9, 54.3) * mm, "construction": true});
            skLineSegment(sketch, "E131", {"start": v(162.9, 54.3) * mm, "end": v(184.35, 49.5) * mm, "construction": true});
            skLineSegment(sketch, "E132", {"start": v(162.9, 54.3) * mm, "end": v(184.44, 49.96) * mm, "construction": true});
            skLineSegment(sketch, "E133", {"start": v(162.9, 54.3) * mm, "end": v(184.53, 50.41) * mm, "construction": true});
            skLineSegment(sketch, "E134", {"start": v(162.9, 54.3) * mm, "end": v(184.6, 50.87) * mm, "construction": true});
            skLineSegment(sketch, "E135", {"start": v(184.35, 49.5) * mm, "end": v(184.44, 49.96) * mm});
            skLineSegment(sketch, "E136", {"start": v(184.44, 49.96) * mm, "end": v(184.1, 50.26) * mm});
            skLineSegment(sketch, "E137", {"start": v(184.1, 50.26) * mm, "end": v(184.53, 50.41) * mm});
            skLineSegment(sketch, "E138", {"start": v(184.53, 50.41) * mm, "end": v(184.6, 50.87) * mm});
            skLineSegment(sketch, "E139", {"start": v(162.9, 54.3) * mm, "end": v(162.9, 32.33) * mm, "construction": true});
            skLineSegment(sketch, "E140.1.0", {"start": v(184.6, 50.87) * mm, "end": v(184.68, 51.32) * mm});
            skLineSegment(sketch, "E140.1.1", {"start": v(184.3, 51.6) * mm, "end": v(184.73, 51.78) * mm});
            skLineSegment(sketch, "E140.1.2", {"start": v(184.73, 51.78) * mm, "end": v(184.78, 52.23) * mm});
            skLineSegment(sketch, "E140.1.3", {"start": v(184.68, 51.32) * mm, "end": v(184.3, 51.6) * mm});
            skLineSegment(sketch, "E140.2.0", {"start": v(184.78, 52.23) * mm, "end": v(184.82, 52.7) * mm});
            skLineSegment(sketch, "E140.2.1", {"start": v(184.44, 52.95) * mm, "end": v(184.85, 53.15) * mm});
            skLineSegment(sketch, "E140.2.2", {"start": v(184.85, 53.15) * mm, "end": v(184.87, 53.61) * mm});
            skLineSegment(sketch, "E140.2.3", {"start": v(184.82, 52.7) * mm, "end": v(184.44, 52.95) * mm});
            skLineSegment(sketch, "E140.3.0", {"start": v(184.87, 53.61) * mm, "end": v(184.88, 54.07) * mm});
            skLineSegment(sketch, "E140.3.1", {"start": v(184.48, 54.3) * mm, "end": v(184.88, 54.53) * mm});
            skLineSegment(sketch, "E140.3.2", {"start": v(184.88, 54.53) * mm, "end": v(184.87, 55) * mm});
            skLineSegment(sketch, "E140.3.3", {"start": v(184.88, 54.07) * mm, "end": v(184.48, 54.3) * mm});
            skLineSegment(sketch, "E140.4.0", {"start": v(184.87, 55) * mm, "end": v(184.85, 55.45) * mm});
            skLineSegment(sketch, "E140.4.1", {"start": v(184.44, 55.66) * mm, "end": v(184.82, 55.91) * mm});
            skLineSegment(sketch, "E140.4.2", {"start": v(184.82, 55.91) * mm, "end": v(184.78, 56.37) * mm});
            skLineSegment(sketch, "E140.4.3", {"start": v(184.85, 55.45) * mm, "end": v(184.44, 55.66) * mm});
            skLineSegment(sketch, "E140.5.0", {"start": v(184.78, 56.37) * mm, "end": v(184.73, 56.83) * mm});
            skLineSegment(sketch, "E140.5.1", {"start": v(184.3, 57) * mm, "end": v(184.68, 57.28) * mm});
            skLineSegment(sketch, "E140.5.2", {"start": v(184.68, 57.28) * mm, "end": v(184.6, 57.74) * mm});
            skLineSegment(sketch, "E140.5.3", {"start": v(184.73, 56.83) * mm, "end": v(184.3, 57) * mm});
            skLineSegment(sketch, "E140.6.0", {"start": v(184.6, 57.74) * mm, "end": v(184.53, 58.2) * mm});
            skLineSegment(sketch, "E140.6.1", {"start": v(184.1, 58.34) * mm, "end": v(184.44, 58.65) * mm});
            skLineSegment(sketch, "E140.6.2", {"start": v(184.44, 58.65) * mm, "end": v(184.35, 59.1) * mm});
            skLineSegment(sketch, "E140.6.3", {"start": v(184.53, 58.2) * mm, "end": v(184.1, 58.34) * mm});
            skLineSegment(sketch, "E140.7.0", {"start": v(184.35, 59.1) * mm, "end": v(184.24, 59.54) * mm});
            skLineSegment(sketch, "E140.7.1", {"start": v(183.8, 59.67) * mm, "end": v(184.13, 59.99) * mm});
            skLineSegment(sketch, "E140.7.2", {"start": v(184.13, 59.99) * mm, "end": v(184, 60.43) * mm});
            skLineSegment(sketch, "E140.7.3", {"start": v(184.24, 59.54) * mm, "end": v(183.8, 59.67) * mm});
            skLineSegment(sketch, "E140.8.0", {"start": v(184, 60.43) * mm, "end": v(183.87, 60.87) * mm});
            skLineSegment(sketch, "E140.8.1", {"start": v(183.42, 60.97) * mm, "end": v(183.73, 61.31) * mm});
            skLineSegment(sketch, "E140.8.2", {"start": v(183.73, 61.31) * mm, "end": v(183.58, 61.74) * mm});
            skLineSegment(sketch, "E140.8.3", {"start": v(183.87, 60.87) * mm, "end": v(183.42, 60.97) * mm});
            skLineSegment(sketch, "E140.9.0", {"start": v(183.58, 61.74) * mm, "end": v(183.42, 62.18) * mm});
            skLineSegment(sketch, "E140.9.1", {"start": v(182.96, 62.24) * mm, "end": v(183.25, 62.6) * mm});
            skLineSegment(sketch, "E140.9.2", {"start": v(183.25, 62.6) * mm, "end": v(183.07, 63.03) * mm});
            skLineSegment(sketch, "E140.9.3", {"start": v(183.42, 62.18) * mm, "end": v(182.96, 62.24) * mm});
            skLineSegment(sketch, "E140.10.0", {"start": v(183.07, 63.03) * mm, "end": v(182.88, 63.45) * mm});
            skLineSegment(sketch, "E140.10.1", {"start": v(182.43, 63.49) * mm, "end": v(182.69, 63.86) * mm});
            skLineSegment(sketch, "E140.10.2", {"start": v(182.69, 63.86) * mm, "end": v(182.48, 64.28) * mm});
            skLineSegment(sketch, "E140.10.3", {"start": v(182.88, 63.45) * mm, "end": v(182.43, 63.49) * mm});
            skLineSegment(sketch, "E140.11.0", {"start": v(182.48, 64.28) * mm, "end": v(182.27, 64.68) * mm});
            skLineSegment(sketch, "E140.11.1", {"start": v(181.81, 64.7) * mm, "end": v(182.05, 65.09) * mm});
            skLineSegment(sketch, "E140.11.2", {"start": v(182.05, 65.09) * mm, "end": v(181.82, 65.49) * mm});
            skLineSegment(sketch, "E140.11.3", {"start": v(182.27, 64.68) * mm, "end": v(181.81, 64.7) * mm});
            skLineSegment(sketch, "E140.12.0", {"start": v(181.82, 65.49) * mm, "end": v(181.58, 65.88) * mm});
            skLineSegment(sketch, "E140.12.1", {"start": v(181.12, 65.86) * mm, "end": v(181.33, 66.27) * mm});
            skLineSegment(sketch, "E140.12.2", {"start": v(181.33, 66.27) * mm, "end": v(181.08, 66.65) * mm});
            skLineSegment(sketch, "E140.12.3", {"start": v(181.58, 65.88) * mm, "end": v(181.12, 65.86) * mm});
            skLineSegment(sketch, "E140.13.0", {"start": v(181.08, 66.65) * mm, "end": v(180.82, 67.03) * mm});
            skLineSegment(sketch, "E140.13.1", {"start": v(180.36, 66.98) * mm, "end": v(180.55, 67.4) * mm});
            skLineSegment(sketch, "E140.13.2", {"start": v(180.55, 67.4) * mm, "end": v(180.27, 67.77) * mm});
            skLineSegment(sketch, "E140.13.3", {"start": v(180.82, 67.03) * mm, "end": v(180.36, 66.98) * mm});
            skLineSegment(sketch, "E140.14.0", {"start": v(180.27, 67.77) * mm, "end": v(179.98, 68.13) * mm});
            skLineSegment(sketch, "E140.14.1", {"start": v(179.53, 68.05) * mm, "end": v(179.69, 68.48) * mm});
            skLineSegment(sketch, "E140.14.2", {"start": v(179.69, 68.48) * mm, "end": v(179.39, 68.83) * mm});
            skLineSegment(sketch, "E140.14.3", {"start": v(179.98, 68.13) * mm, "end": v(179.53, 68.05) * mm});
            skLineSegment(sketch, "E140.15.0", {"start": v(179.39, 68.83) * mm, "end": v(179.08, 69.17) * mm});
            skLineSegment(sketch, "E140.15.1", {"start": v(178.63, 69.07) * mm, "end": v(178.77, 69.5) * mm});
            skLineSegment(sketch, "E140.15.2", {"start": v(178.77, 69.5) * mm, "end": v(178.44, 69.84) * mm});
            skLineSegment(sketch, "E140.15.3", {"start": v(179.08, 69.17) * mm, "end": v(178.63, 69.07) * mm});
            skLineSegment(sketch, "E140.16.0", {"start": v(178.44, 69.84) * mm, "end": v(178.11, 70.16) * mm});
            skLineSegment(sketch, "E140.16.1", {"start": v(177.67, 70.03) * mm, "end": v(177.78, 70.48) * mm});
            skLineSegment(sketch, "E140.16.2", {"start": v(177.78, 70.48) * mm, "end": v(177.44, 70.78) * mm});
            skLineSegment(sketch, "E140.16.3", {"start": v(178.11, 70.16) * mm, "end": v(177.67, 70.03) * mm});
            skLineSegment(sketch, "E140.24.0", {"start": v(169.04, 75.4) * mm, "end": v(168.6, 75.52) * mm});
            skLineSegment(sketch, "E140.24.1", {"start": v(168.27, 75.2) * mm, "end": v(168.15, 75.64) * mm});
            skLineSegment(sketch, "E140.24.2", {"start": v(168.15, 75.64) * mm, "end": v(167.7, 75.74) * mm});
            skLineSegment(sketch, "E140.24.3", {"start": v(168.6, 75.52) * mm, "end": v(168.27, 75.2) * mm});
            skLineSegment(sketch, "E140.25.0", {"start": v(167.7, 75.74) * mm, "end": v(167.25, 75.84) * mm});
            skLineSegment(sketch, "E140.25.1", {"start": v(166.95, 75.5) * mm, "end": v(166.8, 75.93) * mm});
            skLineSegment(sketch, "E140.25.2", {"start": v(166.8, 75.93) * mm, "end": v(166.34, 76) * mm});
            skLineSegment(sketch, "E140.25.3", {"start": v(167.25, 75.84) * mm, "end": v(166.95, 75.5) * mm});
            skLineSegment(sketch, "E140.26.0", {"start": v(166.34, 76) * mm, "end": v(165.89, 76.07) * mm});
            skLineSegment(sketch, "E140.26.1", {"start": v(165.61, 75.7) * mm, "end": v(165.43, 76.13) * mm});
            skLineSegment(sketch, "E140.26.2", {"start": v(165.43, 76.13) * mm, "end": v(164.98, 76.18) * mm});
            skLineSegment(sketch, "E140.26.3", {"start": v(165.89, 76.07) * mm, "end": v(165.61, 75.7) * mm});
            skLineSegment(sketch, "E140.27.0", {"start": v(164.98, 76.18) * mm, "end": v(164.52, 76.21) * mm});
            skLineSegment(sketch, "E140.27.1", {"start": v(164.26, 75.83) * mm, "end": v(164.06, 76.24) * mm});
            skLineSegment(sketch, "E140.27.2", {"start": v(164.06, 76.24) * mm, "end": v(163.6, 76.26) * mm});
            skLineSegment(sketch, "E140.27.3", {"start": v(164.52, 76.21) * mm, "end": v(164.26, 75.83) * mm});
            skLineSegment(sketch, "E140.28.0", {"start": v(163.6, 76.26) * mm, "end": v(163.14, 76.27) * mm});
            skLineSegment(sketch, "E140.28.1", {"start": v(162.9, 75.87) * mm, "end": v(162.68, 76.27) * mm});
            skLineSegment(sketch, "E140.28.2", {"start": v(162.68, 76.27) * mm, "end": v(162.22, 76.26) * mm});
            skLineSegment(sketch, "E140.28.3", {"start": v(163.14, 76.27) * mm, "end": v(162.9, 75.87) * mm});
            skLineSegment(sketch, "E140.29.0", {"start": v(162.22, 76.26) * mm, "end": v(161.76, 76.24) * mm});
            skLineSegment(sketch, "E140.29.1", {"start": v(161.55, 75.83) * mm, "end": v(161.3, 76.21) * mm});
            skLineSegment(sketch, "E140.29.2", {"start": v(161.3, 76.21) * mm, "end": v(160.84, 76.18) * mm});
            skLineSegment(sketch, "E140.29.3", {"start": v(161.76, 76.24) * mm, "end": v(161.55, 75.83) * mm});
            skLineSegment(sketch, "E140.30.0", {"start": v(160.84, 76.18) * mm, "end": v(160.38, 76.13) * mm});
            skLineSegment(sketch, "E140.30.1", {"start": v(160.2, 75.7) * mm, "end": v(159.93, 76.07) * mm});
            skLineSegment(sketch, "E140.30.2", {"start": v(159.93, 76.07) * mm, "end": v(159.47, 76) * mm});
            skLineSegment(sketch, "E140.30.3", {"start": v(160.38, 76.13) * mm, "end": v(160.2, 75.7) * mm});
            skLineSegment(sketch, "E140.31.0", {"start": v(159.47, 76) * mm, "end": v(159.02, 75.93) * mm});
            skLineSegment(sketch, "E140.31.1", {"start": v(158.87, 75.5) * mm, "end": v(158.56, 75.84) * mm});
            skLineSegment(sketch, "E140.31.2", {"start": v(158.56, 75.84) * mm, "end": v(158.11, 75.74) * mm});
            skLineSegment(sketch, "E140.31.3", {"start": v(159.02, 75.93) * mm, "end": v(158.87, 75.5) * mm});
            skLineSegment(sketch, "E140.32.0", {"start": v(158.11, 75.74) * mm, "end": v(157.67, 75.64) * mm});
            skLineSegment(sketch, "E140.32.1", {"start": v(157.54, 75.2) * mm, "end": v(157.22, 75.52) * mm});
            skLineSegment(sketch, "E140.32.2", {"start": v(157.22, 75.52) * mm, "end": v(156.78, 75.4) * mm});
            skLineSegment(sketch, "E140.32.3", {"start": v(157.67, 75.64) * mm, "end": v(157.54, 75.2) * mm});
            skLineSegment(sketch, "E140.33.0", {"start": v(156.78, 75.4) * mm, "end": v(156.34, 75.27) * mm});
            skLineSegment(sketch, "E140.33.1", {"start": v(156.24, 74.82) * mm, "end": v(155.9, 75.13) * mm});
            skLineSegment(sketch, "E140.33.2", {"start": v(155.9, 75.13) * mm, "end": v(155.47, 74.97) * mm});
            skLineSegment(sketch, "E140.33.3", {"start": v(156.34, 75.27) * mm, "end": v(156.24, 74.82) * mm});
            skLineSegment(sketch, "E140.34.0", {"start": v(155.47, 74.97) * mm, "end": v(155.03, 74.81) * mm});
            skLineSegment(sketch, "E140.34.1", {"start": v(154.97, 74.36) * mm, "end": v(154.6, 74.64) * mm});
            skLineSegment(sketch, "E140.34.2", {"start": v(154.6, 74.64) * mm, "end": v(154.18, 74.47) * mm});
            skLineSegment(sketch, "E140.34.3", {"start": v(155.03, 74.81) * mm, "end": v(154.97, 74.36) * mm});
            skLineSegment(sketch, "E140.35.0", {"start": v(154.18, 74.47) * mm, "end": v(153.76, 74.28) * mm});
            skLineSegment(sketch, "E140.35.1", {"start": v(153.72, 73.82) * mm, "end": v(153.34, 74.08) * mm});
            skLineSegment(sketch, "E140.35.2", {"start": v(153.34, 74.08) * mm, "end": v(152.93, 73.88) * mm});
            skLineSegment(sketch, "E140.35.3", {"start": v(153.76, 74.28) * mm, "end": v(153.72, 73.82) * mm});
            skLineSegment(sketch, "E140.36.0", {"start": v(152.93, 73.88) * mm, "end": v(152.53, 73.67) * mm});
            skLineSegment(sketch, "E140.36.1", {"start": v(152.52, 73.2) * mm, "end": v(152.12, 73.44) * mm});
            skLineSegment(sketch, "E140.36.2", {"start": v(152.12, 73.44) * mm, "end": v(151.72, 73.21) * mm});
            skLineSegment(sketch, "E140.36.3", {"start": v(152.53, 73.67) * mm, "end": v(152.52, 73.2) * mm});
            skLineSegment(sketch, "E140.37.0", {"start": v(151.72, 73.21) * mm, "end": v(151.33, 72.98) * mm});
            skLineSegment(sketch, "E140.37.1", {"start": v(151.35, 72.52) * mm, "end": v(150.94, 72.73) * mm});
            skLineSegment(sketch, "E140.37.2", {"start": v(150.94, 72.73) * mm, "end": v(150.56, 72.47) * mm});
            skLineSegment(sketch, "E140.37.3", {"start": v(151.33, 72.98) * mm, "end": v(151.35, 72.52) * mm});
            skLineSegment(sketch, "E140.38.0", {"start": v(150.56, 72.47) * mm, "end": v(150.18, 72.21) * mm});
            skLineSegment(sketch, "E140.38.1", {"start": v(150.23, 71.75) * mm, "end": v(149.8, 71.94) * mm});
            skLineSegment(sketch, "E140.38.2", {"start": v(149.8, 71.94) * mm, "end": v(149.44, 71.66) * mm});
            skLineSegment(sketch, "E140.38.3", {"start": v(150.18, 72.21) * mm, "end": v(150.23, 71.75) * mm});
            skLineSegment(sketch, "E140.39.0", {"start": v(149.44, 71.66) * mm, "end": v(149.08, 71.38) * mm});
            skLineSegment(sketch, "E140.39.1", {"start": v(149.16, 70.92) * mm, "end": v(148.73, 71.08) * mm});
            skLineSegment(sketch, "E140.39.2", {"start": v(148.73, 71.08) * mm, "end": v(148.38, 70.78) * mm});
            skLineSegment(sketch, "E140.39.3", {"start": v(149.08, 71.38) * mm, "end": v(149.16, 70.92) * mm});
            skLineSegment(sketch, "E140.40.0", {"start": v(148.38, 70.78) * mm, "end": v(148.04, 70.48) * mm});
            skLineSegment(sketch, "E140.40.1", {"start": v(148.14, 70.03) * mm, "end": v(147.7, 70.16) * mm});
            skLineSegment(sketch, "E140.40.2", {"start": v(147.7, 70.16) * mm, "end": v(147.37, 69.84) * mm});
            skLineSegment(sketch, "E140.40.3", {"start": v(148.04, 70.48) * mm, "end": v(148.14, 70.03) * mm});
            skLineSegment(sketch, "E140.50.0", {"start": v(141.47, 59.1) * mm, "end": v(141.37, 58.65) * mm});
            skLineSegment(sketch, "E140.50.1", {"start": v(141.72, 58.34) * mm, "end": v(141.28, 58.2) * mm});
            skLineSegment(sketch, "E140.50.2", {"start": v(141.28, 58.2) * mm, "end": v(141.2, 57.74) * mm});
            skLineSegment(sketch, "E140.50.3", {"start": v(141.37, 58.65) * mm, "end": v(141.72, 58.34) * mm});
            skLineSegment(sketch, "E140.51.0", {"start": v(141.2, 57.74) * mm, "end": v(141.14, 57.28) * mm});
            skLineSegment(sketch, "E140.51.1", {"start": v(141.5, 57) * mm, "end": v(141.08, 56.83) * mm});
            skLineSegment(sketch, "E140.51.2", {"start": v(141.08, 56.83) * mm, "end": v(141.03, 56.37) * mm});
            skLineSegment(sketch, "E140.51.3", {"start": v(141.14, 57.28) * mm, "end": v(141.5, 57) * mm});
            skLineSegment(sketch, "E140.52.0", {"start": v(141.03, 56.37) * mm, "end": v(141, 55.91) * mm});
            skLineSegment(sketch, "E140.52.1", {"start": v(141.38, 55.66) * mm, "end": v(140.97, 55.45) * mm});
            skLineSegment(sketch, "E140.52.2", {"start": v(140.97, 55.45) * mm, "end": v(140.95, 55) * mm});
            skLineSegment(sketch, "E140.52.3", {"start": v(141, 55.91) * mm, "end": v(141.38, 55.66) * mm});
            skLineSegment(sketch, "E140.53.0", {"start": v(140.95, 55) * mm, "end": v(140.94, 54.53) * mm});
            skLineSegment(sketch, "E140.53.1", {"start": v(141.34, 54.3) * mm, "end": v(140.94, 54.07) * mm});
            skLineSegment(sketch, "E140.53.2", {"start": v(140.94, 54.07) * mm, "end": v(140.95, 53.61) * mm});
            skLineSegment(sketch, "E140.53.3", {"start": v(140.94, 54.53) * mm, "end": v(141.34, 54.3) * mm});
            skLineSegment(sketch, "E140.54.0", {"start": v(140.95, 53.61) * mm, "end": v(140.97, 53.15) * mm});
            skLineSegment(sketch, "E140.54.1", {"start": v(141.38, 52.95) * mm, "end": v(141, 52.7) * mm});
            skLineSegment(sketch, "E140.54.2", {"start": v(141, 52.7) * mm, "end": v(141.03, 52.23) * mm});
            skLineSegment(sketch, "E140.54.3", {"start": v(140.97, 53.15) * mm, "end": v(141.38, 52.95) * mm});
            skLineSegment(sketch, "E140.55.0", {"start": v(141.03, 52.23) * mm, "end": v(141.08, 51.78) * mm});
            skLineSegment(sketch, "E140.55.1", {"start": v(141.5, 51.6) * mm, "end": v(141.14, 51.32) * mm});
            skLineSegment(sketch, "E140.55.2", {"start": v(141.14, 51.32) * mm, "end": v(141.2, 50.87) * mm});
            skLineSegment(sketch, "E140.55.3", {"start": v(141.08, 51.78) * mm, "end": v(141.5, 51.6) * mm});
            skLineSegment(sketch, "E140.56.0", {"start": v(141.2, 50.87) * mm, "end": v(141.28, 50.41) * mm});
            skLineSegment(sketch, "E140.56.1", {"start": v(141.72, 50.26) * mm, "end": v(141.37, 49.96) * mm});
            skLineSegment(sketch, "E140.56.2", {"start": v(141.37, 49.96) * mm, "end": v(141.47, 49.5) * mm});
            skLineSegment(sketch, "E140.56.3", {"start": v(141.28, 50.41) * mm, "end": v(141.72, 50.26) * mm});
            skLineSegment(sketch, "E140.57.0", {"start": v(141.47, 49.5) * mm, "end": v(141.57, 49.06) * mm});
            skLineSegment(sketch, "E140.57.1", {"start": v(142.01, 48.94) * mm, "end": v(141.69, 48.62) * mm});
            skLineSegment(sketch, "E140.57.2", {"start": v(141.69, 48.62) * mm, "end": v(141.8, 48.17) * mm});
            skLineSegment(sketch, "E140.57.3", {"start": v(141.57, 49.06) * mm, "end": v(142.01, 48.94) * mm});
            skLineSegment(sketch, "E140.58.0", {"start": v(141.8, 48.17) * mm, "end": v(141.94, 47.73) * mm});
            skLineSegment(sketch, "E140.58.1", {"start": v(142.4, 47.64) * mm, "end": v(142.08, 47.3) * mm});
            skLineSegment(sketch, "E140.58.2", {"start": v(142.08, 47.3) * mm, "end": v(142.24, 46.86) * mm});
            skLineSegment(sketch, "E140.58.3", {"start": v(141.94, 47.73) * mm, "end": v(142.4, 47.64) * mm});
            skLineSegment(sketch, "E140.59.0", {"start": v(142.24, 46.86) * mm, "end": v(142.4, 46.43) * mm});
            skLineSegment(sketch, "E140.59.1", {"start": v(142.85, 46.36) * mm, "end": v(142.57, 46) * mm});
            skLineSegment(sketch, "E140.59.2", {"start": v(142.57, 46) * mm, "end": v(142.74, 45.58) * mm});
            skLineSegment(sketch, "E140.59.3", {"start": v(142.4, 46.43) * mm, "end": v(142.85, 46.36) * mm});
            skLineSegment(sketch, "E140.60.0", {"start": v(142.74, 45.58) * mm, "end": v(142.93, 45.16) * mm});
            skLineSegment(sketch, "E140.60.1", {"start": v(143.39, 45.12) * mm, "end": v(143.13, 44.74) * mm});
            skLineSegment(sketch, "E140.60.2", {"start": v(143.13, 44.74) * mm, "end": v(143.33, 44.33) * mm});
            skLineSegment(sketch, "E140.60.3", {"start": v(142.93, 45.16) * mm, "end": v(143.39, 45.12) * mm});
            skLineSegment(sketch, "E140.61.0", {"start": v(143.33, 44.33) * mm, "end": v(143.54, 43.92) * mm});
            skLineSegment(sketch, "E140.61.1", {"start": v(144, 43.91) * mm, "end": v(143.77, 43.52) * mm});
            skLineSegment(sketch, "E140.61.2", {"start": v(143.77, 43.52) * mm, "end": v(144, 43.12) * mm});
            skLineSegment(sketch, "E140.61.3", {"start": v(143.54, 43.92) * mm, "end": v(144, 43.91) * mm});
            skLineSegment(sketch, "E140.62.0", {"start": v(144, 43.12) * mm, "end": v(144.23, 42.72) * mm});
            skLineSegment(sketch, "E140.62.1", {"start": v(144.7, 42.74) * mm, "end": v(144.48, 42.34) * mm});
            skLineSegment(sketch, "E140.62.2", {"start": v(144.48, 42.34) * mm, "end": v(144.74, 41.95) * mm});
            skLineSegment(sketch, "E140.62.3", {"start": v(144.23, 42.72) * mm, "end": v(144.7, 42.74) * mm});
            skLineSegment(sketch, "E140.63.0", {"start": v(144.74, 41.95) * mm, "end": v(145, 41.58) * mm});
            skLineSegment(sketch, "E140.63.1", {"start": v(145.46, 41.62) * mm, "end": v(145.27, 41.2) * mm});
            skLineSegment(sketch, "E140.63.2", {"start": v(145.27, 41.2) * mm, "end": v(145.55, 40.84) * mm});
            skLineSegment(sketch, "E140.63.3", {"start": v(145, 41.58) * mm, "end": v(145.46, 41.62) * mm});
            skLineSegment(sketch, "E140.64.0", {"start": v(145.55, 40.84) * mm, "end": v(145.83, 40.48) * mm});
            skLineSegment(sketch, "E140.64.1", {"start": v(146.29, 40.55) * mm, "end": v(146.13, 40.12) * mm});
            skLineSegment(sketch, "E140.64.2", {"start": v(146.13, 40.12) * mm, "end": v(146.43, 39.77) * mm});
            skLineSegment(sketch, "E140.64.3", {"start": v(145.83, 40.48) * mm, "end": v(146.29, 40.55) * mm});
            skLineSegment(sketch, "E140.65.0", {"start": v(146.43, 39.77) * mm, "end": v(146.73, 39.43) * mm});
            skLineSegment(sketch, "E140.65.1", {"start": v(147.18, 39.54) * mm, "end": v(147.05, 39.1) * mm});
            skLineSegment(sketch, "E140.65.2", {"start": v(147.05, 39.1) * mm, "end": v(147.37, 38.77) * mm});
            skLineSegment(sketch, "E140.65.3", {"start": v(146.73, 39.43) * mm, "end": v(147.18, 39.54) * mm});
            skLineSegment(sketch, "E140.66.0", {"start": v(147.37, 38.77) * mm, "end": v(147.7, 38.44) * mm});
            skLineSegment(sketch, "E140.66.1", {"start": v(148.14, 38.58) * mm, "end": v(148.04, 38.13) * mm});
            skLineSegment(sketch, "E140.66.2", {"start": v(148.04, 38.13) * mm, "end": v(148.38, 37.82) * mm});
            skLineSegment(sketch, "E140.66.3", {"start": v(147.7, 38.44) * mm, "end": v(148.14, 38.58) * mm});
            skLineSegment(sketch, "E140.74.0", {"start": v(156.78, 33.2) * mm, "end": v(157.22, 33.08) * mm});
            skLineSegment(sketch, "E140.74.1", {"start": v(157.54, 33.4) * mm, "end": v(157.67, 32.97) * mm});
            skLineSegment(sketch, "E140.74.2", {"start": v(157.67, 32.97) * mm, "end": v(158.11, 32.86) * mm});
            skLineSegment(sketch, "E140.74.3", {"start": v(157.22, 33.08) * mm, "end": v(157.54, 33.4) * mm});
            skLineSegment(sketch, "E140.75.0", {"start": v(158.11, 32.86) * mm, "end": v(158.56, 32.76) * mm});
            skLineSegment(sketch, "E140.75.1", {"start": v(158.87, 33.11) * mm, "end": v(159.02, 32.68) * mm});
            skLineSegment(sketch, "E140.75.2", {"start": v(159.02, 32.68) * mm, "end": v(159.47, 32.6) * mm});
            skLineSegment(sketch, "E140.75.3", {"start": v(158.56, 32.76) * mm, "end": v(158.87, 33.11) * mm});
            skLineSegment(sketch, "E140.76.0", {"start": v(159.47, 32.6) * mm, "end": v(159.93, 32.53) * mm});
            skLineSegment(sketch, "E140.76.1", {"start": v(160.2, 32.9) * mm, "end": v(160.38, 32.48) * mm});
            skLineSegment(sketch, "E140.76.2", {"start": v(160.38, 32.48) * mm, "end": v(160.84, 32.43) * mm});
            skLineSegment(sketch, "E140.76.3", {"start": v(159.93, 32.53) * mm, "end": v(160.2, 32.9) * mm});
            skLineSegment(sketch, "E140.77.0", {"start": v(160.84, 32.43) * mm, "end": v(161.3, 32.4) * mm});
            skLineSegment(sketch, "E140.77.1", {"start": v(161.55, 32.77) * mm, "end": v(161.76, 32.36) * mm});
            skLineSegment(sketch, "E140.77.2", {"start": v(161.76, 32.36) * mm, "end": v(162.22, 32.34) * mm});
            skLineSegment(sketch, "E140.77.3", {"start": v(161.3, 32.4) * mm, "end": v(161.55, 32.77) * mm});
            skLineSegment(sketch, "E140.78.0", {"start": v(162.22, 32.34) * mm, "end": v(162.68, 32.33) * mm});
            skLineSegment(sketch, "E140.78.1", {"start": v(162.9, 32.73) * mm, "end": v(163.14, 32.33) * mm});
            skLineSegment(sketch, "E140.78.2", {"start": v(163.14, 32.33) * mm, "end": v(163.6, 32.34) * mm});
            skLineSegment(sketch, "E140.78.3", {"start": v(162.68, 32.33) * mm, "end": v(162.9, 32.73) * mm});
            skLineSegment(sketch, "E140.79.0", {"start": v(163.6, 32.34) * mm, "end": v(164.06, 32.36) * mm});
            skLineSegment(sketch, "E140.79.1", {"start": v(164.26, 32.77) * mm, "end": v(164.52, 32.4) * mm});
            skLineSegment(sketch, "E140.79.2", {"start": v(164.52, 32.4) * mm, "end": v(164.98, 32.43) * mm});
            skLineSegment(sketch, "E140.79.3", {"start": v(164.06, 32.36) * mm, "end": v(164.26, 32.77) * mm});
            skLineSegment(sketch, "E140.80.0", {"start": v(164.98, 32.43) * mm, "end": v(165.43, 32.48) * mm});
            skLineSegment(sketch, "E140.80.1", {"start": v(165.61, 32.9) * mm, "end": v(165.89, 32.53) * mm});
            skLineSegment(sketch, "E140.80.2", {"start": v(165.89, 32.53) * mm, "end": v(166.34, 32.6) * mm});
            skLineSegment(sketch, "E140.80.3", {"start": v(165.43, 32.48) * mm, "end": v(165.61, 32.9) * mm});
            skLineSegment(sketch, "E140.81.0", {"start": v(166.34, 32.6) * mm, "end": v(166.8, 32.68) * mm});
            skLineSegment(sketch, "E140.81.1", {"start": v(166.95, 33.11) * mm, "end": v(167.25, 32.76) * mm});
            skLineSegment(sketch, "E140.81.2", {"start": v(167.25, 32.76) * mm, "end": v(167.7, 32.86) * mm});
            skLineSegment(sketch, "E140.81.3", {"start": v(166.8, 32.68) * mm, "end": v(166.95, 33.11) * mm});
            skLineSegment(sketch, "E140.82.0", {"start": v(167.7, 32.86) * mm, "end": v(168.15, 32.97) * mm});
            skLineSegment(sketch, "E140.82.1", {"start": v(168.27, 33.4) * mm, "end": v(168.6, 33.08) * mm});
            skLineSegment(sketch, "E140.82.2", {"start": v(168.6, 33.08) * mm, "end": v(169.04, 33.2) * mm});
            skLineSegment(sketch, "E140.82.3", {"start": v(168.15, 32.97) * mm, "end": v(168.27, 33.4) * mm});
            skLineSegment(sketch, "E140.83.0", {"start": v(169.04, 33.2) * mm, "end": v(169.48, 33.34) * mm});
            skLineSegment(sketch, "E140.83.1", {"start": v(169.57, 33.79) * mm, "end": v(169.92, 33.48) * mm});
            skLineSegment(sketch, "E140.83.2", {"start": v(169.92, 33.48) * mm, "end": v(170.35, 33.63) * mm});
            skLineSegment(sketch, "E140.83.3", {"start": v(169.48, 33.34) * mm, "end": v(169.57, 33.79) * mm});
            skLineSegment(sketch, "E140.84.0", {"start": v(170.35, 33.63) * mm, "end": v(170.78, 33.8) * mm});
            skLineSegment(sketch, "E140.84.1", {"start": v(170.85, 34.25) * mm, "end": v(171.2, 33.96) * mm});
            skLineSegment(sketch, "E140.84.2", {"start": v(171.2, 33.96) * mm, "end": v(171.63, 34.14) * mm});
            skLineSegment(sketch, "E140.84.3", {"start": v(170.78, 33.8) * mm, "end": v(170.85, 34.25) * mm});
            skLineSegment(sketch, "E140.85.0", {"start": v(171.63, 34.14) * mm, "end": v(172.05, 34.33) * mm});
            skLineSegment(sketch, "E140.85.1", {"start": v(172.1, 34.78) * mm, "end": v(172.47, 34.52) * mm});
            skLineSegment(sketch, "E140.85.2", {"start": v(172.47, 34.52) * mm, "end": v(172.88, 34.73) * mm});
            skLineSegment(sketch, "E140.85.3", {"start": v(172.05, 34.33) * mm, "end": v(172.1, 34.78) * mm});
            skLineSegment(sketch, "E140.86.0", {"start": v(172.88, 34.73) * mm, "end": v(173.29, 34.94) * mm});
            skLineSegment(sketch, "E140.86.1", {"start": v(173.3, 35.4) * mm, "end": v(173.7, 35.16) * mm});
            skLineSegment(sketch, "E140.86.2", {"start": v(173.7, 35.16) * mm, "end": v(174.1, 35.4) * mm});
            skLineSegment(sketch, "E140.86.3", {"start": v(173.29, 34.94) * mm, "end": v(173.3, 35.4) * mm});
            skLineSegment(sketch, "E140.87.0", {"start": v(174.1, 35.4) * mm, "end": v(174.49, 35.63) * mm});
            skLineSegment(sketch, "E140.87.1", {"start": v(174.47, 36.09) * mm, "end": v(174.87, 35.88) * mm});
            skLineSegment(sketch, "E140.87.2", {"start": v(174.87, 35.88) * mm, "end": v(175.26, 36.13) * mm});
            skLineSegment(sketch, "E140.87.3", {"start": v(174.49, 35.63) * mm, "end": v(174.47, 36.09) * mm});
            skLineSegment(sketch, "E140.88.0", {"start": v(175.26, 36.13) * mm, "end": v(175.63, 36.4) * mm});
            skLineSegment(sketch, "E140.88.1", {"start": v(175.59, 36.85) * mm, "end": v(176, 36.66) * mm});
            skLineSegment(sketch, "E140.88.2", {"start": v(176, 36.66) * mm, "end": v(176.37, 36.94) * mm});
            skLineSegment(sketch, "E140.88.3", {"start": v(175.63, 36.4) * mm, "end": v(175.59, 36.85) * mm});
            skLineSegment(sketch, "E140.89.0", {"start": v(176.37, 36.94) * mm, "end": v(176.73, 37.23) * mm});
            skLineSegment(sketch, "E140.89.1", {"start": v(176.66, 37.68) * mm, "end": v(177.09, 37.52) * mm});
            skLineSegment(sketch, "E140.89.2", {"start": v(177.09, 37.52) * mm, "end": v(177.44, 37.82) * mm});
            skLineSegment(sketch, "E140.89.3", {"start": v(176.73, 37.23) * mm, "end": v(176.66, 37.68) * mm});
            skLineSegment(sketch, "E140.90.0", {"start": v(177.44, 37.82) * mm, "end": v(177.78, 38.13) * mm});
            skLineSegment(sketch, "E140.90.1", {"start": v(177.67, 38.58) * mm, "end": v(178.11, 38.44) * mm});
            skLineSegment(sketch, "E140.90.2", {"start": v(178.11, 38.44) * mm, "end": v(178.44, 38.77) * mm});
            skLineSegment(sketch, "E140.90.3", {"start": v(177.78, 38.13) * mm, "end": v(177.67, 38.58) * mm});
            skPoint(sketch, "E140.center", {"position": v(162.9, 54.3) * mm});
            skLineSegment(sketch, "E140.anchor2", {"start": v(162.9, 54.3) * mm, "end": v(177.44, 37.82) * mm, "construction": true});
            skArc(sketch, "E141", {"start": v(141.47, 59.1) * mm, "mid": v(142.01, 47.51) * mm, "end": v(148.38, 37.82) * mm, "construction": true});
            skArc(sketch, "E142", {"start": v(147.37, 69.84) * mm, "mid": v(143.65, 64.89) * mm, "end": v(141.47, 59.1) * mm});
            skArc(sketch, "E143", {"start": v(177.44, 70.78) * mm, "mid": v(173.5, 73.56) * mm, "end": v(169.04, 75.4) * mm});
            skArc(sketch, "E144", {"start": v(178.44, 38.77) * mm, "mid": v(182.16, 43.72) * mm, "end": v(184.35, 49.5) * mm});
            skArc(sketch, "E145", {"start": v(148.38, 37.82) * mm, "mid": v(152.32, 35.05) * mm, "end": v(156.78, 33.2) * mm});
            skLineSegment(sketch, "E146", {"start": v(166.4, 0) * mm, "end": v(217.2, 0) * mm, "construction": true});
            skLineSegment(sketch, "E147", {"start": v(217.2, 0) * mm, "end": v(238.65, -4.8) * mm, "construction": true});
            skLineSegment(sketch, "E148", {"start": v(217.2, 0) * mm, "end": v(238.75, -4.34) * mm, "construction": true});
            skLineSegment(sketch, "E149", {"start": v(217.2, 0) * mm, "end": v(238.83, -3.9) * mm, "construction": true});
            skLineSegment(sketch, "E150", {"start": v(217.2, 0) * mm, "end": v(238.91, -3.44) * mm, "construction": true});
            skLineSegment(sketch, "E151", {"start": v(238.65, -4.8) * mm, "end": v(238.75, -4.34) * mm});
            skLineSegment(sketch, "E152", {"start": v(238.75, -4.34) * mm, "end": v(238.4, -4.04) * mm});
            skLineSegment(sketch, "E153", {"start": v(238.4, -4.04) * mm, "end": v(238.83, -3.9) * mm});
            skLineSegment(sketch, "E154", {"start": v(238.83, -3.9) * mm, "end": v(238.91, -3.44) * mm});
            skLineSegment(sketch, "E155", {"start": v(217.2, 0) * mm, "end": v(217.2, -21.97) * mm, "construction": true});
            skLineSegment(sketch, "E156.1.0", {"start": v(238.91, -3.44) * mm, "end": v(238.98, -2.98) * mm});
            skLineSegment(sketch, "E156.1.1", {"start": v(238.61, -2.7) * mm, "end": v(239.04, -2.53) * mm});
            skLineSegment(sketch, "E156.1.2", {"start": v(239.04, -2.53) * mm, "end": v(239.08, -2.07) * mm});
            skLineSegment(sketch, "E156.1.3", {"start": v(238.98, -2.98) * mm, "end": v(238.61, -2.7) * mm});
            skLineSegment(sketch, "E156.2.0", {"start": v(239.08, -2.07) * mm, "end": v(239.12, -1.6) * mm});
            skLineSegment(sketch, "E156.2.1", {"start": v(238.74, -1.35) * mm, "end": v(239.15, -1.15) * mm});
            skLineSegment(sketch, "E156.2.2", {"start": v(239.15, -1.15) * mm, "end": v(239.17, -0.7) * mm});
            skLineSegment(sketch, "E156.2.3", {"start": v(239.12, -1.6) * mm, "end": v(238.74, -1.35) * mm});
            skLineSegment(sketch, "E156.3.0", {"start": v(239.17, -0.7) * mm, "end": v(239.18, -0.23) * mm});
            skLineSegment(sketch, "E156.3.1", {"start": v(238.78, 0) * mm, "end": v(239.18, 0.23) * mm});
            skLineSegment(sketch, "E156.3.2", {"start": v(239.18, 0.23) * mm, "end": v(239.17, 0.7) * mm});
            skLineSegment(sketch, "E156.3.3", {"start": v(239.18, -0.23) * mm, "end": v(238.78, 0) * mm});
            skLineSegment(sketch, "E156.4.0", {"start": v(239.17, 0.7) * mm, "end": v(239.15, 1.15) * mm});
            skLineSegment(sketch, "E156.4.1", {"start": v(238.74, 1.35) * mm, "end": v(239.12, 1.6) * mm});
            skLineSegment(sketch, "E156.4.2", {"start": v(239.12, 1.6) * mm, "end": v(239.08, 2.07) * mm});
            skLineSegment(sketch, "E156.4.3", {"start": v(239.15, 1.15) * mm, "end": v(238.74, 1.35) * mm});
            skLineSegment(sketch, "E156.5.0", {"start": v(239.08, 2.07) * mm, "end": v(239.04, 2.53) * mm});
            skLineSegment(sketch, "E156.5.1", {"start": v(238.61, 2.7) * mm, "end": v(238.98, 2.98) * mm});
            skLineSegment(sketch, "E156.5.2", {"start": v(238.98, 2.98) * mm, "end": v(238.91, 3.44) * mm});
            skLineSegment(sketch, "E156.5.3", {"start": v(239.04, 2.53) * mm, "end": v(238.61, 2.7) * mm});
            skLineSegment(sketch, "E156.6.0", {"start": v(238.91, 3.44) * mm, "end": v(238.83, 3.9) * mm});
            skLineSegment(sketch, "E156.6.1", {"start": v(238.4, 4.04) * mm, "end": v(238.75, 4.34) * mm});
            skLineSegment(sketch, "E156.6.2", {"start": v(238.75, 4.34) * mm, "end": v(238.65, 4.8) * mm});
            skLineSegment(sketch, "E156.6.3", {"start": v(238.83, 3.9) * mm, "end": v(238.4, 4.04) * mm});
            skLineSegment(sketch, "E156.7.0", {"start": v(238.65, 4.8) * mm, "end": v(238.55, 5.24) * mm});
            skLineSegment(sketch, "E156.7.1", {"start": v(238.1, 5.36) * mm, "end": v(238.43, 5.69) * mm});
            skLineSegment(sketch, "E156.7.2", {"start": v(238.43, 5.69) * mm, "end": v(238.3, 6.13) * mm});
            skLineSegment(sketch, "E156.7.3", {"start": v(238.55, 5.24) * mm, "end": v(238.1, 5.36) * mm});
            skLineSegment(sketch, "E156.8.0", {"start": v(238.3, 6.13) * mm, "end": v(238.18, 6.57) * mm});
            skLineSegment(sketch, "E156.8.1", {"start": v(237.73, 6.67) * mm, "end": v(238.03, 7) * mm});
            skLineSegment(sketch, "E156.8.2", {"start": v(238.03, 7) * mm, "end": v(237.88, 7.44) * mm});
            skLineSegment(sketch, "E156.8.3", {"start": v(238.18, 6.57) * mm, "end": v(237.73, 6.67) * mm});
            skLineSegment(sketch, "E156.9.0", {"start": v(237.88, 7.44) * mm, "end": v(237.72, 7.87) * mm});
            skLineSegment(sketch, "E156.9.1", {"start": v(237.27, 7.94) * mm, "end": v(237.55, 8.3) * mm});
            skLineSegment(sketch, "E156.9.2", {"start": v(237.55, 8.3) * mm, "end": v(237.37, 8.73) * mm});
            skLineSegment(sketch, "E156.9.3", {"start": v(237.72, 7.87) * mm, "end": v(237.27, 7.94) * mm});
            skLineSegment(sketch, "E156.10.0", {"start": v(237.37, 8.73) * mm, "end": v(237.19, 9.15) * mm});
            skLineSegment(sketch, "E156.10.1", {"start": v(236.73, 9.18) * mm, "end": v(237, 9.56) * mm});
            skLineSegment(sketch, "E156.10.2", {"start": v(237, 9.56) * mm, "end": v(236.79, 9.97) * mm});
            skLineSegment(sketch, "E156.10.3", {"start": v(237.19, 9.15) * mm, "end": v(236.73, 9.18) * mm});
            skLineSegment(sketch, "E156.11.0", {"start": v(236.79, 9.97) * mm, "end": v(236.57, 10.38) * mm});
            skLineSegment(sketch, "E156.11.1", {"start": v(236.11, 10.4) * mm, "end": v(236.35, 10.79) * mm});
            skLineSegment(sketch, "E156.11.2", {"start": v(236.35, 10.79) * mm, "end": v(236.12, 11.18) * mm});
            skLineSegment(sketch, "E156.11.3", {"start": v(236.57, 10.38) * mm, "end": v(236.11, 10.4) * mm});
            skLineSegment(sketch, "E156.12.0", {"start": v(236.12, 11.18) * mm, "end": v(235.88, 11.58) * mm});
            skLineSegment(sketch, "E156.12.1", {"start": v(235.42, 11.56) * mm, "end": v(235.64, 11.97) * mm});
            skLineSegment(sketch, "E156.12.2", {"start": v(235.64, 11.97) * mm, "end": v(235.38, 12.35) * mm});
            skLineSegment(sketch, "E156.12.3", {"start": v(235.88, 11.58) * mm, "end": v(235.42, 11.56) * mm});
            skLineSegment(sketch, "E156.13.0", {"start": v(235.38, 12.35) * mm, "end": v(235.12, 12.73) * mm});
            skLineSegment(sketch, "E156.13.1", {"start": v(234.66, 12.68) * mm, "end": v(234.85, 13.1) * mm});
            skLineSegment(sketch, "E156.13.2", {"start": v(234.85, 13.1) * mm, "end": v(234.57, 13.47) * mm});
            skLineSegment(sketch, "E156.13.3", {"start": v(235.12, 12.73) * mm, "end": v(234.66, 12.68) * mm});
            skLineSegment(sketch, "E156.14.0", {"start": v(234.57, 13.47) * mm, "end": v(234.28, 13.83) * mm});
            skLineSegment(sketch, "E156.14.1", {"start": v(233.83, 13.75) * mm, "end": v(234, 14.18) * mm});
            skLineSegment(sketch, "E156.14.2", {"start": v(234, 14.18) * mm, "end": v(233.7, 14.53) * mm});
            skLineSegment(sketch, "E156.14.3", {"start": v(234.28, 13.83) * mm, "end": v(233.83, 13.75) * mm});
            skLineSegment(sketch, "E156.15.0", {"start": v(233.7, 14.53) * mm, "end": v(233.38, 14.87) * mm});
            skLineSegment(sketch, "E156.15.1", {"start": v(232.93, 14.77) * mm, "end": v(233.07, 15.2) * mm});
            skLineSegment(sketch, "E156.15.2", {"start": v(233.07, 15.2) * mm, "end": v(232.75, 15.54) * mm});
            skLineSegment(sketch, "E156.15.3", {"start": v(233.38, 14.87) * mm, "end": v(232.93, 14.77) * mm});
            skLineSegment(sketch, "E156.16.0", {"start": v(232.75, 15.54) * mm, "end": v(232.42, 15.86) * mm});
            skLineSegment(sketch, "E156.16.1", {"start": v(231.98, 15.72) * mm, "end": v(232.08, 16.17) * mm});
            skLineSegment(sketch, "E156.16.2", {"start": v(232.08, 16.17) * mm, "end": v(231.74, 16.48) * mm});
            skLineSegment(sketch, "E156.16.3", {"start": v(232.42, 15.86) * mm, "end": v(231.98, 15.72) * mm});
            skLineSegment(sketch, "E156.24.0", {"start": v(223.34, 21.1) * mm, "end": v(222.9, 21.22) * mm});
            skLineSegment(sketch, "E156.24.1", {"start": v(222.57, 20.9) * mm, "end": v(222.45, 21.34) * mm});
            skLineSegment(sketch, "E156.24.2", {"start": v(222.45, 21.34) * mm, "end": v(222, 21.44) * mm});
            skLineSegment(sketch, "E156.24.3", {"start": v(222.9, 21.22) * mm, "end": v(222.57, 20.9) * mm});
            skLineSegment(sketch, "E156.25.0", {"start": v(222, 21.44) * mm, "end": v(221.55, 21.54) * mm});
            skLineSegment(sketch, "E156.25.1", {"start": v(221.25, 21.19) * mm, "end": v(221.1, 21.62) * mm});
            skLineSegment(sketch, "E156.25.2", {"start": v(221.1, 21.62) * mm, "end": v(220.65, 21.7) * mm});
            skLineSegment(sketch, "E156.25.3", {"start": v(221.55, 21.54) * mm, "end": v(221.25, 21.19) * mm});
            skLineSegment(sketch, "E156.26.0", {"start": v(220.65, 21.7) * mm, "end": v(220.2, 21.77) * mm});
            skLineSegment(sketch, "E156.26.1", {"start": v(219.91, 21.4) * mm, "end": v(219.74, 21.83) * mm});
            skLineSegment(sketch, "E156.26.2", {"start": v(219.74, 21.83) * mm, "end": v(219.28, 21.87) * mm});
            skLineSegment(sketch, "E156.26.3", {"start": v(220.2, 21.77) * mm, "end": v(219.91, 21.4) * mm});
            skLineSegment(sketch, "E156.27.0", {"start": v(219.28, 21.87) * mm, "end": v(218.82, 21.91) * mm});
            skLineSegment(sketch, "E156.27.1", {"start": v(218.56, 21.53) * mm, "end": v(218.36, 21.94) * mm});
            skLineSegment(sketch, "E156.27.2", {"start": v(218.36, 21.94) * mm, "end": v(217.9, 21.96) * mm});
            skLineSegment(sketch, "E156.27.3", {"start": v(218.82, 21.91) * mm, "end": v(218.56, 21.53) * mm});
            skLineSegment(sketch, "E156.28.0", {"start": v(217.9, 21.96) * mm, "end": v(217.44, 21.97) * mm});
            skLineSegment(sketch, "E156.28.1", {"start": v(217.2, 21.57) * mm, "end": v(216.98, 21.97) * mm});
            skLineSegment(sketch, "E156.28.2", {"start": v(216.98, 21.97) * mm, "end": v(216.52, 21.96) * mm});
            skLineSegment(sketch, "E156.28.3", {"start": v(217.44, 21.97) * mm, "end": v(217.2, 21.57) * mm});
            skLineSegment(sketch, "E156.29.0", {"start": v(216.52, 21.96) * mm, "end": v(216.06, 21.94) * mm});
            skLineSegment(sketch, "E156.29.1", {"start": v(215.86, 21.53) * mm, "end": v(215.6, 21.91) * mm});
            skLineSegment(sketch, "E156.29.2", {"start": v(215.6, 21.91) * mm, "end": v(215.14, 21.87) * mm});
            skLineSegment(sketch, "E156.29.3", {"start": v(216.06, 21.94) * mm, "end": v(215.86, 21.53) * mm});
            skLineSegment(sketch, "E156.30.0", {"start": v(215.14, 21.87) * mm, "end": v(214.68, 21.83) * mm});
            skLineSegment(sketch, "E156.30.1", {"start": v(214.5, 21.4) * mm, "end": v(214.23, 21.77) * mm});
            skLineSegment(sketch, "E156.30.2", {"start": v(214.23, 21.77) * mm, "end": v(213.77, 21.7) * mm});
            skLineSegment(sketch, "E156.30.3", {"start": v(214.68, 21.83) * mm, "end": v(214.5, 21.4) * mm});
            skLineSegment(sketch, "E156.31.0", {"start": v(213.77, 21.7) * mm, "end": v(213.32, 21.62) * mm});
            skLineSegment(sketch, "E156.31.1", {"start": v(213.17, 21.19) * mm, "end": v(212.87, 21.54) * mm});
            skLineSegment(sketch, "E156.31.2", {"start": v(212.87, 21.54) * mm, "end": v(212.42, 21.44) * mm});
            skLineSegment(sketch, "E156.31.3", {"start": v(213.32, 21.62) * mm, "end": v(213.17, 21.19) * mm});
            skLineSegment(sketch, "E156.32.0", {"start": v(212.42, 21.44) * mm, "end": v(211.97, 21.34) * mm});
            skLineSegment(sketch, "E156.32.1", {"start": v(211.85, 20.9) * mm, "end": v(211.52, 21.22) * mm});
            skLineSegment(sketch, "E156.32.2", {"start": v(211.52, 21.22) * mm, "end": v(211.08, 21.1) * mm});
            skLineSegment(sketch, "E156.32.3", {"start": v(211.97, 21.34) * mm, "end": v(211.85, 20.9) * mm});
            skLineSegment(sketch, "E156.33.0", {"start": v(211.08, 21.1) * mm, "end": v(210.64, 20.97) * mm});
            skLineSegment(sketch, "E156.33.1", {"start": v(210.54, 20.52) * mm, "end": v(210.2, 20.82) * mm});
            skLineSegment(sketch, "E156.33.2", {"start": v(210.2, 20.82) * mm, "end": v(209.77, 20.67) * mm});
            skLineSegment(sketch, "E156.33.3", {"start": v(210.64, 20.97) * mm, "end": v(210.54, 20.52) * mm});
            skLineSegment(sketch, "E156.34.0", {"start": v(209.77, 20.67) * mm, "end": v(209.34, 20.51) * mm});
            skLineSegment(sketch, "E156.34.1", {"start": v(209.27, 20.06) * mm, "end": v(208.9, 20.34) * mm});
            skLineSegment(sketch, "E156.34.2", {"start": v(208.9, 20.34) * mm, "end": v(208.48, 20.16) * mm});
            skLineSegment(sketch, "E156.34.3", {"start": v(209.34, 20.51) * mm, "end": v(209.27, 20.06) * mm});
            skLineSegment(sketch, "E156.35.0", {"start": v(208.48, 20.16) * mm, "end": v(208.06, 19.98) * mm});
            skLineSegment(sketch, "E156.35.1", {"start": v(208.03, 19.52) * mm, "end": v(207.65, 19.78) * mm});
            skLineSegment(sketch, "E156.35.2", {"start": v(207.65, 19.78) * mm, "end": v(207.24, 19.58) * mm});
            skLineSegment(sketch, "E156.35.3", {"start": v(208.06, 19.98) * mm, "end": v(208.03, 19.52) * mm});
            skLineSegment(sketch, "E156.36.0", {"start": v(207.24, 19.58) * mm, "end": v(206.83, 19.36) * mm});
            skLineSegment(sketch, "E156.36.1", {"start": v(206.82, 18.9) * mm, "end": v(206.42, 19.14) * mm});
            skLineSegment(sketch, "E156.36.2", {"start": v(206.42, 19.14) * mm, "end": v(206.03, 18.91) * mm});
            skLineSegment(sketch, "E156.36.3", {"start": v(206.83, 19.36) * mm, "end": v(206.82, 18.9) * mm});
            skLineSegment(sketch, "E156.37.0", {"start": v(206.03, 18.91) * mm, "end": v(205.63, 18.67) * mm});
            skLineSegment(sketch, "E156.37.1", {"start": v(205.65, 18.21) * mm, "end": v(205.24, 18.43) * mm});
            skLineSegment(sketch, "E156.37.2", {"start": v(205.24, 18.43) * mm, "end": v(204.86, 18.17) * mm});
            skLineSegment(sketch, "E156.37.3", {"start": v(205.63, 18.67) * mm, "end": v(205.65, 18.21) * mm});
            skLineSegment(sketch, "E156.38.0", {"start": v(204.86, 18.17) * mm, "end": v(204.48, 17.9) * mm});
            skLineSegment(sketch, "E156.38.1", {"start": v(204.53, 17.45) * mm, "end": v(204.11, 17.64) * mm});
            skLineSegment(sketch, "E156.38.2", {"start": v(204.11, 17.64) * mm, "end": v(203.74, 17.36) * mm});
            skLineSegment(sketch, "E156.38.3", {"start": v(204.48, 17.9) * mm, "end": v(204.53, 17.45) * mm});
            skLineSegment(sketch, "E156.39.0", {"start": v(203.74, 17.36) * mm, "end": v(203.38, 17.07) * mm});
            skLineSegment(sketch, "E156.39.1", {"start": v(203.46, 16.62) * mm, "end": v(203.03, 16.78) * mm});
            skLineSegment(sketch, "E156.39.2", {"start": v(203.03, 16.78) * mm, "end": v(202.68, 16.48) * mm});
            skLineSegment(sketch, "E156.39.3", {"start": v(203.38, 17.07) * mm, "end": v(203.46, 16.62) * mm});
            skLineSegment(sketch, "E156.40.0", {"start": v(202.68, 16.48) * mm, "end": v(202.34, 16.17) * mm});
            skLineSegment(sketch, "E156.40.1", {"start": v(202.44, 15.72) * mm, "end": v(202, 15.86) * mm});
            skLineSegment(sketch, "E156.40.2", {"start": v(202, 15.86) * mm, "end": v(201.67, 15.54) * mm});
            skLineSegment(sketch, "E156.40.3", {"start": v(202.34, 16.17) * mm, "end": v(202.44, 15.72) * mm});
            skLineSegment(sketch, "E156.50.0", {"start": v(195.77, 4.8) * mm, "end": v(195.67, 4.34) * mm});
            skLineSegment(sketch, "E156.50.1", {"start": v(196.02, 4.04) * mm, "end": v(195.59, 3.9) * mm});
            skLineSegment(sketch, "E156.50.2", {"start": v(195.59, 3.9) * mm, "end": v(195.5, 3.44) * mm});
            skLineSegment(sketch, "E156.50.3", {"start": v(195.67, 4.34) * mm, "end": v(196.02, 4.04) * mm});
            skLineSegment(sketch, "E156.51.0", {"start": v(195.5, 3.44) * mm, "end": v(195.44, 2.98) * mm});
            skLineSegment(sketch, "E156.51.1", {"start": v(195.8, 2.7) * mm, "end": v(195.38, 2.53) * mm});
            skLineSegment(sketch, "E156.51.2", {"start": v(195.38, 2.53) * mm, "end": v(195.34, 2.07) * mm});
            skLineSegment(sketch, "E156.51.3", {"start": v(195.44, 2.98) * mm, "end": v(195.8, 2.7) * mm});
            skLineSegment(sketch, "E156.52.0", {"start": v(195.34, 2.07) * mm, "end": v(195.3, 1.6) * mm});
            skLineSegment(sketch, "E156.52.1", {"start": v(195.68, 1.35) * mm, "end": v(195.27, 1.15) * mm});
            skLineSegment(sketch, "E156.52.2", {"start": v(195.27, 1.15) * mm, "end": v(195.25, 0.7) * mm});
            skLineSegment(sketch, "E156.52.3", {"start": v(195.3, 1.6) * mm, "end": v(195.68, 1.35) * mm});
            skLineSegment(sketch, "E156.53.0", {"start": v(195.25, 0.7) * mm, "end": v(195.24, 0.23) * mm});
            skLineSegment(sketch, "E156.53.1", {"start": v(195.64, 0) * mm, "end": v(195.24, -0.23) * mm});
            skLineSegment(sketch, "E156.53.2", {"start": v(195.24, -0.23) * mm, "end": v(195.25, -0.7) * mm});
            skLineSegment(sketch, "E156.53.3", {"start": v(195.24, 0.23) * mm, "end": v(195.64, 0) * mm});
            skLineSegment(sketch, "E156.54.0", {"start": v(195.25, -0.7) * mm, "end": v(195.27, -1.15) * mm});
            skLineSegment(sketch, "E156.54.1", {"start": v(195.68, -1.35) * mm, "end": v(195.3, -1.6) * mm});
            skLineSegment(sketch, "E156.54.2", {"start": v(195.3, -1.6) * mm, "end": v(195.34, -2.07) * mm});
            skLineSegment(sketch, "E156.54.3", {"start": v(195.27, -1.15) * mm, "end": v(195.68, -1.35) * mm});
            skLineSegment(sketch, "E156.55.0", {"start": v(195.34, -2.07) * mm, "end": v(195.38, -2.53) * mm});
            skLineSegment(sketch, "E156.55.1", {"start": v(195.8, -2.7) * mm, "end": v(195.44, -2.98) * mm});
            skLineSegment(sketch, "E156.55.2", {"start": v(195.44, -2.98) * mm, "end": v(195.5, -3.44) * mm});
            skLineSegment(sketch, "E156.55.3", {"start": v(195.38, -2.53) * mm, "end": v(195.8, -2.7) * mm});
            skLineSegment(sketch, "E156.56.0", {"start": v(195.5, -3.44) * mm, "end": v(195.59, -3.9) * mm});
            skLineSegment(sketch, "E156.56.1", {"start": v(196.02, -4.04) * mm, "end": v(195.67, -4.34) * mm});
            skLineSegment(sketch, "E156.56.2", {"start": v(195.67, -4.34) * mm, "end": v(195.77, -4.8) * mm});
            skLineSegment(sketch, "E156.56.3", {"start": v(195.59, -3.9) * mm, "end": v(196.02, -4.04) * mm});
            skLineSegment(sketch, "E156.57.0", {"start": v(195.77, -4.8) * mm, "end": v(195.87, -5.24) * mm});
            skLineSegment(sketch, "E156.57.1", {"start": v(196.32, -5.36) * mm, "end": v(195.99, -5.69) * mm});
            skLineSegment(sketch, "E156.57.2", {"start": v(195.99, -5.69) * mm, "end": v(196.11, -6.13) * mm});
            skLineSegment(sketch, "E156.57.3", {"start": v(195.87, -5.24) * mm, "end": v(196.32, -5.36) * mm});
            skLineSegment(sketch, "E156.58.0", {"start": v(196.11, -6.13) * mm, "end": v(196.24, -6.57) * mm});
            skLineSegment(sketch, "E156.58.1", {"start": v(196.7, -6.67) * mm, "end": v(196.39, -7) * mm});
            skLineSegment(sketch, "E156.58.2", {"start": v(196.39, -7) * mm, "end": v(196.54, -7.44) * mm});
            skLineSegment(sketch, "E156.58.3", {"start": v(196.24, -6.57) * mm, "end": v(196.7, -6.67) * mm});
            skLineSegment(sketch, "E156.59.0", {"start": v(196.54, -7.44) * mm, "end": v(196.7, -7.87) * mm});
            skLineSegment(sketch, "E156.59.1", {"start": v(197.15, -7.94) * mm, "end": v(196.87, -8.3) * mm});
            skLineSegment(sketch, "E156.59.2", {"start": v(196.87, -8.3) * mm, "end": v(197.05, -8.73) * mm});
            skLineSegment(sketch, "E156.59.3", {"start": v(196.7, -7.87) * mm, "end": v(197.15, -7.94) * mm});
            skLineSegment(sketch, "E156.60.0", {"start": v(197.05, -8.73) * mm, "end": v(197.23, -9.15) * mm});
            skLineSegment(sketch, "E156.60.1", {"start": v(197.7, -9.18) * mm, "end": v(197.43, -9.56) * mm});
            skLineSegment(sketch, "E156.60.2", {"start": v(197.43, -9.56) * mm, "end": v(197.63, -9.97) * mm});
            skLineSegment(sketch, "E156.60.3", {"start": v(197.23, -9.15) * mm, "end": v(197.7, -9.18) * mm});
            skLineSegment(sketch, "E156.61.0", {"start": v(197.63, -9.97) * mm, "end": v(197.85, -10.38) * mm});
            skLineSegment(sketch, "E156.61.1", {"start": v(198.3, -10.4) * mm, "end": v(198.07, -10.79) * mm});
            skLineSegment(sketch, "E156.61.2", {"start": v(198.07, -10.79) * mm, "end": v(198.3, -11.18) * mm});
            skLineSegment(sketch, "E156.61.3", {"start": v(197.85, -10.38) * mm, "end": v(198.3, -10.4) * mm});
            skLineSegment(sketch, "E156.62.0", {"start": v(198.3, -11.18) * mm, "end": v(198.54, -11.58) * mm});
            skLineSegment(sketch, "E156.62.1", {"start": v(199, -11.56) * mm, "end": v(198.78, -11.97) * mm});
            skLineSegment(sketch, "E156.62.2", {"start": v(198.78, -11.97) * mm, "end": v(199.04, -12.35) * mm});
            skLineSegment(sketch, "E156.62.3", {"start": v(198.54, -11.58) * mm, "end": v(199, -11.56) * mm});
            skLineSegment(sketch, "E156.63.0", {"start": v(199.04, -12.35) * mm, "end": v(199.3, -12.73) * mm});
            skLineSegment(sketch, "E156.63.1", {"start": v(199.76, -12.68) * mm, "end": v(199.57, -13.1) * mm});
            skLineSegment(sketch, "E156.63.2", {"start": v(199.57, -13.1) * mm, "end": v(199.85, -13.47) * mm});
            skLineSegment(sketch, "E156.63.3", {"start": v(199.3, -12.73) * mm, "end": v(199.76, -12.68) * mm});
            skLineSegment(sketch, "E156.64.0", {"start": v(199.85, -13.47) * mm, "end": v(200.14, -13.83) * mm});
            skLineSegment(sketch, "E156.64.1", {"start": v(200.59, -13.75) * mm, "end": v(200.43, -14.18) * mm});
            skLineSegment(sketch, "E156.64.2", {"start": v(200.43, -14.18) * mm, "end": v(200.73, -14.53) * mm});
            skLineSegment(sketch, "E156.64.3", {"start": v(200.14, -13.83) * mm, "end": v(200.59, -13.75) * mm});
            skLineSegment(sketch, "E156.65.0", {"start": v(200.73, -14.53) * mm, "end": v(201.04, -14.87) * mm});
            skLineSegment(sketch, "E156.65.1", {"start": v(201.49, -14.77) * mm, "end": v(201.35, -15.2) * mm});
            skLineSegment(sketch, "E156.65.2", {"start": v(201.35, -15.2) * mm, "end": v(201.67, -15.54) * mm});
            skLineSegment(sketch, "E156.65.3", {"start": v(201.04, -14.87) * mm, "end": v(201.49, -14.77) * mm});
            skLineSegment(sketch, "E156.66.0", {"start": v(201.67, -15.54) * mm, "end": v(202, -15.86) * mm});
            skLineSegment(sketch, "E156.66.1", {"start": v(202.44, -15.72) * mm, "end": v(202.34, -16.17) * mm});
            skLineSegment(sketch, "E156.66.2", {"start": v(202.34, -16.17) * mm, "end": v(202.68, -16.48) * mm});
            skLineSegment(sketch, "E156.66.3", {"start": v(202, -15.86) * mm, "end": v(202.44, -15.72) * mm});
            skLineSegment(sketch, "E156.74.0", {"start": v(211.08, -21.1) * mm, "end": v(211.52, -21.22) * mm});
            skLineSegment(sketch, "E156.74.1", {"start": v(211.85, -20.9) * mm, "end": v(211.97, -21.34) * mm});
            skLineSegment(sketch, "E156.74.2", {"start": v(211.97, -21.34) * mm, "end": v(212.42, -21.44) * mm});
            skLineSegment(sketch, "E156.74.3", {"start": v(211.52, -21.22) * mm, "end": v(211.85, -20.9) * mm});
            skLineSegment(sketch, "E156.75.0", {"start": v(212.42, -21.44) * mm, "end": v(212.87, -21.54) * mm});
            skLineSegment(sketch, "E156.75.1", {"start": v(213.17, -21.19) * mm, "end": v(213.32, -21.62) * mm});
            skLineSegment(sketch, "E156.75.2", {"start": v(213.32, -21.62) * mm, "end": v(213.77, -21.7) * mm});
            skLineSegment(sketch, "E156.75.3", {"start": v(212.87, -21.54) * mm, "end": v(213.17, -21.19) * mm});
            skLineSegment(sketch, "E156.76.0", {"start": v(213.77, -21.7) * mm, "end": v(214.23, -21.77) * mm});
            skLineSegment(sketch, "E156.76.1", {"start": v(214.5, -21.4) * mm, "end": v(214.68, -21.83) * mm});
            skLineSegment(sketch, "E156.76.2", {"start": v(214.68, -21.83) * mm, "end": v(215.14, -21.87) * mm});
            skLineSegment(sketch, "E156.76.3", {"start": v(214.23, -21.77) * mm, "end": v(214.5, -21.4) * mm});
            skLineSegment(sketch, "E156.77.0", {"start": v(215.14, -21.87) * mm, "end": v(215.6, -21.91) * mm});
            skLineSegment(sketch, "E156.77.1", {"start": v(215.86, -21.53) * mm, "end": v(216.06, -21.94) * mm});
            skLineSegment(sketch, "E156.77.2", {"start": v(216.06, -21.94) * mm, "end": v(216.52, -21.96) * mm});
            skLineSegment(sketch, "E156.77.3", {"start": v(215.6, -21.91) * mm, "end": v(215.86, -21.53) * mm});
            skLineSegment(sketch, "E156.78.0", {"start": v(216.52, -21.96) * mm, "end": v(216.98, -21.97) * mm});
            skLineSegment(sketch, "E156.78.1", {"start": v(217.2, -21.57) * mm, "end": v(217.44, -21.97) * mm});
            skLineSegment(sketch, "E156.78.2", {"start": v(217.44, -21.97) * mm, "end": v(217.9, -21.96) * mm});
            skLineSegment(sketch, "E156.78.3", {"start": v(216.98, -21.97) * mm, "end": v(217.2, -21.57) * mm});
            skLineSegment(sketch, "E156.79.0", {"start": v(217.9, -21.96) * mm, "end": v(218.36, -21.94) * mm});
            skLineSegment(sketch, "E156.79.1", {"start": v(218.56, -21.53) * mm, "end": v(218.82, -21.91) * mm});
            skLineSegment(sketch, "E156.79.2", {"start": v(218.82, -21.91) * mm, "end": v(219.28, -21.87) * mm});
            skLineSegment(sketch, "E156.79.3", {"start": v(218.36, -21.94) * mm, "end": v(218.56, -21.53) * mm});
            skLineSegment(sketch, "E156.80.0", {"start": v(219.28, -21.87) * mm, "end": v(219.74, -21.83) * mm});
            skLineSegment(sketch, "E156.80.1", {"start": v(219.91, -21.4) * mm, "end": v(220.2, -21.77) * mm});
            skLineSegment(sketch, "E156.80.2", {"start": v(220.2, -21.77) * mm, "end": v(220.65, -21.7) * mm});
            skLineSegment(sketch, "E156.80.3", {"start": v(219.74, -21.83) * mm, "end": v(219.91, -21.4) * mm});
            skLineSegment(sketch, "E156.81.0", {"start": v(220.65, -21.7) * mm, "end": v(221.1, -21.62) * mm});
            skLineSegment(sketch, "E156.81.1", {"start": v(221.25, -21.19) * mm, "end": v(221.55, -21.54) * mm});
            skLineSegment(sketch, "E156.81.2", {"start": v(221.55, -21.54) * mm, "end": v(222, -21.44) * mm});
            skLineSegment(sketch, "E156.81.3", {"start": v(221.1, -21.62) * mm, "end": v(221.25, -21.19) * mm});
            skLineSegment(sketch, "E156.82.0", {"start": v(222, -21.44) * mm, "end": v(222.45, -21.34) * mm});
            skLineSegment(sketch, "E156.82.1", {"start": v(222.57, -20.9) * mm, "end": v(222.9, -21.22) * mm});
            skLineSegment(sketch, "E156.82.2", {"start": v(222.9, -21.22) * mm, "end": v(223.34, -21.1) * mm});
            skLineSegment(sketch, "E156.82.3", {"start": v(222.45, -21.34) * mm, "end": v(222.57, -20.9) * mm});
            skLineSegment(sketch, "E156.83.0", {"start": v(223.34, -21.1) * mm, "end": v(223.78, -20.97) * mm});
            skLineSegment(sketch, "E156.83.1", {"start": v(223.88, -20.52) * mm, "end": v(224.22, -20.82) * mm});
            skLineSegment(sketch, "E156.83.2", {"start": v(224.22, -20.82) * mm, "end": v(224.65, -20.67) * mm});
            skLineSegment(sketch, "E156.83.3", {"start": v(223.78, -20.97) * mm, "end": v(223.88, -20.52) * mm});
            skLineSegment(sketch, "E156.84.0", {"start": v(224.65, -20.67) * mm, "end": v(225.08, -20.51) * mm});
            skLineSegment(sketch, "E156.84.1", {"start": v(225.15, -20.06) * mm, "end": v(225.51, -20.34) * mm});
            skLineSegment(sketch, "E156.84.2", {"start": v(225.51, -20.34) * mm, "end": v(225.94, -20.16) * mm});
            skLineSegment(sketch, "E156.84.3", {"start": v(225.08, -20.51) * mm, "end": v(225.15, -20.06) * mm});
            skLineSegment(sketch, "E156.85.0", {"start": v(225.94, -20.16) * mm, "end": v(226.36, -19.98) * mm});
            skLineSegment(sketch, "E156.85.1", {"start": v(226.4, -19.52) * mm, "end": v(226.77, -19.78) * mm});
            skLineSegment(sketch, "E156.85.2", {"start": v(226.77, -19.78) * mm, "end": v(227.18, -19.58) * mm});
            skLineSegment(sketch, "E156.85.3", {"start": v(226.36, -19.98) * mm, "end": v(226.4, -19.52) * mm});
            skLineSegment(sketch, "E156.86.0", {"start": v(227.18, -19.58) * mm, "end": v(227.6, -19.36) * mm});
            skLineSegment(sketch, "E156.86.1", {"start": v(227.6, -18.9) * mm, "end": v(228, -19.14) * mm});
            skLineSegment(sketch, "E156.86.2", {"start": v(228, -19.14) * mm, "end": v(228.4, -18.91) * mm});
            skLineSegment(sketch, "E156.86.3", {"start": v(227.6, -19.36) * mm, "end": v(227.6, -18.9) * mm});
            skLineSegment(sketch, "E156.87.0", {"start": v(228.4, -18.91) * mm, "end": v(228.79, -18.67) * mm});
            skLineSegment(sketch, "E156.87.1", {"start": v(228.77, -18.21) * mm, "end": v(229.18, -18.43) * mm});
            skLineSegment(sketch, "E156.87.2", {"start": v(229.18, -18.43) * mm, "end": v(229.56, -18.17) * mm});
            skLineSegment(sketch, "E156.87.3", {"start": v(228.79, -18.67) * mm, "end": v(228.77, -18.21) * mm});
            skLineSegment(sketch, "E156.88.0", {"start": v(229.56, -18.17) * mm, "end": v(229.94, -17.9) * mm});
            skLineSegment(sketch, "E156.88.1", {"start": v(229.89, -17.45) * mm, "end": v(230.3, -17.64) * mm});
            skLineSegment(sketch, "E156.88.2", {"start": v(230.3, -17.64) * mm, "end": v(230.68, -17.36) * mm});
            skLineSegment(sketch, "E156.88.3", {"start": v(229.94, -17.9) * mm, "end": v(229.89, -17.45) * mm});
            skLineSegment(sketch, "E156.89.0", {"start": v(230.68, -17.36) * mm, "end": v(231.04, -17.07) * mm});
            skLineSegment(sketch, "E156.89.1", {"start": v(230.96, -16.62) * mm, "end": v(231.4, -16.78) * mm});
            skLineSegment(sketch, "E156.89.2", {"start": v(231.4, -16.78) * mm, "end": v(231.74, -16.48) * mm});
            skLineSegment(sketch, "E156.89.3", {"start": v(231.04, -17.07) * mm, "end": v(230.96, -16.62) * mm});
            skLineSegment(sketch, "E156.90.0", {"start": v(231.74, -16.48) * mm, "end": v(232.08, -16.17) * mm});
            skLineSegment(sketch, "E156.90.1", {"start": v(231.98, -15.72) * mm, "end": v(232.42, -15.86) * mm});
            skLineSegment(sketch, "E156.90.2", {"start": v(232.42, -15.86) * mm, "end": v(232.75, -15.54) * mm});
            skLineSegment(sketch, "E156.90.3", {"start": v(232.08, -16.17) * mm, "end": v(231.98, -15.72) * mm});
            skPoint(sketch, "E156.center", {"position": v(217.2, 0) * mm});
            skLineSegment(sketch, "E156.anchor2", {"start": v(217.2, 0) * mm, "end": v(231.74, -16.48) * mm, "construction": true});
            skArc(sketch, "E157", {"start": v(195.77, 4.8) * mm, "mid": v(196.31, -6.79) * mm, "end": v(202.68, -16.48) * mm, "construction": true});
            skArc(sketch, "E158", {"start": v(201.67, 15.54) * mm, "mid": v(197.96, 10.58) * mm, "end": v(195.77, 4.8) * mm});
            skArc(sketch, "E159", {"start": v(231.74, 16.48) * mm, "mid": v(227.8, 19.25) * mm, "end": v(223.34, 21.1) * mm});
            skArc(sketch, "E160", {"start": v(232.75, -15.54) * mm, "mid": v(236.46, -10.58) * mm, "end": v(238.65, -4.8) * mm});
            skArc(sketch, "E161", {"start": v(202.68, -16.48) * mm, "mid": v(206.63, -19.25) * mm, "end": v(211.08, -21.1) * mm});
            skLineSegment(sketch, "E162.0", {"start": v(162.9, -27.4) * mm, "end": v(217.2, -27.4) * mm});
            skArc(sketch, "E162.1", {"start": v(108.6, 26.9) * mm, "mid": v(81.2, 54.3) * mm, "end": v(108.6, 81.7) * mm});
            skArc(sketch, "E162.2", {"start": v(162.9, 81.7) * mm, "mid": v(182.29, 73.68) * mm, "end": v(190.31, 54.3) * mm});
            skArc(sketch, "E162.3", {"start": v(190.31, 54.3) * mm, "mid": v(198.2, 35.28) * mm, "end": v(217.2, 27.4) * mm});
            skArc(sketch, "E162.4", {"start": v(135.5, 0) * mm, "mid": v(127.62, 19.02) * mm, "end": v(108.6, 26.9) * mm});
            skArc(sketch, "E162.5", {"start": v(217.2, 27.4) * mm, "mid": v(244.62, 0) * mm, "end": v(217.2, -27.4) * mm});
            skArc(sketch, "E162.6", {"start": v(162.9, -27.4) * mm, "mid": v(143.53, -19.38) * mm, "end": v(135.5, 0) * mm});
            skLineSegment(sketch, "E162.7", {"start": v(108.6, 81.7) * mm, "end": v(162.9, 81.7) * mm});
            skSolve(sketch);
        }
        {
            var Q0;
            Q0=makeQuery(id+"F14.imprint","IMPRINT",FACE,{"disambiguationData":[TD([[makeQuery(id+"F14.imprint","IMPRINT",EDGE,{"derivedFrom":sQuery(id+"F14.wireOp",EDGE,"E103")}),-1.0]])]});
            extrude(context, id + "F15", {"entities" : qUnion([Q0]), "depth" : getVariable(context, 'thick'), "offsetDistance" : 25.4 * mm});
        }
    });
